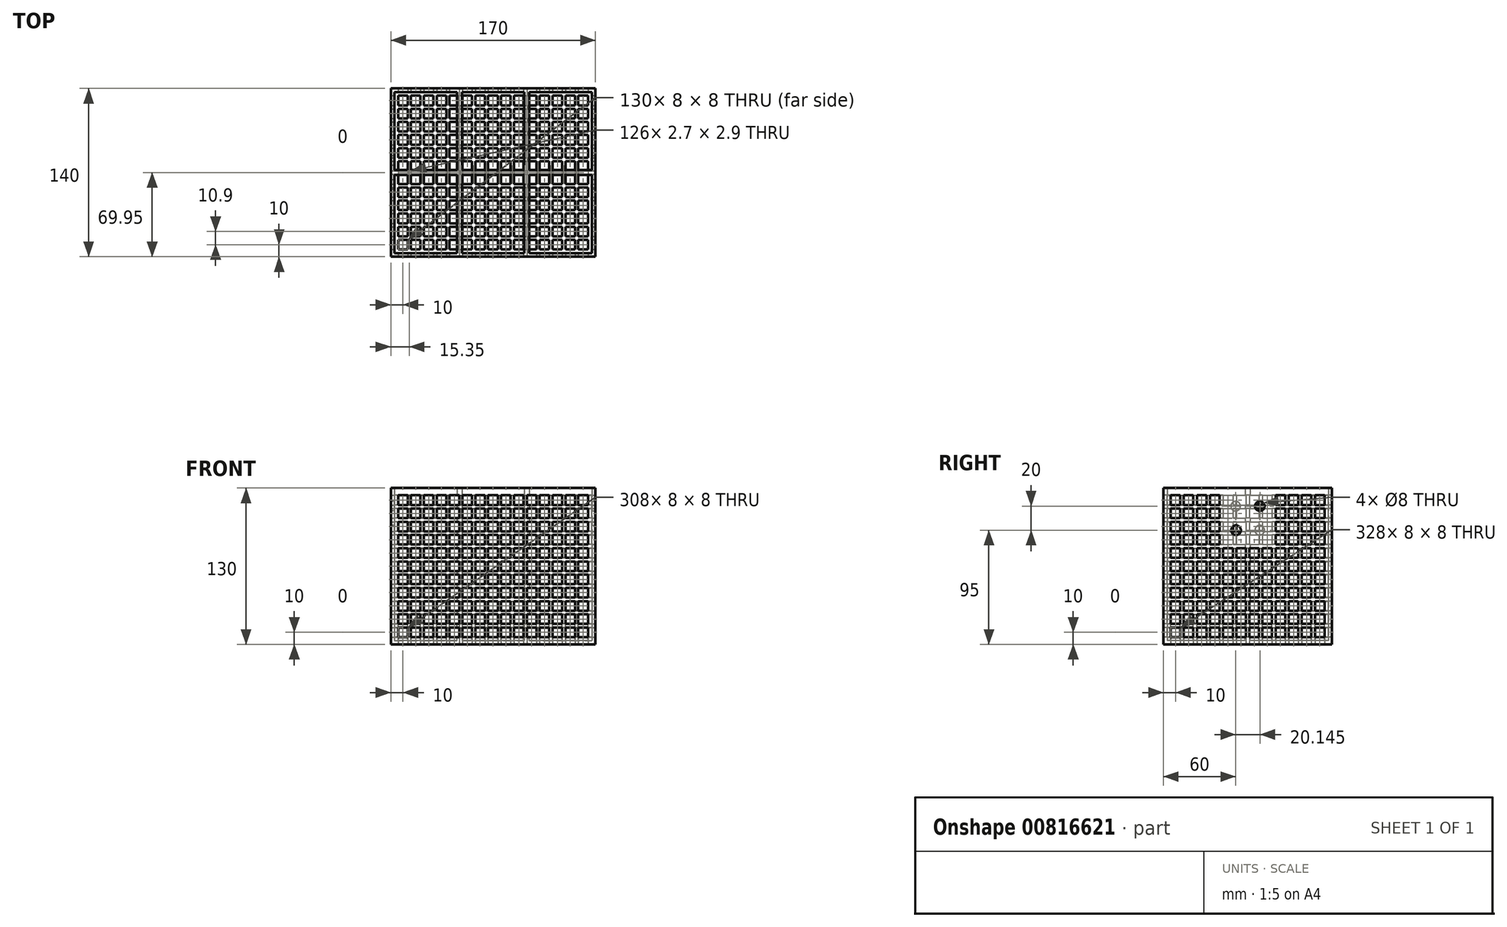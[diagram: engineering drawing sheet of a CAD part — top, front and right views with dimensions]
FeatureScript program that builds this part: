
annotation { "Feature Type Name" : "Feature", "Feature Type Description" : "" }
export const myFeature = defineFeature(function(context is Context, id is Id, definition is map)
    precondition{}
    {
        {
            var Q0;
            Q0=qCreatedBy(makeId("Top.planeOp"),FACE);
            var sketch = newSketch(context, id + "F0", { "sketchPlane" : qUnion([Q0])});
            skLineSegment(sketch, "E0.bottom", {"start": v(0, 0) * mm, "end": v(170, 0) * mm});
            skLineSegment(sketch, "E0.top", {"start": v(0, 140) * mm, "end": v(170, 140) * mm});
            skLineSegment(sketch, "E0.left", {"start": v(0, 0) * mm, "end": v(0, 140) * mm});
            skLineSegment(sketch, "E0.right", {"start": v(170, 0) * mm, "end": v(170, 140) * mm});
            skSolve(sketch);
        }
        {
            var Q0;
            Q0 = qSketchRegion(id + "F0", true);
            extrude(context, id + "F1", {"entities" : qUnion([Q0]), "depth" : 130 * mm, "offsetDistance" : 25 * mm});
        }
        {
            var Q0;
            Q0=qCreatedBy(makeId("Top.planeOp"),FACE);
            cPlane(context, id + "F2", {"entities" : qUnion([Q0]), "cplaneType" : CPlaneType.OFFSET, "offset" : 3 * mm, "width" : 150 * mm, "height" : 150 * mm});
        }
        {
            var Q0;
            Q0=qCreatedBy(id+"F2.planeOp",FACE);
            var sketch = newSketch(context, id + "F3", { "sketchPlane" : qUnion([Q0])});
            skLineSegment(sketch, "E1.bottom", {"start": v(3, 68) * mm, "end": v(55, 68) * mm});
            skLineSegment(sketch, "E1.top", {"start": v(3, 3) * mm, "end": v(55, 3) * mm});
            skLineSegment(sketch, "E1.left", {"start": v(3, 68) * mm, "end": v(3, 3) * mm});
            skLineSegment(sketch, "E1.right", {"start": v(55, 68) * mm, "end": v(55, 3) * mm});
            skLineSegment(sketch, "E2", {"start": v(0, 137) * mm, "end": v(173.16, 137) * mm, "construction": true});
            skLineSegment(sketch, "E3", {"start": v(167, 0) * mm, "end": v(167, 146.13) * mm, "construction": true});
            skLineSegment(sketch, "E4.0.1.0", {"start": v(3, 137) * mm, "end": v(55, 137) * mm});
            skLineSegment(sketch, "E4.0.1.1", {"start": v(55, 137) * mm, "end": v(55, 72) * mm});
            skLineSegment(sketch, "E4.0.1.2", {"start": v(3, 72) * mm, "end": v(55, 72) * mm});
            skLineSegment(sketch, "E4.0.1.3", {"start": v(3, 137) * mm, "end": v(3, 72) * mm});
            skLineSegment(sketch, "E4.1.0.0", {"start": v(59, 68) * mm, "end": v(111, 68) * mm});
            skLineSegment(sketch, "E4.1.0.1", {"start": v(111, 68) * mm, "end": v(111, 3) * mm});
            skLineSegment(sketch, "E4.1.0.2", {"start": v(59, 3) * mm, "end": v(111, 3) * mm});
            skLineSegment(sketch, "E4.1.0.3", {"start": v(59, 68) * mm, "end": v(59, 3) * mm});
            skLineSegment(sketch, "E4.1.1.0", {"start": v(59, 137) * mm, "end": v(111, 137) * mm});
            skLineSegment(sketch, "E4.1.1.1", {"start": v(111, 137) * mm, "end": v(111, 72) * mm});
            skLineSegment(sketch, "E4.1.1.2", {"start": v(59, 72) * mm, "end": v(111, 72) * mm});
            skLineSegment(sketch, "E4.1.1.3", {"start": v(59, 137) * mm, "end": v(59, 72) * mm});
            skLineSegment(sketch, "E4.2.0.0", {"start": v(115, 68) * mm, "end": v(167, 68) * mm});
            skLineSegment(sketch, "E4.2.0.1", {"start": v(167, 68) * mm, "end": v(167, 3) * mm});
            skLineSegment(sketch, "E4.2.0.2", {"start": v(115, 3) * mm, "end": v(167, 3) * mm});
            skLineSegment(sketch, "E4.2.0.3", {"start": v(115, 68) * mm, "end": v(115, 3) * mm});
            skLineSegment(sketch, "E4.2.1.0", {"start": v(115, 137) * mm, "end": v(167, 137) * mm});
            skLineSegment(sketch, "E4.2.1.1", {"start": v(167, 137) * mm, "end": v(167, 72) * mm});
            skLineSegment(sketch, "E4.2.1.2", {"start": v(115, 72) * mm, "end": v(167, 72) * mm});
            skLineSegment(sketch, "E4.2.1.3", {"start": v(115, 137) * mm, "end": v(115, 72) * mm});
            skLineSegment(sketch, "E4.direction1", {"start": v(3, 3) * mm, "end": v(59, 3) * mm, "construction": true});
            skLineSegment(sketch, "E4.direction2", {"start": v(3, 3) * mm, "end": v(3, 72) * mm, "construction": true});
            skSolve(sketch);
        }
        {
            var Q0;
            Q0 = qSketchRegion(id + "F3", true);
            extrude(context, id + "F4", {"entities" : qUnion([Q0]), "operationType" : NewBodyOperationType.REMOVE, "endBound" : BoundingType.UP_TO_NEXT, "depth" : 25 * mm, "offsetDistance" : 25 * mm});
        }
        {
            var Q0;
            Q0=makeQuery(id+"F1.opExtrude","SWEPT_FACE",FACE,{"disambiguationData":[OSD([sQuery(id+"F0.wireOp",EDGE,"E0.right")])]});
            var sketch = newSketch(context, id + "F5", { "sketchPlane" : qUnion([Q0])});
            skLineSegment(sketch, "E5.bottom", {"start": v(6, 14) * mm, "end": v(14, 14) * mm});
            skLineSegment(sketch, "E5.top", {"start": v(6, 6) * mm, "end": v(14, 6) * mm});
            skLineSegment(sketch, "E5.left", {"start": v(6, 14) * mm, "end": v(6, 6) * mm});
            skLineSegment(sketch, "E5.right", {"start": v(14, 14) * mm, "end": v(14, 6) * mm});
            skLineSegment(sketch, "E6.0.1.0", {"start": v(6, 25) * mm, "end": v(14, 25) * mm});
            skLineSegment(sketch, "E6.0.1.1", {"start": v(6, 25) * mm, "end": v(6, 17) * mm});
            skLineSegment(sketch, "E6.0.1.2", {"start": v(14, 25) * mm, "end": v(14, 17) * mm});
            skLineSegment(sketch, "E6.0.1.3", {"start": v(6, 17) * mm, "end": v(14, 17) * mm});
            skLineSegment(sketch, "E6.0.2.0", {"start": v(6, 36) * mm, "end": v(14, 36) * mm});
            skLineSegment(sketch, "E6.0.2.1", {"start": v(6, 36) * mm, "end": v(6, 28) * mm});
            skLineSegment(sketch, "E6.0.2.2", {"start": v(14, 36) * mm, "end": v(14, 28) * mm});
            skLineSegment(sketch, "E6.0.2.3", {"start": v(6, 28) * mm, "end": v(14, 28) * mm});
            skLineSegment(sketch, "E6.0.3.0", {"start": v(6, 47) * mm, "end": v(14, 47) * mm});
            skLineSegment(sketch, "E6.0.3.1", {"start": v(6, 47) * mm, "end": v(6, 39) * mm});
            skLineSegment(sketch, "E6.0.3.2", {"start": v(14, 47) * mm, "end": v(14, 39) * mm});
            skLineSegment(sketch, "E6.0.3.3", {"start": v(6, 39) * mm, "end": v(14, 39) * mm});
            skLineSegment(sketch, "E6.0.4.0", {"start": v(6, 58) * mm, "end": v(14, 58) * mm});
            skLineSegment(sketch, "E6.0.4.1", {"start": v(6, 58) * mm, "end": v(6, 50) * mm});
            skLineSegment(sketch, "E6.0.4.2", {"start": v(14, 58) * mm, "end": v(14, 50) * mm});
            skLineSegment(sketch, "E6.0.4.3", {"start": v(6, 50) * mm, "end": v(14, 50) * mm});
            skLineSegment(sketch, "E6.0.5.0", {"start": v(6, 69) * mm, "end": v(14, 69) * mm});
            skLineSegment(sketch, "E6.0.5.1", {"start": v(6, 69) * mm, "end": v(6, 61) * mm});
            skLineSegment(sketch, "E6.0.5.2", {"start": v(14, 69) * mm, "end": v(14, 61) * mm});
            skLineSegment(sketch, "E6.0.5.3", {"start": v(6, 61) * mm, "end": v(14, 61) * mm});
            skLineSegment(sketch, "E6.0.6.0", {"start": v(6, 80) * mm, "end": v(14, 80) * mm});
            skLineSegment(sketch, "E6.0.6.1", {"start": v(6, 80) * mm, "end": v(6, 72) * mm});
            skLineSegment(sketch, "E6.0.6.2", {"start": v(14, 80) * mm, "end": v(14, 72) * mm});
            skLineSegment(sketch, "E6.0.6.3", {"start": v(6, 72) * mm, "end": v(14, 72) * mm});
            skLineSegment(sketch, "E6.0.7.0", {"start": v(6, 91) * mm, "end": v(14, 91) * mm});
            skLineSegment(sketch, "E6.0.7.1", {"start": v(6, 91) * mm, "end": v(6, 83) * mm});
            skLineSegment(sketch, "E6.0.7.2", {"start": v(14, 91) * mm, "end": v(14, 83) * mm});
            skLineSegment(sketch, "E6.0.7.3", {"start": v(6, 83) * mm, "end": v(14, 83) * mm});
            skLineSegment(sketch, "E6.0.8.0", {"start": v(6, 102) * mm, "end": v(14, 102) * mm});
            skLineSegment(sketch, "E6.0.8.1", {"start": v(6, 102) * mm, "end": v(6, 94) * mm});
            skLineSegment(sketch, "E6.0.8.2", {"start": v(14, 102) * mm, "end": v(14, 94) * mm});
            skLineSegment(sketch, "E6.0.8.3", {"start": v(6, 94) * mm, "end": v(14, 94) * mm});
            skLineSegment(sketch, "E6.0.9.0", {"start": v(6, 113) * mm, "end": v(14, 113) * mm});
            skLineSegment(sketch, "E6.0.9.1", {"start": v(6, 113) * mm, "end": v(6, 105) * mm});
            skLineSegment(sketch, "E6.0.9.2", {"start": v(14, 113) * mm, "end": v(14, 105) * mm});
            skLineSegment(sketch, "E6.0.9.3", {"start": v(6, 105) * mm, "end": v(14, 105) * mm});
            skLineSegment(sketch, "E6.0.10.0", {"start": v(6, 124) * mm, "end": v(14, 124) * mm});
            skLineSegment(sketch, "E6.0.10.1", {"start": v(6, 124) * mm, "end": v(6, 116) * mm});
            skLineSegment(sketch, "E6.0.10.2", {"start": v(14, 124) * mm, "end": v(14, 116) * mm});
            skLineSegment(sketch, "E6.0.10.3", {"start": v(6, 116) * mm, "end": v(14, 116) * mm});
            skLineSegment(sketch, "E6.1.0.0", {"start": v(16.9, 14) * mm, "end": v(24.9, 14) * mm});
            skLineSegment(sketch, "E6.1.0.1", {"start": v(16.9, 14) * mm, "end": v(16.9, 6) * mm});
            skLineSegment(sketch, "E6.1.0.2", {"start": v(24.9, 14) * mm, "end": v(24.9, 6) * mm});
            skLineSegment(sketch, "E6.1.0.3", {"start": v(16.9, 6) * mm, "end": v(24.9, 6) * mm});
            skLineSegment(sketch, "E6.1.1.0", {"start": v(16.9, 25) * mm, "end": v(24.9, 25) * mm});
            skLineSegment(sketch, "E6.1.1.1", {"start": v(16.9, 25) * mm, "end": v(16.9, 17) * mm});
            skLineSegment(sketch, "E6.1.1.2", {"start": v(24.9, 25) * mm, "end": v(24.9, 17) * mm});
            skLineSegment(sketch, "E6.1.1.3", {"start": v(16.9, 17) * mm, "end": v(24.9, 17) * mm});
            skLineSegment(sketch, "E6.1.2.0", {"start": v(16.9, 36) * mm, "end": v(24.9, 36) * mm});
            skLineSegment(sketch, "E6.1.2.1", {"start": v(16.9, 36) * mm, "end": v(16.9, 28) * mm});
            skLineSegment(sketch, "E6.1.2.2", {"start": v(24.9, 36) * mm, "end": v(24.9, 28) * mm});
            skLineSegment(sketch, "E6.1.2.3", {"start": v(16.9, 28) * mm, "end": v(24.9, 28) * mm});
            skLineSegment(sketch, "E6.1.3.0", {"start": v(16.9, 47) * mm, "end": v(24.9, 47) * mm});
            skLineSegment(sketch, "E6.1.3.1", {"start": v(16.9, 47) * mm, "end": v(16.9, 39) * mm});
            skLineSegment(sketch, "E6.1.3.2", {"start": v(24.9, 47) * mm, "end": v(24.9, 39) * mm});
            skLineSegment(sketch, "E6.1.3.3", {"start": v(16.9, 39) * mm, "end": v(24.9, 39) * mm});
            skLineSegment(sketch, "E6.1.4.0", {"start": v(16.9, 58) * mm, "end": v(24.9, 58) * mm});
            skLineSegment(sketch, "E6.1.4.1", {"start": v(16.9, 58) * mm, "end": v(16.9, 50) * mm});
            skLineSegment(sketch, "E6.1.4.2", {"start": v(24.9, 58) * mm, "end": v(24.9, 50) * mm});
            skLineSegment(sketch, "E6.1.4.3", {"start": v(16.9, 50) * mm, "end": v(24.9, 50) * mm});
            skLineSegment(sketch, "E6.1.5.0", {"start": v(16.9, 69) * mm, "end": v(24.9, 69) * mm});
            skLineSegment(sketch, "E6.1.5.1", {"start": v(16.9, 69) * mm, "end": v(16.9, 61) * mm});
            skLineSegment(sketch, "E6.1.5.2", {"start": v(24.9, 69) * mm, "end": v(24.9, 61) * mm});
            skLineSegment(sketch, "E6.1.5.3", {"start": v(16.9, 61) * mm, "end": v(24.9, 61) * mm});
            skLineSegment(sketch, "E6.1.6.0", {"start": v(16.9, 80) * mm, "end": v(24.9, 80) * mm});
            skLineSegment(sketch, "E6.1.6.1", {"start": v(16.9, 80) * mm, "end": v(16.9, 72) * mm});
            skLineSegment(sketch, "E6.1.6.2", {"start": v(24.9, 80) * mm, "end": v(24.9, 72) * mm});
            skLineSegment(sketch, "E6.1.6.3", {"start": v(16.9, 72) * mm, "end": v(24.9, 72) * mm});
            skLineSegment(sketch, "E6.1.7.0", {"start": v(16.9, 91) * mm, "end": v(24.9, 91) * mm});
            skLineSegment(sketch, "E6.1.7.1", {"start": v(16.9, 91) * mm, "end": v(16.9, 83) * mm});
            skLineSegment(sketch, "E6.1.7.2", {"start": v(24.9, 91) * mm, "end": v(24.9, 83) * mm});
            skLineSegment(sketch, "E6.1.7.3", {"start": v(16.9, 83) * mm, "end": v(24.9, 83) * mm});
            skLineSegment(sketch, "E6.1.8.0", {"start": v(16.9, 102) * mm, "end": v(24.9, 102) * mm});
            skLineSegment(sketch, "E6.1.8.1", {"start": v(16.9, 102) * mm, "end": v(16.9, 94) * mm});
            skLineSegment(sketch, "E6.1.8.2", {"start": v(24.9, 102) * mm, "end": v(24.9, 94) * mm});
            skLineSegment(sketch, "E6.1.8.3", {"start": v(16.9, 94) * mm, "end": v(24.9, 94) * mm});
            skLineSegment(sketch, "E6.1.9.0", {"start": v(16.9, 113) * mm, "end": v(24.9, 113) * mm});
            skLineSegment(sketch, "E6.1.9.1", {"start": v(16.9, 113) * mm, "end": v(16.9, 105) * mm});
            skLineSegment(sketch, "E6.1.9.2", {"start": v(24.9, 113) * mm, "end": v(24.9, 105) * mm});
            skLineSegment(sketch, "E6.1.9.3", {"start": v(16.9, 105) * mm, "end": v(24.9, 105) * mm});
            skLineSegment(sketch, "E6.1.10.0", {"start": v(16.9, 124) * mm, "end": v(24.9, 124) * mm});
            skLineSegment(sketch, "E6.1.10.1", {"start": v(16.9, 124) * mm, "end": v(16.9, 116) * mm});
            skLineSegment(sketch, "E6.1.10.2", {"start": v(24.9, 124) * mm, "end": v(24.9, 116) * mm});
            skLineSegment(sketch, "E6.1.10.3", {"start": v(16.9, 116) * mm, "end": v(24.9, 116) * mm});
            skLineSegment(sketch, "E6.2.0.0", {"start": v(27.8, 14) * mm, "end": v(35.8, 14) * mm});
            skLineSegment(sketch, "E6.2.0.1", {"start": v(27.8, 14) * mm, "end": v(27.8, 6) * mm});
            skLineSegment(sketch, "E6.2.0.2", {"start": v(35.8, 14) * mm, "end": v(35.8, 6) * mm});
            skLineSegment(sketch, "E6.2.0.3", {"start": v(27.8, 6) * mm, "end": v(35.8, 6) * mm});
            skLineSegment(sketch, "E6.2.1.0", {"start": v(27.8, 25) * mm, "end": v(35.8, 25) * mm});
            skLineSegment(sketch, "E6.2.1.1", {"start": v(27.8, 25) * mm, "end": v(27.8, 17) * mm});
            skLineSegment(sketch, "E6.2.1.2", {"start": v(35.8, 25) * mm, "end": v(35.8, 17) * mm});
            skLineSegment(sketch, "E6.2.1.3", {"start": v(27.8, 17) * mm, "end": v(35.8, 17) * mm});
            skLineSegment(sketch, "E6.2.2.0", {"start": v(27.8, 36) * mm, "end": v(35.8, 36) * mm});
            skLineSegment(sketch, "E6.2.2.1", {"start": v(27.8, 36) * mm, "end": v(27.8, 28) * mm});
            skLineSegment(sketch, "E6.2.2.2", {"start": v(35.8, 36) * mm, "end": v(35.8, 28) * mm});
            skLineSegment(sketch, "E6.2.2.3", {"start": v(27.8, 28) * mm, "end": v(35.8, 28) * mm});
            skLineSegment(sketch, "E6.2.3.0", {"start": v(27.8, 47) * mm, "end": v(35.8, 47) * mm});
            skLineSegment(sketch, "E6.2.3.1", {"start": v(27.8, 47) * mm, "end": v(27.8, 39) * mm});
            skLineSegment(sketch, "E6.2.3.2", {"start": v(35.8, 47) * mm, "end": v(35.8, 39) * mm});
            skLineSegment(sketch, "E6.2.3.3", {"start": v(27.8, 39) * mm, "end": v(35.8, 39) * mm});
            skLineSegment(sketch, "E6.2.4.0", {"start": v(27.8, 58) * mm, "end": v(35.8, 58) * mm});
            skLineSegment(sketch, "E6.2.4.1", {"start": v(27.8, 58) * mm, "end": v(27.8, 50) * mm});
            skLineSegment(sketch, "E6.2.4.2", {"start": v(35.8, 58) * mm, "end": v(35.8, 50) * mm});
            skLineSegment(sketch, "E6.2.4.3", {"start": v(27.8, 50) * mm, "end": v(35.8, 50) * mm});
            skLineSegment(sketch, "E6.2.5.0", {"start": v(27.8, 69) * mm, "end": v(35.8, 69) * mm});
            skLineSegment(sketch, "E6.2.5.1", {"start": v(27.8, 69) * mm, "end": v(27.8, 61) * mm});
            skLineSegment(sketch, "E6.2.5.2", {"start": v(35.8, 69) * mm, "end": v(35.8, 61) * mm});
            skLineSegment(sketch, "E6.2.5.3", {"start": v(27.8, 61) * mm, "end": v(35.8, 61) * mm});
            skLineSegment(sketch, "E6.2.6.0", {"start": v(27.8, 80) * mm, "end": v(35.8, 80) * mm});
            skLineSegment(sketch, "E6.2.6.1", {"start": v(27.8, 80) * mm, "end": v(27.8, 72) * mm});
            skLineSegment(sketch, "E6.2.6.2", {"start": v(35.8, 80) * mm, "end": v(35.8, 72) * mm});
            skLineSegment(sketch, "E6.2.6.3", {"start": v(27.8, 72) * mm, "end": v(35.8, 72) * mm});
            skLineSegment(sketch, "E6.2.7.0", {"start": v(27.8, 91) * mm, "end": v(35.8, 91) * mm});
            skLineSegment(sketch, "E6.2.7.1", {"start": v(27.8, 91) * mm, "end": v(27.8, 83) * mm});
            skLineSegment(sketch, "E6.2.7.2", {"start": v(35.8, 91) * mm, "end": v(35.8, 83) * mm});
            skLineSegment(sketch, "E6.2.7.3", {"start": v(27.8, 83) * mm, "end": v(35.8, 83) * mm});
            skLineSegment(sketch, "E6.2.8.0", {"start": v(27.8, 102) * mm, "end": v(35.8, 102) * mm});
            skLineSegment(sketch, "E6.2.8.1", {"start": v(27.8, 102) * mm, "end": v(27.8, 94) * mm});
            skLineSegment(sketch, "E6.2.8.2", {"start": v(35.8, 102) * mm, "end": v(35.8, 94) * mm});
            skLineSegment(sketch, "E6.2.8.3", {"start": v(27.8, 94) * mm, "end": v(35.8, 94) * mm});
            skLineSegment(sketch, "E6.2.9.0", {"start": v(27.8, 113) * mm, "end": v(35.8, 113) * mm});
            skLineSegment(sketch, "E6.2.9.1", {"start": v(27.8, 113) * mm, "end": v(27.8, 105) * mm});
            skLineSegment(sketch, "E6.2.9.2", {"start": v(35.8, 113) * mm, "end": v(35.8, 105) * mm});
            skLineSegment(sketch, "E6.2.9.3", {"start": v(27.8, 105) * mm, "end": v(35.8, 105) * mm});
            skLineSegment(sketch, "E6.2.10.0", {"start": v(27.8, 124) * mm, "end": v(35.8, 124) * mm});
            skLineSegment(sketch, "E6.2.10.1", {"start": v(27.8, 124) * mm, "end": v(27.8, 116) * mm});
            skLineSegment(sketch, "E6.2.10.2", {"start": v(35.8, 124) * mm, "end": v(35.8, 116) * mm});
            skLineSegment(sketch, "E6.2.10.3", {"start": v(27.8, 116) * mm, "end": v(35.8, 116) * mm});
            skLineSegment(sketch, "E6.3.0.0", {"start": v(38.7, 14) * mm, "end": v(46.7, 14) * mm});
            skLineSegment(sketch, "E6.3.0.1", {"start": v(38.7, 14) * mm, "end": v(38.7, 6) * mm});
            skLineSegment(sketch, "E6.3.0.2", {"start": v(46.7, 14) * mm, "end": v(46.7, 6) * mm});
            skLineSegment(sketch, "E6.3.0.3", {"start": v(38.7, 6) * mm, "end": v(46.7, 6) * mm});
            skLineSegment(sketch, "E6.3.1.0", {"start": v(38.7, 25) * mm, "end": v(46.7, 25) * mm});
            skLineSegment(sketch, "E6.3.1.1", {"start": v(38.7, 25) * mm, "end": v(38.7, 17) * mm});
            skLineSegment(sketch, "E6.3.1.2", {"start": v(46.7, 25) * mm, "end": v(46.7, 17) * mm});
            skLineSegment(sketch, "E6.3.1.3", {"start": v(38.7, 17) * mm, "end": v(46.7, 17) * mm});
            skLineSegment(sketch, "E6.3.2.0", {"start": v(38.7, 36) * mm, "end": v(46.7, 36) * mm});
            skLineSegment(sketch, "E6.3.2.1", {"start": v(38.7, 36) * mm, "end": v(38.7, 28) * mm});
            skLineSegment(sketch, "E6.3.2.2", {"start": v(46.7, 36) * mm, "end": v(46.7, 28) * mm});
            skLineSegment(sketch, "E6.3.2.3", {"start": v(38.7, 28) * mm, "end": v(46.7, 28) * mm});
            skLineSegment(sketch, "E6.3.3.0", {"start": v(38.7, 47) * mm, "end": v(46.7, 47) * mm});
            skLineSegment(sketch, "E6.3.3.1", {"start": v(38.7, 47) * mm, "end": v(38.7, 39) * mm});
            skLineSegment(sketch, "E6.3.3.2", {"start": v(46.7, 47) * mm, "end": v(46.7, 39) * mm});
            skLineSegment(sketch, "E6.3.3.3", {"start": v(38.7, 39) * mm, "end": v(46.7, 39) * mm});
            skLineSegment(sketch, "E6.3.4.0", {"start": v(38.7, 58) * mm, "end": v(46.7, 58) * mm});
            skLineSegment(sketch, "E6.3.4.1", {"start": v(38.7, 58) * mm, "end": v(38.7, 50) * mm});
            skLineSegment(sketch, "E6.3.4.2", {"start": v(46.7, 58) * mm, "end": v(46.7, 50) * mm});
            skLineSegment(sketch, "E6.3.4.3", {"start": v(38.7, 50) * mm, "end": v(46.7, 50) * mm});
            skLineSegment(sketch, "E6.3.5.0", {"start": v(38.7, 69) * mm, "end": v(46.7, 69) * mm});
            skLineSegment(sketch, "E6.3.5.1", {"start": v(38.7, 69) * mm, "end": v(38.7, 61) * mm});
            skLineSegment(sketch, "E6.3.5.2", {"start": v(46.7, 69) * mm, "end": v(46.7, 61) * mm});
            skLineSegment(sketch, "E6.3.5.3", {"start": v(38.7, 61) * mm, "end": v(46.7, 61) * mm});
            skLineSegment(sketch, "E6.3.6.0", {"start": v(38.7, 80) * mm, "end": v(46.7, 80) * mm});
            skLineSegment(sketch, "E6.3.6.1", {"start": v(38.7, 80) * mm, "end": v(38.7, 72) * mm});
            skLineSegment(sketch, "E6.3.6.2", {"start": v(46.7, 80) * mm, "end": v(46.7, 72) * mm});
            skLineSegment(sketch, "E6.3.6.3", {"start": v(38.7, 72) * mm, "end": v(46.7, 72) * mm});
            skLineSegment(sketch, "E6.3.7.0", {"start": v(38.7, 91) * mm, "end": v(46.7, 91) * mm});
            skLineSegment(sketch, "E6.3.7.1", {"start": v(38.7, 91) * mm, "end": v(38.7, 83) * mm});
            skLineSegment(sketch, "E6.3.7.2", {"start": v(46.7, 91) * mm, "end": v(46.7, 83) * mm});
            skLineSegment(sketch, "E6.3.7.3", {"start": v(38.7, 83) * mm, "end": v(46.7, 83) * mm});
            skLineSegment(sketch, "E6.3.8.0", {"start": v(38.7, 102) * mm, "end": v(46.7, 102) * mm});
            skLineSegment(sketch, "E6.3.8.1", {"start": v(38.7, 102) * mm, "end": v(38.7, 94) * mm});
            skLineSegment(sketch, "E6.3.8.2", {"start": v(46.7, 102) * mm, "end": v(46.7, 94) * mm});
            skLineSegment(sketch, "E6.3.8.3", {"start": v(38.7, 94) * mm, "end": v(46.7, 94) * mm});
            skLineSegment(sketch, "E6.3.9.0", {"start": v(38.7, 113) * mm, "end": v(46.7, 113) * mm});
            skLineSegment(sketch, "E6.3.9.1", {"start": v(38.7, 113) * mm, "end": v(38.7, 105) * mm});
            skLineSegment(sketch, "E6.3.9.2", {"start": v(46.7, 113) * mm, "end": v(46.7, 105) * mm});
            skLineSegment(sketch, "E6.3.9.3", {"start": v(38.7, 105) * mm, "end": v(46.7, 105) * mm});
            skLineSegment(sketch, "E6.3.10.0", {"start": v(38.7, 124) * mm, "end": v(46.7, 124) * mm});
            skLineSegment(sketch, "E6.3.10.1", {"start": v(38.7, 124) * mm, "end": v(38.7, 116) * mm});
            skLineSegment(sketch, "E6.3.10.2", {"start": v(46.7, 124) * mm, "end": v(46.7, 116) * mm});
            skLineSegment(sketch, "E6.3.10.3", {"start": v(38.7, 116) * mm, "end": v(46.7, 116) * mm});
            skLineSegment(sketch, "E6.4.0.0", {"start": v(49.6, 14) * mm, "end": v(57.6, 14) * mm});
            skLineSegment(sketch, "E6.4.0.1", {"start": v(49.6, 14) * mm, "end": v(49.6, 6) * mm});
            skLineSegment(sketch, "E6.4.0.2", {"start": v(57.6, 14) * mm, "end": v(57.6, 6) * mm});
            skLineSegment(sketch, "E6.4.0.3", {"start": v(49.6, 6) * mm, "end": v(57.6, 6) * mm});
            skLineSegment(sketch, "E6.4.1.0", {"start": v(49.6, 25) * mm, "end": v(57.6, 25) * mm});
            skLineSegment(sketch, "E6.4.1.1", {"start": v(49.6, 25) * mm, "end": v(49.6, 17) * mm});
            skLineSegment(sketch, "E6.4.1.2", {"start": v(57.6, 25) * mm, "end": v(57.6, 17) * mm});
            skLineSegment(sketch, "E6.4.1.3", {"start": v(49.6, 17) * mm, "end": v(57.6, 17) * mm});
            skLineSegment(sketch, "E6.4.2.0", {"start": v(49.6, 36) * mm, "end": v(57.6, 36) * mm});
            skLineSegment(sketch, "E6.4.2.1", {"start": v(49.6, 36) * mm, "end": v(49.6, 28) * mm});
            skLineSegment(sketch, "E6.4.2.2", {"start": v(57.6, 36) * mm, "end": v(57.6, 28) * mm});
            skLineSegment(sketch, "E6.4.2.3", {"start": v(49.6, 28) * mm, "end": v(57.6, 28) * mm});
            skLineSegment(sketch, "E6.4.3.0", {"start": v(49.6, 47) * mm, "end": v(57.6, 47) * mm});
            skLineSegment(sketch, "E6.4.3.1", {"start": v(49.6, 47) * mm, "end": v(49.6, 39) * mm});
            skLineSegment(sketch, "E6.4.3.2", {"start": v(57.6, 47) * mm, "end": v(57.6, 39) * mm});
            skLineSegment(sketch, "E6.4.3.3", {"start": v(49.6, 39) * mm, "end": v(57.6, 39) * mm});
            skLineSegment(sketch, "E6.4.4.0", {"start": v(49.6, 58) * mm, "end": v(57.6, 58) * mm});
            skLineSegment(sketch, "E6.4.4.1", {"start": v(49.6, 58) * mm, "end": v(49.6, 50) * mm});
            skLineSegment(sketch, "E6.4.4.2", {"start": v(57.6, 58) * mm, "end": v(57.6, 50) * mm});
            skLineSegment(sketch, "E6.4.4.3", {"start": v(49.6, 50) * mm, "end": v(57.6, 50) * mm});
            skLineSegment(sketch, "E6.4.5.0", {"start": v(49.6, 69) * mm, "end": v(57.6, 69) * mm});
            skLineSegment(sketch, "E6.4.5.1", {"start": v(49.6, 69) * mm, "end": v(49.6, 61) * mm});
            skLineSegment(sketch, "E6.4.5.2", {"start": v(57.6, 69) * mm, "end": v(57.6, 61) * mm});
            skLineSegment(sketch, "E6.4.5.3", {"start": v(49.6, 61) * mm, "end": v(57.6, 61) * mm});
            skLineSegment(sketch, "E6.4.6.0", {"start": v(49.6, 80) * mm, "end": v(57.6, 80) * mm});
            skLineSegment(sketch, "E6.4.6.1", {"start": v(49.6, 80) * mm, "end": v(49.6, 72) * mm});
            skLineSegment(sketch, "E6.4.6.2", {"start": v(57.6, 80) * mm, "end": v(57.6, 72) * mm});
            skLineSegment(sketch, "E6.4.6.3", {"start": v(49.6, 72) * mm, "end": v(57.6, 72) * mm});
            skLineSegment(sketch, "E6.4.7.0", {"start": v(49.6, 91) * mm, "end": v(57.6, 91) * mm});
            skLineSegment(sketch, "E6.4.7.1", {"start": v(49.6, 91) * mm, "end": v(49.6, 83) * mm});
            skLineSegment(sketch, "E6.4.7.2", {"start": v(57.6, 91) * mm, "end": v(57.6, 83) * mm});
            skLineSegment(sketch, "E6.4.7.3", {"start": v(49.6, 83) * mm, "end": v(57.6, 83) * mm});
            skLineSegment(sketch, "E6.4.8.0", {"start": v(49.6, 102) * mm, "end": v(57.6, 102) * mm});
            skLineSegment(sketch, "E6.4.8.1", {"start": v(49.6, 102) * mm, "end": v(49.6, 94) * mm});
            skLineSegment(sketch, "E6.4.8.2", {"start": v(57.6, 102) * mm, "end": v(57.6, 94) * mm});
            skLineSegment(sketch, "E6.4.8.3", {"start": v(49.6, 94) * mm, "end": v(57.6, 94) * mm});
            skLineSegment(sketch, "E6.4.9.0", {"start": v(49.6, 113) * mm, "end": v(57.6, 113) * mm});
            skLineSegment(sketch, "E6.4.9.1", {"start": v(49.6, 113) * mm, "end": v(49.6, 105) * mm});
            skLineSegment(sketch, "E6.4.9.2", {"start": v(57.6, 113) * mm, "end": v(57.6, 105) * mm});
            skLineSegment(sketch, "E6.4.9.3", {"start": v(49.6, 105) * mm, "end": v(57.6, 105) * mm});
            skLineSegment(sketch, "E6.4.10.0", {"start": v(49.6, 124) * mm, "end": v(57.6, 124) * mm});
            skLineSegment(sketch, "E6.4.10.1", {"start": v(49.6, 124) * mm, "end": v(49.6, 116) * mm});
            skLineSegment(sketch, "E6.4.10.2", {"start": v(57.6, 124) * mm, "end": v(57.6, 116) * mm});
            skLineSegment(sketch, "E6.4.10.3", {"start": v(49.6, 116) * mm, "end": v(57.6, 116) * mm});
            skLineSegment(sketch, "E6.5.0.0", {"start": v(60.5, 14) * mm, "end": v(68.5, 14) * mm});
            skLineSegment(sketch, "E6.5.0.1", {"start": v(60.5, 14) * mm, "end": v(60.5, 6) * mm});
            skLineSegment(sketch, "E6.5.0.2", {"start": v(68.5, 14) * mm, "end": v(68.5, 6) * mm});
            skLineSegment(sketch, "E6.5.0.3", {"start": v(60.5, 6) * mm, "end": v(68.5, 6) * mm});
            skLineSegment(sketch, "E6.5.1.0", {"start": v(60.5, 25) * mm, "end": v(68.5, 25) * mm});
            skLineSegment(sketch, "E6.5.1.1", {"start": v(60.5, 25) * mm, "end": v(60.5, 17) * mm});
            skLineSegment(sketch, "E6.5.1.2", {"start": v(68.5, 25) * mm, "end": v(68.5, 17) * mm});
            skLineSegment(sketch, "E6.5.1.3", {"start": v(60.5, 17) * mm, "end": v(68.5, 17) * mm});
            skLineSegment(sketch, "E6.5.2.0", {"start": v(60.5, 36) * mm, "end": v(68.5, 36) * mm});
            skLineSegment(sketch, "E6.5.2.1", {"start": v(60.5, 36) * mm, "end": v(60.5, 28) * mm});
            skLineSegment(sketch, "E6.5.2.2", {"start": v(68.5, 36) * mm, "end": v(68.5, 28) * mm});
            skLineSegment(sketch, "E6.5.2.3", {"start": v(60.5, 28) * mm, "end": v(68.5, 28) * mm});
            skLineSegment(sketch, "E6.5.3.0", {"start": v(60.5, 47) * mm, "end": v(68.5, 47) * mm});
            skLineSegment(sketch, "E6.5.3.1", {"start": v(60.5, 47) * mm, "end": v(60.5, 39) * mm});
            skLineSegment(sketch, "E6.5.3.2", {"start": v(68.5, 47) * mm, "end": v(68.5, 39) * mm});
            skLineSegment(sketch, "E6.5.3.3", {"start": v(60.5, 39) * mm, "end": v(68.5, 39) * mm});
            skLineSegment(sketch, "E6.5.4.0", {"start": v(60.5, 58) * mm, "end": v(68.5, 58) * mm});
            skLineSegment(sketch, "E6.5.4.1", {"start": v(60.5, 58) * mm, "end": v(60.5, 50) * mm});
            skLineSegment(sketch, "E6.5.4.2", {"start": v(68.5, 58) * mm, "end": v(68.5, 50) * mm});
            skLineSegment(sketch, "E6.5.4.3", {"start": v(60.5, 50) * mm, "end": v(68.5, 50) * mm});
            skLineSegment(sketch, "E6.5.5.0", {"start": v(60.5, 69) * mm, "end": v(68.5, 69) * mm});
            skLineSegment(sketch, "E6.5.5.1", {"start": v(60.5, 69) * mm, "end": v(60.5, 61) * mm});
            skLineSegment(sketch, "E6.5.5.2", {"start": v(68.5, 69) * mm, "end": v(68.5, 61) * mm});
            skLineSegment(sketch, "E6.5.5.3", {"start": v(60.5, 61) * mm, "end": v(68.5, 61) * mm});
            skLineSegment(sketch, "E6.5.6.0", {"start": v(60.5, 80) * mm, "end": v(68.5, 80) * mm});
            skLineSegment(sketch, "E6.5.6.1", {"start": v(60.5, 80) * mm, "end": v(60.5, 72) * mm});
            skLineSegment(sketch, "E6.5.6.2", {"start": v(68.5, 80) * mm, "end": v(68.5, 72) * mm});
            skLineSegment(sketch, "E6.5.6.3", {"start": v(60.5, 72) * mm, "end": v(68.5, 72) * mm});
            skLineSegment(sketch, "E6.5.7.0", {"start": v(60.5, 91) * mm, "end": v(68.5, 91) * mm});
            skLineSegment(sketch, "E6.5.7.1", {"start": v(60.5, 91) * mm, "end": v(60.5, 83) * mm});
            skLineSegment(sketch, "E6.5.7.2", {"start": v(68.5, 91) * mm, "end": v(68.5, 83) * mm});
            skLineSegment(sketch, "E6.5.7.3", {"start": v(60.5, 83) * mm, "end": v(68.5, 83) * mm});
            skLineSegment(sketch, "E6.5.8.0", {"start": v(60.5, 102) * mm, "end": v(68.5, 102) * mm});
            skLineSegment(sketch, "E6.5.8.1", {"start": v(60.5, 102) * mm, "end": v(60.5, 94) * mm});
            skLineSegment(sketch, "E6.5.8.2", {"start": v(68.5, 102) * mm, "end": v(68.5, 94) * mm});
            skLineSegment(sketch, "E6.5.8.3", {"start": v(60.5, 94) * mm, "end": v(68.5, 94) * mm});
            skLineSegment(sketch, "E6.5.9.0", {"start": v(60.5, 113) * mm, "end": v(68.5, 113) * mm});
            skLineSegment(sketch, "E6.5.9.1", {"start": v(60.5, 113) * mm, "end": v(60.5, 105) * mm});
            skLineSegment(sketch, "E6.5.9.2", {"start": v(68.5, 113) * mm, "end": v(68.5, 105) * mm});
            skLineSegment(sketch, "E6.5.9.3", {"start": v(60.5, 105) * mm, "end": v(68.5, 105) * mm});
            skLineSegment(sketch, "E6.5.10.0", {"start": v(60.5, 124) * mm, "end": v(68.5, 124) * mm});
            skLineSegment(sketch, "E6.5.10.1", {"start": v(60.5, 124) * mm, "end": v(60.5, 116) * mm});
            skLineSegment(sketch, "E6.5.10.2", {"start": v(68.5, 124) * mm, "end": v(68.5, 116) * mm});
            skLineSegment(sketch, "E6.5.10.3", {"start": v(60.5, 116) * mm, "end": v(68.5, 116) * mm});
            skLineSegment(sketch, "E6.6.0.0", {"start": v(71.4, 14) * mm, "end": v(79.4, 14) * mm});
            skLineSegment(sketch, "E6.6.0.1", {"start": v(71.4, 14) * mm, "end": v(71.4, 6) * mm});
            skLineSegment(sketch, "E6.6.0.2", {"start": v(79.4, 14) * mm, "end": v(79.4, 6) * mm});
            skLineSegment(sketch, "E6.6.0.3", {"start": v(71.4, 6) * mm, "end": v(79.4, 6) * mm});
            skLineSegment(sketch, "E6.6.1.0", {"start": v(71.4, 25) * mm, "end": v(79.4, 25) * mm});
            skLineSegment(sketch, "E6.6.1.1", {"start": v(71.4, 25) * mm, "end": v(71.4, 17) * mm});
            skLineSegment(sketch, "E6.6.1.2", {"start": v(79.4, 25) * mm, "end": v(79.4, 17) * mm});
            skLineSegment(sketch, "E6.6.1.3", {"start": v(71.4, 17) * mm, "end": v(79.4, 17) * mm});
            skLineSegment(sketch, "E6.6.2.0", {"start": v(71.4, 36) * mm, "end": v(79.4, 36) * mm});
            skLineSegment(sketch, "E6.6.2.1", {"start": v(71.4, 36) * mm, "end": v(71.4, 28) * mm});
            skLineSegment(sketch, "E6.6.2.2", {"start": v(79.4, 36) * mm, "end": v(79.4, 28) * mm});
            skLineSegment(sketch, "E6.6.2.3", {"start": v(71.4, 28) * mm, "end": v(79.4, 28) * mm});
            skLineSegment(sketch, "E6.6.3.0", {"start": v(71.4, 47) * mm, "end": v(79.4, 47) * mm});
            skLineSegment(sketch, "E6.6.3.1", {"start": v(71.4, 47) * mm, "end": v(71.4, 39) * mm});
            skLineSegment(sketch, "E6.6.3.2", {"start": v(79.4, 47) * mm, "end": v(79.4, 39) * mm});
            skLineSegment(sketch, "E6.6.3.3", {"start": v(71.4, 39) * mm, "end": v(79.4, 39) * mm});
            skLineSegment(sketch, "E6.6.4.0", {"start": v(71.4, 58) * mm, "end": v(79.4, 58) * mm});
            skLineSegment(sketch, "E6.6.4.1", {"start": v(71.4, 58) * mm, "end": v(71.4, 50) * mm});
            skLineSegment(sketch, "E6.6.4.2", {"start": v(79.4, 58) * mm, "end": v(79.4, 50) * mm});
            skLineSegment(sketch, "E6.6.4.3", {"start": v(71.4, 50) * mm, "end": v(79.4, 50) * mm});
            skLineSegment(sketch, "E6.6.5.0", {"start": v(71.4, 69) * mm, "end": v(79.4, 69) * mm});
            skLineSegment(sketch, "E6.6.5.1", {"start": v(71.4, 69) * mm, "end": v(71.4, 61) * mm});
            skLineSegment(sketch, "E6.6.5.2", {"start": v(79.4, 69) * mm, "end": v(79.4, 61) * mm});
            skLineSegment(sketch, "E6.6.5.3", {"start": v(71.4, 61) * mm, "end": v(79.4, 61) * mm});
            skLineSegment(sketch, "E6.6.6.0", {"start": v(71.4, 80) * mm, "end": v(79.4, 80) * mm});
            skLineSegment(sketch, "E6.6.6.1", {"start": v(71.4, 80) * mm, "end": v(71.4, 72) * mm});
            skLineSegment(sketch, "E6.6.6.2", {"start": v(79.4, 80) * mm, "end": v(79.4, 72) * mm});
            skLineSegment(sketch, "E6.6.6.3", {"start": v(71.4, 72) * mm, "end": v(79.4, 72) * mm});
            skLineSegment(sketch, "E6.6.7.0", {"start": v(71.4, 91) * mm, "end": v(79.4, 91) * mm});
            skLineSegment(sketch, "E6.6.7.1", {"start": v(71.4, 91) * mm, "end": v(71.4, 83) * mm});
            skLineSegment(sketch, "E6.6.7.2", {"start": v(79.4, 91) * mm, "end": v(79.4, 83) * mm});
            skLineSegment(sketch, "E6.6.7.3", {"start": v(71.4, 83) * mm, "end": v(79.4, 83) * mm});
            skLineSegment(sketch, "E6.6.8.0", {"start": v(71.4, 102) * mm, "end": v(79.4, 102) * mm});
            skLineSegment(sketch, "E6.6.8.1", {"start": v(71.4, 102) * mm, "end": v(71.4, 94) * mm});
            skLineSegment(sketch, "E6.6.8.2", {"start": v(79.4, 102) * mm, "end": v(79.4, 94) * mm});
            skLineSegment(sketch, "E6.6.8.3", {"start": v(71.4, 94) * mm, "end": v(79.4, 94) * mm});
            skLineSegment(sketch, "E6.6.9.0", {"start": v(71.4, 113) * mm, "end": v(79.4, 113) * mm});
            skLineSegment(sketch, "E6.6.9.1", {"start": v(71.4, 113) * mm, "end": v(71.4, 105) * mm});
            skLineSegment(sketch, "E6.6.9.2", {"start": v(79.4, 113) * mm, "end": v(79.4, 105) * mm});
            skLineSegment(sketch, "E6.6.9.3", {"start": v(71.4, 105) * mm, "end": v(79.4, 105) * mm});
            skLineSegment(sketch, "E6.6.10.0", {"start": v(71.4, 124) * mm, "end": v(79.4, 124) * mm});
            skLineSegment(sketch, "E6.6.10.1", {"start": v(71.4, 124) * mm, "end": v(71.4, 116) * mm});
            skLineSegment(sketch, "E6.6.10.2", {"start": v(79.4, 124) * mm, "end": v(79.4, 116) * mm});
            skLineSegment(sketch, "E6.6.10.3", {"start": v(71.4, 116) * mm, "end": v(79.4, 116) * mm});
            skLineSegment(sketch, "E6.7.0.0", {"start": v(82.3, 14) * mm, "end": v(90.3, 14) * mm});
            skLineSegment(sketch, "E6.7.0.1", {"start": v(82.3, 14) * mm, "end": v(82.3, 6) * mm});
            skLineSegment(sketch, "E6.7.0.2", {"start": v(90.3, 14) * mm, "end": v(90.3, 6) * mm});
            skLineSegment(sketch, "E6.7.0.3", {"start": v(82.3, 6) * mm, "end": v(90.3, 6) * mm});
            skLineSegment(sketch, "E6.7.1.0", {"start": v(82.3, 25) * mm, "end": v(90.3, 25) * mm});
            skLineSegment(sketch, "E6.7.1.1", {"start": v(82.3, 25) * mm, "end": v(82.3, 17) * mm});
            skLineSegment(sketch, "E6.7.1.2", {"start": v(90.3, 25) * mm, "end": v(90.3, 17) * mm});
            skLineSegment(sketch, "E6.7.1.3", {"start": v(82.3, 17) * mm, "end": v(90.3, 17) * mm});
            skLineSegment(sketch, "E6.7.2.0", {"start": v(82.3, 36) * mm, "end": v(90.3, 36) * mm});
            skLineSegment(sketch, "E6.7.2.1", {"start": v(82.3, 36) * mm, "end": v(82.3, 28) * mm});
            skLineSegment(sketch, "E6.7.2.2", {"start": v(90.3, 36) * mm, "end": v(90.3, 28) * mm});
            skLineSegment(sketch, "E6.7.2.3", {"start": v(82.3, 28) * mm, "end": v(90.3, 28) * mm});
            skLineSegment(sketch, "E6.7.3.0", {"start": v(82.3, 47) * mm, "end": v(90.3, 47) * mm});
            skLineSegment(sketch, "E6.7.3.1", {"start": v(82.3, 47) * mm, "end": v(82.3, 39) * mm});
            skLineSegment(sketch, "E6.7.3.2", {"start": v(90.3, 47) * mm, "end": v(90.3, 39) * mm});
            skLineSegment(sketch, "E6.7.3.3", {"start": v(82.3, 39) * mm, "end": v(90.3, 39) * mm});
            skLineSegment(sketch, "E6.7.4.0", {"start": v(82.3, 58) * mm, "end": v(90.3, 58) * mm});
            skLineSegment(sketch, "E6.7.4.1", {"start": v(82.3, 58) * mm, "end": v(82.3, 50) * mm});
            skLineSegment(sketch, "E6.7.4.2", {"start": v(90.3, 58) * mm, "end": v(90.3, 50) * mm});
            skLineSegment(sketch, "E6.7.4.3", {"start": v(82.3, 50) * mm, "end": v(90.3, 50) * mm});
            skLineSegment(sketch, "E6.7.5.0", {"start": v(82.3, 69) * mm, "end": v(90.3, 69) * mm});
            skLineSegment(sketch, "E6.7.5.1", {"start": v(82.3, 69) * mm, "end": v(82.3, 61) * mm});
            skLineSegment(sketch, "E6.7.5.2", {"start": v(90.3, 69) * mm, "end": v(90.3, 61) * mm});
            skLineSegment(sketch, "E6.7.5.3", {"start": v(82.3, 61) * mm, "end": v(90.3, 61) * mm});
            skLineSegment(sketch, "E6.7.6.0", {"start": v(82.3, 80) * mm, "end": v(90.3, 80) * mm});
            skLineSegment(sketch, "E6.7.6.1", {"start": v(82.3, 80) * mm, "end": v(82.3, 72) * mm});
            skLineSegment(sketch, "E6.7.6.2", {"start": v(90.3, 80) * mm, "end": v(90.3, 72) * mm});
            skLineSegment(sketch, "E6.7.6.3", {"start": v(82.3, 72) * mm, "end": v(90.3, 72) * mm});
            skLineSegment(sketch, "E6.7.7.0", {"start": v(82.3, 91) * mm, "end": v(90.3, 91) * mm});
            skLineSegment(sketch, "E6.7.7.1", {"start": v(82.3, 91) * mm, "end": v(82.3, 83) * mm});
            skLineSegment(sketch, "E6.7.7.2", {"start": v(90.3, 91) * mm, "end": v(90.3, 83) * mm});
            skLineSegment(sketch, "E6.7.7.3", {"start": v(82.3, 83) * mm, "end": v(90.3, 83) * mm});
            skLineSegment(sketch, "E6.7.8.0", {"start": v(82.3, 102) * mm, "end": v(90.3, 102) * mm});
            skLineSegment(sketch, "E6.7.8.1", {"start": v(82.3, 102) * mm, "end": v(82.3, 94) * mm});
            skLineSegment(sketch, "E6.7.8.2", {"start": v(90.3, 102) * mm, "end": v(90.3, 94) * mm});
            skLineSegment(sketch, "E6.7.8.3", {"start": v(82.3, 94) * mm, "end": v(90.3, 94) * mm});
            skLineSegment(sketch, "E6.7.9.0", {"start": v(82.3, 113) * mm, "end": v(90.3, 113) * mm});
            skLineSegment(sketch, "E6.7.9.1", {"start": v(82.3, 113) * mm, "end": v(82.3, 105) * mm});
            skLineSegment(sketch, "E6.7.9.2", {"start": v(90.3, 113) * mm, "end": v(90.3, 105) * mm});
            skLineSegment(sketch, "E6.7.9.3", {"start": v(82.3, 105) * mm, "end": v(90.3, 105) * mm});
            skLineSegment(sketch, "E6.7.10.0", {"start": v(82.3, 124) * mm, "end": v(90.3, 124) * mm});
            skLineSegment(sketch, "E6.7.10.1", {"start": v(82.3, 124) * mm, "end": v(82.3, 116) * mm});
            skLineSegment(sketch, "E6.7.10.2", {"start": v(90.3, 124) * mm, "end": v(90.3, 116) * mm});
            skLineSegment(sketch, "E6.7.10.3", {"start": v(82.3, 116) * mm, "end": v(90.3, 116) * mm});
            skLineSegment(sketch, "E6.8.0.0", {"start": v(93.2, 14) * mm, "end": v(101.2, 14) * mm});
            skLineSegment(sketch, "E6.8.0.1", {"start": v(93.2, 14) * mm, "end": v(93.2, 6) * mm});
            skLineSegment(sketch, "E6.8.0.2", {"start": v(101.2, 14) * mm, "end": v(101.2, 6) * mm});
            skLineSegment(sketch, "E6.8.0.3", {"start": v(93.2, 6) * mm, "end": v(101.2, 6) * mm});
            skLineSegment(sketch, "E6.8.1.0", {"start": v(93.2, 25) * mm, "end": v(101.2, 25) * mm});
            skLineSegment(sketch, "E6.8.1.1", {"start": v(93.2, 25) * mm, "end": v(93.2, 17) * mm});
            skLineSegment(sketch, "E6.8.1.2", {"start": v(101.2, 25) * mm, "end": v(101.2, 17) * mm});
            skLineSegment(sketch, "E6.8.1.3", {"start": v(93.2, 17) * mm, "end": v(101.2, 17) * mm});
            skLineSegment(sketch, "E6.8.2.0", {"start": v(93.2, 36) * mm, "end": v(101.2, 36) * mm});
            skLineSegment(sketch, "E6.8.2.1", {"start": v(93.2, 36) * mm, "end": v(93.2, 28) * mm});
            skLineSegment(sketch, "E6.8.2.2", {"start": v(101.2, 36) * mm, "end": v(101.2, 28) * mm});
            skLineSegment(sketch, "E6.8.2.3", {"start": v(93.2, 28) * mm, "end": v(101.2, 28) * mm});
            skLineSegment(sketch, "E6.8.3.0", {"start": v(93.2, 47) * mm, "end": v(101.2, 47) * mm});
            skLineSegment(sketch, "E6.8.3.1", {"start": v(93.2, 47) * mm, "end": v(93.2, 39) * mm});
            skLineSegment(sketch, "E6.8.3.2", {"start": v(101.2, 47) * mm, "end": v(101.2, 39) * mm});
            skLineSegment(sketch, "E6.8.3.3", {"start": v(93.2, 39) * mm, "end": v(101.2, 39) * mm});
            skLineSegment(sketch, "E6.8.4.0", {"start": v(93.2, 58) * mm, "end": v(101.2, 58) * mm});
            skLineSegment(sketch, "E6.8.4.1", {"start": v(93.2, 58) * mm, "end": v(93.2, 50) * mm});
            skLineSegment(sketch, "E6.8.4.2", {"start": v(101.2, 58) * mm, "end": v(101.2, 50) * mm});
            skLineSegment(sketch, "E6.8.4.3", {"start": v(93.2, 50) * mm, "end": v(101.2, 50) * mm});
            skLineSegment(sketch, "E6.8.5.0", {"start": v(93.2, 69) * mm, "end": v(101.2, 69) * mm});
            skLineSegment(sketch, "E6.8.5.1", {"start": v(93.2, 69) * mm, "end": v(93.2, 61) * mm});
            skLineSegment(sketch, "E6.8.5.2", {"start": v(101.2, 69) * mm, "end": v(101.2, 61) * mm});
            skLineSegment(sketch, "E6.8.5.3", {"start": v(93.2, 61) * mm, "end": v(101.2, 61) * mm});
            skLineSegment(sketch, "E6.8.6.0", {"start": v(93.2, 80) * mm, "end": v(101.2, 80) * mm});
            skLineSegment(sketch, "E6.8.6.1", {"start": v(93.2, 80) * mm, "end": v(93.2, 72) * mm});
            skLineSegment(sketch, "E6.8.6.2", {"start": v(101.2, 80) * mm, "end": v(101.2, 72) * mm});
            skLineSegment(sketch, "E6.8.6.3", {"start": v(93.2, 72) * mm, "end": v(101.2, 72) * mm});
            skLineSegment(sketch, "E6.8.7.0", {"start": v(93.2, 91) * mm, "end": v(101.2, 91) * mm});
            skLineSegment(sketch, "E6.8.7.1", {"start": v(93.2, 91) * mm, "end": v(93.2, 83) * mm});
            skLineSegment(sketch, "E6.8.7.2", {"start": v(101.2, 91) * mm, "end": v(101.2, 83) * mm});
            skLineSegment(sketch, "E6.8.7.3", {"start": v(93.2, 83) * mm, "end": v(101.2, 83) * mm});
            skLineSegment(sketch, "E6.8.8.0", {"start": v(93.2, 102) * mm, "end": v(101.2, 102) * mm});
            skLineSegment(sketch, "E6.8.8.1", {"start": v(93.2, 102) * mm, "end": v(93.2, 94) * mm});
            skLineSegment(sketch, "E6.8.8.2", {"start": v(101.2, 102) * mm, "end": v(101.2, 94) * mm});
            skLineSegment(sketch, "E6.8.8.3", {"start": v(93.2, 94) * mm, "end": v(101.2, 94) * mm});
            skLineSegment(sketch, "E6.8.9.0", {"start": v(93.2, 113) * mm, "end": v(101.2, 113) * mm});
            skLineSegment(sketch, "E6.8.9.1", {"start": v(93.2, 113) * mm, "end": v(93.2, 105) * mm});
            skLineSegment(sketch, "E6.8.9.2", {"start": v(101.2, 113) * mm, "end": v(101.2, 105) * mm});
            skLineSegment(sketch, "E6.8.9.3", {"start": v(93.2, 105) * mm, "end": v(101.2, 105) * mm});
            skLineSegment(sketch, "E6.8.10.0", {"start": v(93.2, 124) * mm, "end": v(101.2, 124) * mm});
            skLineSegment(sketch, "E6.8.10.1", {"start": v(93.2, 124) * mm, "end": v(93.2, 116) * mm});
            skLineSegment(sketch, "E6.8.10.2", {"start": v(101.2, 124) * mm, "end": v(101.2, 116) * mm});
            skLineSegment(sketch, "E6.8.10.3", {"start": v(93.2, 116) * mm, "end": v(101.2, 116) * mm});
            skLineSegment(sketch, "E6.9.0.0", {"start": v(104.1, 14) * mm, "end": v(112.1, 14) * mm});
            skLineSegment(sketch, "E6.9.0.1", {"start": v(104.1, 14) * mm, "end": v(104.1, 6) * mm});
            skLineSegment(sketch, "E6.9.0.2", {"start": v(112.1, 14) * mm, "end": v(112.1, 6) * mm});
            skLineSegment(sketch, "E6.9.0.3", {"start": v(104.1, 6) * mm, "end": v(112.1, 6) * mm});
            skLineSegment(sketch, "E6.9.1.0", {"start": v(104.1, 25) * mm, "end": v(112.1, 25) * mm});
            skLineSegment(sketch, "E6.9.1.1", {"start": v(104.1, 25) * mm, "end": v(104.1, 17) * mm});
            skLineSegment(sketch, "E6.9.1.2", {"start": v(112.1, 25) * mm, "end": v(112.1, 17) * mm});
            skLineSegment(sketch, "E6.9.1.3", {"start": v(104.1, 17) * mm, "end": v(112.1, 17) * mm});
            skLineSegment(sketch, "E6.9.2.0", {"start": v(104.1, 36) * mm, "end": v(112.1, 36) * mm});
            skLineSegment(sketch, "E6.9.2.1", {"start": v(104.1, 36) * mm, "end": v(104.1, 28) * mm});
            skLineSegment(sketch, "E6.9.2.2", {"start": v(112.1, 36) * mm, "end": v(112.1, 28) * mm});
            skLineSegment(sketch, "E6.9.2.3", {"start": v(104.1, 28) * mm, "end": v(112.1, 28) * mm});
            skLineSegment(sketch, "E6.9.3.0", {"start": v(104.1, 47) * mm, "end": v(112.1, 47) * mm});
            skLineSegment(sketch, "E6.9.3.1", {"start": v(104.1, 47) * mm, "end": v(104.1, 39) * mm});
            skLineSegment(sketch, "E6.9.3.2", {"start": v(112.1, 47) * mm, "end": v(112.1, 39) * mm});
            skLineSegment(sketch, "E6.9.3.3", {"start": v(104.1, 39) * mm, "end": v(112.1, 39) * mm});
            skLineSegment(sketch, "E6.9.4.0", {"start": v(104.1, 58) * mm, "end": v(112.1, 58) * mm});
            skLineSegment(sketch, "E6.9.4.1", {"start": v(104.1, 58) * mm, "end": v(104.1, 50) * mm});
            skLineSegment(sketch, "E6.9.4.2", {"start": v(112.1, 58) * mm, "end": v(112.1, 50) * mm});
            skLineSegment(sketch, "E6.9.4.3", {"start": v(104.1, 50) * mm, "end": v(112.1, 50) * mm});
            skLineSegment(sketch, "E6.9.5.0", {"start": v(104.1, 69) * mm, "end": v(112.1, 69) * mm});
            skLineSegment(sketch, "E6.9.5.1", {"start": v(104.1, 69) * mm, "end": v(104.1, 61) * mm});
            skLineSegment(sketch, "E6.9.5.2", {"start": v(112.1, 69) * mm, "end": v(112.1, 61) * mm});
            skLineSegment(sketch, "E6.9.5.3", {"start": v(104.1, 61) * mm, "end": v(112.1, 61) * mm});
            skLineSegment(sketch, "E6.9.6.0", {"start": v(104.1, 80) * mm, "end": v(112.1, 80) * mm});
            skLineSegment(sketch, "E6.9.6.1", {"start": v(104.1, 80) * mm, "end": v(104.1, 72) * mm});
            skLineSegment(sketch, "E6.9.6.2", {"start": v(112.1, 80) * mm, "end": v(112.1, 72) * mm});
            skLineSegment(sketch, "E6.9.6.3", {"start": v(104.1, 72) * mm, "end": v(112.1, 72) * mm});
            skLineSegment(sketch, "E6.9.7.0", {"start": v(104.1, 91) * mm, "end": v(112.1, 91) * mm});
            skLineSegment(sketch, "E6.9.7.1", {"start": v(104.1, 91) * mm, "end": v(104.1, 83) * mm});
            skLineSegment(sketch, "E6.9.7.2", {"start": v(112.1, 91) * mm, "end": v(112.1, 83) * mm});
            skLineSegment(sketch, "E6.9.7.3", {"start": v(104.1, 83) * mm, "end": v(112.1, 83) * mm});
            skLineSegment(sketch, "E6.9.8.0", {"start": v(104.1, 102) * mm, "end": v(112.1, 102) * mm});
            skLineSegment(sketch, "E6.9.8.1", {"start": v(104.1, 102) * mm, "end": v(104.1, 94) * mm});
            skLineSegment(sketch, "E6.9.8.2", {"start": v(112.1, 102) * mm, "end": v(112.1, 94) * mm});
            skLineSegment(sketch, "E6.9.8.3", {"start": v(104.1, 94) * mm, "end": v(112.1, 94) * mm});
            skLineSegment(sketch, "E6.9.9.0", {"start": v(104.1, 113) * mm, "end": v(112.1, 113) * mm});
            skLineSegment(sketch, "E6.9.9.1", {"start": v(104.1, 113) * mm, "end": v(104.1, 105) * mm});
            skLineSegment(sketch, "E6.9.9.2", {"start": v(112.1, 113) * mm, "end": v(112.1, 105) * mm});
            skLineSegment(sketch, "E6.9.9.3", {"start": v(104.1, 105) * mm, "end": v(112.1, 105) * mm});
            skLineSegment(sketch, "E6.9.10.0", {"start": v(104.1, 124) * mm, "end": v(112.1, 124) * mm});
            skLineSegment(sketch, "E6.9.10.1", {"start": v(104.1, 124) * mm, "end": v(104.1, 116) * mm});
            skLineSegment(sketch, "E6.9.10.2", {"start": v(112.1, 124) * mm, "end": v(112.1, 116) * mm});
            skLineSegment(sketch, "E6.9.10.3", {"start": v(104.1, 116) * mm, "end": v(112.1, 116) * mm});
            skLineSegment(sketch, "E6.10.0.0", {"start": v(115, 14) * mm, "end": v(123, 14) * mm});
            skLineSegment(sketch, "E6.10.0.1", {"start": v(115, 14) * mm, "end": v(115, 6) * mm});
            skLineSegment(sketch, "E6.10.0.2", {"start": v(123, 14) * mm, "end": v(123, 6) * mm});
            skLineSegment(sketch, "E6.10.0.3", {"start": v(115, 6) * mm, "end": v(123, 6) * mm});
            skLineSegment(sketch, "E6.10.1.0", {"start": v(115, 25) * mm, "end": v(123, 25) * mm});
            skLineSegment(sketch, "E6.10.1.1", {"start": v(115, 25) * mm, "end": v(115, 17) * mm});
            skLineSegment(sketch, "E6.10.1.2", {"start": v(123, 25) * mm, "end": v(123, 17) * mm});
            skLineSegment(sketch, "E6.10.1.3", {"start": v(115, 17) * mm, "end": v(123, 17) * mm});
            skLineSegment(sketch, "E6.10.2.0", {"start": v(115, 36) * mm, "end": v(123, 36) * mm});
            skLineSegment(sketch, "E6.10.2.1", {"start": v(115, 36) * mm, "end": v(115, 28) * mm});
            skLineSegment(sketch, "E6.10.2.2", {"start": v(123, 36) * mm, "end": v(123, 28) * mm});
            skLineSegment(sketch, "E6.10.2.3", {"start": v(115, 28) * mm, "end": v(123, 28) * mm});
            skLineSegment(sketch, "E6.10.3.0", {"start": v(115, 47) * mm, "end": v(123, 47) * mm});
            skLineSegment(sketch, "E6.10.3.1", {"start": v(115, 47) * mm, "end": v(115, 39) * mm});
            skLineSegment(sketch, "E6.10.3.2", {"start": v(123, 47) * mm, "end": v(123, 39) * mm});
            skLineSegment(sketch, "E6.10.3.3", {"start": v(115, 39) * mm, "end": v(123, 39) * mm});
            skLineSegment(sketch, "E6.10.4.0", {"start": v(115, 58) * mm, "end": v(123, 58) * mm});
            skLineSegment(sketch, "E6.10.4.1", {"start": v(115, 58) * mm, "end": v(115, 50) * mm});
            skLineSegment(sketch, "E6.10.4.2", {"start": v(123, 58) * mm, "end": v(123, 50) * mm});
            skLineSegment(sketch, "E6.10.4.3", {"start": v(115, 50) * mm, "end": v(123, 50) * mm});
            skLineSegment(sketch, "E6.10.5.0", {"start": v(115, 69) * mm, "end": v(123, 69) * mm});
            skLineSegment(sketch, "E6.10.5.1", {"start": v(115, 69) * mm, "end": v(115, 61) * mm});
            skLineSegment(sketch, "E6.10.5.2", {"start": v(123, 69) * mm, "end": v(123, 61) * mm});
            skLineSegment(sketch, "E6.10.5.3", {"start": v(115, 61) * mm, "end": v(123, 61) * mm});
            skLineSegment(sketch, "E6.10.6.0", {"start": v(115, 80) * mm, "end": v(123, 80) * mm});
            skLineSegment(sketch, "E6.10.6.1", {"start": v(115, 80) * mm, "end": v(115, 72) * mm});
            skLineSegment(sketch, "E6.10.6.2", {"start": v(123, 80) * mm, "end": v(123, 72) * mm});
            skLineSegment(sketch, "E6.10.6.3", {"start": v(115, 72) * mm, "end": v(123, 72) * mm});
            skLineSegment(sketch, "E6.10.7.0", {"start": v(115, 91) * mm, "end": v(123, 91) * mm});
            skLineSegment(sketch, "E6.10.7.1", {"start": v(115, 91) * mm, "end": v(115, 83) * mm});
            skLineSegment(sketch, "E6.10.7.2", {"start": v(123, 91) * mm, "end": v(123, 83) * mm});
            skLineSegment(sketch, "E6.10.7.3", {"start": v(115, 83) * mm, "end": v(123, 83) * mm});
            skLineSegment(sketch, "E6.10.8.0", {"start": v(115, 102) * mm, "end": v(123, 102) * mm});
            skLineSegment(sketch, "E6.10.8.1", {"start": v(115, 102) * mm, "end": v(115, 94) * mm});
            skLineSegment(sketch, "E6.10.8.2", {"start": v(123, 102) * mm, "end": v(123, 94) * mm});
            skLineSegment(sketch, "E6.10.8.3", {"start": v(115, 94) * mm, "end": v(123, 94) * mm});
            skLineSegment(sketch, "E6.10.9.0", {"start": v(115, 113) * mm, "end": v(123, 113) * mm});
            skLineSegment(sketch, "E6.10.9.1", {"start": v(115, 113) * mm, "end": v(115, 105) * mm});
            skLineSegment(sketch, "E6.10.9.2", {"start": v(123, 113) * mm, "end": v(123, 105) * mm});
            skLineSegment(sketch, "E6.10.9.3", {"start": v(115, 105) * mm, "end": v(123, 105) * mm});
            skLineSegment(sketch, "E6.10.10.0", {"start": v(115, 124) * mm, "end": v(123, 124) * mm});
            skLineSegment(sketch, "E6.10.10.1", {"start": v(115, 124) * mm, "end": v(115, 116) * mm});
            skLineSegment(sketch, "E6.10.10.2", {"start": v(123, 124) * mm, "end": v(123, 116) * mm});
            skLineSegment(sketch, "E6.10.10.3", {"start": v(115, 116) * mm, "end": v(123, 116) * mm});
            skLineSegment(sketch, "E6.11.0.0", {"start": v(125.9, 14) * mm, "end": v(133.9, 14) * mm});
            skLineSegment(sketch, "E6.11.0.1", {"start": v(125.9, 14) * mm, "end": v(125.9, 6) * mm});
            skLineSegment(sketch, "E6.11.0.2", {"start": v(133.9, 14) * mm, "end": v(133.9, 6) * mm});
            skLineSegment(sketch, "E6.11.0.3", {"start": v(125.9, 6) * mm, "end": v(133.9, 6) * mm});
            skLineSegment(sketch, "E6.11.1.0", {"start": v(125.9, 25) * mm, "end": v(133.9, 25) * mm});
            skLineSegment(sketch, "E6.11.1.1", {"start": v(125.9, 25) * mm, "end": v(125.9, 17) * mm});
            skLineSegment(sketch, "E6.11.1.2", {"start": v(133.9, 25) * mm, "end": v(133.9, 17) * mm});
            skLineSegment(sketch, "E6.11.1.3", {"start": v(125.9, 17) * mm, "end": v(133.9, 17) * mm});
            skLineSegment(sketch, "E6.11.2.0", {"start": v(125.9, 36) * mm, "end": v(133.9, 36) * mm});
            skLineSegment(sketch, "E6.11.2.1", {"start": v(125.9, 36) * mm, "end": v(125.9, 28) * mm});
            skLineSegment(sketch, "E6.11.2.2", {"start": v(133.9, 36) * mm, "end": v(133.9, 28) * mm});
            skLineSegment(sketch, "E6.11.2.3", {"start": v(125.9, 28) * mm, "end": v(133.9, 28) * mm});
            skLineSegment(sketch, "E6.11.3.0", {"start": v(125.9, 47) * mm, "end": v(133.9, 47) * mm});
            skLineSegment(sketch, "E6.11.3.1", {"start": v(125.9, 47) * mm, "end": v(125.9, 39) * mm});
            skLineSegment(sketch, "E6.11.3.2", {"start": v(133.9, 47) * mm, "end": v(133.9, 39) * mm});
            skLineSegment(sketch, "E6.11.3.3", {"start": v(125.9, 39) * mm, "end": v(133.9, 39) * mm});
            skLineSegment(sketch, "E6.11.4.0", {"start": v(125.9, 58) * mm, "end": v(133.9, 58) * mm});
            skLineSegment(sketch, "E6.11.4.1", {"start": v(125.9, 58) * mm, "end": v(125.9, 50) * mm});
            skLineSegment(sketch, "E6.11.4.2", {"start": v(133.9, 58) * mm, "end": v(133.9, 50) * mm});
            skLineSegment(sketch, "E6.11.4.3", {"start": v(125.9, 50) * mm, "end": v(133.9, 50) * mm});
            skLineSegment(sketch, "E6.11.5.0", {"start": v(125.9, 69) * mm, "end": v(133.9, 69) * mm});
            skLineSegment(sketch, "E6.11.5.1", {"start": v(125.9, 69) * mm, "end": v(125.9, 61) * mm});
            skLineSegment(sketch, "E6.11.5.2", {"start": v(133.9, 69) * mm, "end": v(133.9, 61) * mm});
            skLineSegment(sketch, "E6.11.5.3", {"start": v(125.9, 61) * mm, "end": v(133.9, 61) * mm});
            skLineSegment(sketch, "E6.11.6.0", {"start": v(125.9, 80) * mm, "end": v(133.9, 80) * mm});
            skLineSegment(sketch, "E6.11.6.1", {"start": v(125.9, 80) * mm, "end": v(125.9, 72) * mm});
            skLineSegment(sketch, "E6.11.6.2", {"start": v(133.9, 80) * mm, "end": v(133.9, 72) * mm});
            skLineSegment(sketch, "E6.11.6.3", {"start": v(125.9, 72) * mm, "end": v(133.9, 72) * mm});
            skLineSegment(sketch, "E6.11.7.0", {"start": v(125.9, 91) * mm, "end": v(133.9, 91) * mm});
            skLineSegment(sketch, "E6.11.7.1", {"start": v(125.9, 91) * mm, "end": v(125.9, 83) * mm});
            skLineSegment(sketch, "E6.11.7.2", {"start": v(133.9, 91) * mm, "end": v(133.9, 83) * mm});
            skLineSegment(sketch, "E6.11.7.3", {"start": v(125.9, 83) * mm, "end": v(133.9, 83) * mm});
            skLineSegment(sketch, "E6.11.8.0", {"start": v(125.9, 102) * mm, "end": v(133.9, 102) * mm});
            skLineSegment(sketch, "E6.11.8.1", {"start": v(125.9, 102) * mm, "end": v(125.9, 94) * mm});
            skLineSegment(sketch, "E6.11.8.2", {"start": v(133.9, 102) * mm, "end": v(133.9, 94) * mm});
            skLineSegment(sketch, "E6.11.8.3", {"start": v(125.9, 94) * mm, "end": v(133.9, 94) * mm});
            skLineSegment(sketch, "E6.11.9.0", {"start": v(125.9, 113) * mm, "end": v(133.9, 113) * mm});
            skLineSegment(sketch, "E6.11.9.1", {"start": v(125.9, 113) * mm, "end": v(125.9, 105) * mm});
            skLineSegment(sketch, "E6.11.9.2", {"start": v(133.9, 113) * mm, "end": v(133.9, 105) * mm});
            skLineSegment(sketch, "E6.11.9.3", {"start": v(125.9, 105) * mm, "end": v(133.9, 105) * mm});
            skLineSegment(sketch, "E6.11.10.0", {"start": v(125.9, 124) * mm, "end": v(133.9, 124) * mm});
            skLineSegment(sketch, "E6.11.10.1", {"start": v(125.9, 124) * mm, "end": v(125.9, 116) * mm});
            skLineSegment(sketch, "E6.11.10.2", {"start": v(133.9, 124) * mm, "end": v(133.9, 116) * mm});
            skLineSegment(sketch, "E6.11.10.3", {"start": v(125.9, 116) * mm, "end": v(133.9, 116) * mm});
            skLineSegment(sketch, "E6.direction1", {"start": v(6, 6) * mm, "end": v(16.9, 6) * mm, "construction": true});
            skLineSegment(sketch, "E6.direction2", {"start": v(6, 6) * mm, "end": v(6, 17) * mm, "construction": true});
            skLineSegment(sketch, "E7", {"start": v(134, 0) * mm, "end": v(134, 49.45) * mm, "construction": true});
            skSolve(sketch);
        }
        {
            var Q0;
            Q0 = qSketchRegion(id + "F5", true);
            extrude(context, id + "F6", {"entities" : qUnion([Q0]), "operationType" : NewBodyOperationType.REMOVE, "oppositeDirection" : true, "depth" : 170 * mm, "offsetDistance" : 25 * mm});
        }
        {
            var Q0;
            Q0=makeQuery(id+"F1.opExtrude","SWEPT_FACE",FACE,{"disambiguationData":[OSD([sQuery(id+"F0.wireOp",EDGE,"E0.bottom")])]});
            var sketch = newSketch(context, id + "F7", { "sketchPlane" : qUnion([Q0])});
            skLineSegment(sketch, "E8.bottom", {"start": v(6, 14) * mm, "end": v(14, 14) * mm});
            skLineSegment(sketch, "E8.top", {"start": v(6, 6) * mm, "end": v(14, 6) * mm});
            skLineSegment(sketch, "E8.left", {"start": v(6, 14) * mm, "end": v(6, 6) * mm});
            skLineSegment(sketch, "E8.right", {"start": v(14, 14) * mm, "end": v(14, 6) * mm});
            skLineSegment(sketch, "E9.0.1.0", {"start": v(6, 25) * mm, "end": v(6, 17) * mm});
            skLineSegment(sketch, "E9.0.1.1", {"start": v(14, 25) * mm, "end": v(14, 17) * mm});
            skLineSegment(sketch, "E9.0.1.2", {"start": v(6, 25) * mm, "end": v(14, 25) * mm});
            skLineSegment(sketch, "E9.0.1.3", {"start": v(6, 17) * mm, "end": v(14, 17) * mm});
            skLineSegment(sketch, "E9.0.2.0", {"start": v(6, 36) * mm, "end": v(6, 28) * mm});
            skLineSegment(sketch, "E9.0.2.1", {"start": v(14, 36) * mm, "end": v(14, 28) * mm});
            skLineSegment(sketch, "E9.0.2.2", {"start": v(6, 36) * mm, "end": v(14, 36) * mm});
            skLineSegment(sketch, "E9.0.2.3", {"start": v(6, 28) * mm, "end": v(14, 28) * mm});
            skLineSegment(sketch, "E9.0.3.0", {"start": v(6, 47) * mm, "end": v(6, 39) * mm});
            skLineSegment(sketch, "E9.0.3.1", {"start": v(14, 47) * mm, "end": v(14, 39) * mm});
            skLineSegment(sketch, "E9.0.3.2", {"start": v(6, 47) * mm, "end": v(14, 47) * mm});
            skLineSegment(sketch, "E9.0.3.3", {"start": v(6, 39) * mm, "end": v(14, 39) * mm});
            skLineSegment(sketch, "E9.0.4.0", {"start": v(6, 58) * mm, "end": v(6, 50) * mm});
            skLineSegment(sketch, "E9.0.4.1", {"start": v(14, 58) * mm, "end": v(14, 50) * mm});
            skLineSegment(sketch, "E9.0.4.2", {"start": v(6, 58) * mm, "end": v(14, 58) * mm});
            skLineSegment(sketch, "E9.0.4.3", {"start": v(6, 50) * mm, "end": v(14, 50) * mm});
            skLineSegment(sketch, "E9.0.5.0", {"start": v(6, 69) * mm, "end": v(6, 61) * mm});
            skLineSegment(sketch, "E9.0.5.1", {"start": v(14, 69) * mm, "end": v(14, 61) * mm});
            skLineSegment(sketch, "E9.0.5.2", {"start": v(6, 69) * mm, "end": v(14, 69) * mm});
            skLineSegment(sketch, "E9.0.5.3", {"start": v(6, 61) * mm, "end": v(14, 61) * mm});
            skLineSegment(sketch, "E9.0.6.0", {"start": v(6, 80) * mm, "end": v(6, 72) * mm});
            skLineSegment(sketch, "E9.0.6.1", {"start": v(14, 80) * mm, "end": v(14, 72) * mm});
            skLineSegment(sketch, "E9.0.6.2", {"start": v(6, 80) * mm, "end": v(14, 80) * mm});
            skLineSegment(sketch, "E9.0.6.3", {"start": v(6, 72) * mm, "end": v(14, 72) * mm});
            skLineSegment(sketch, "E9.0.7.0", {"start": v(6, 91) * mm, "end": v(6, 83) * mm});
            skLineSegment(sketch, "E9.0.7.1", {"start": v(14, 91) * mm, "end": v(14, 83) * mm});
            skLineSegment(sketch, "E9.0.7.2", {"start": v(6, 91) * mm, "end": v(14, 91) * mm});
            skLineSegment(sketch, "E9.0.7.3", {"start": v(6, 83) * mm, "end": v(14, 83) * mm});
            skLineSegment(sketch, "E9.0.8.0", {"start": v(6, 102) * mm, "end": v(6, 94) * mm});
            skLineSegment(sketch, "E9.0.8.1", {"start": v(14, 102) * mm, "end": v(14, 94) * mm});
            skLineSegment(sketch, "E9.0.8.2", {"start": v(6, 102) * mm, "end": v(14, 102) * mm});
            skLineSegment(sketch, "E9.0.8.3", {"start": v(6, 94) * mm, "end": v(14, 94) * mm});
            skLineSegment(sketch, "E9.0.9.0", {"start": v(6, 113) * mm, "end": v(6, 105) * mm});
            skLineSegment(sketch, "E9.0.9.1", {"start": v(14, 113) * mm, "end": v(14, 105) * mm});
            skLineSegment(sketch, "E9.0.9.2", {"start": v(6, 113) * mm, "end": v(14, 113) * mm});
            skLineSegment(sketch, "E9.0.9.3", {"start": v(6, 105) * mm, "end": v(14, 105) * mm});
            skLineSegment(sketch, "E9.0.10.0", {"start": v(6, 124) * mm, "end": v(6, 116) * mm});
            skLineSegment(sketch, "E9.0.10.1", {"start": v(14, 124) * mm, "end": v(14, 116) * mm});
            skLineSegment(sketch, "E9.0.10.2", {"start": v(6, 124) * mm, "end": v(14, 124) * mm});
            skLineSegment(sketch, "E9.0.10.3", {"start": v(6, 116) * mm, "end": v(14, 116) * mm});
            skLineSegment(sketch, "E9.1.0.0", {"start": v(16.7, 14) * mm, "end": v(16.7, 6) * mm});
            skLineSegment(sketch, "E9.1.0.1", {"start": v(24.7, 14) * mm, "end": v(24.7, 6) * mm});
            skLineSegment(sketch, "E9.1.0.2", {"start": v(16.7, 14) * mm, "end": v(24.7, 14) * mm});
            skLineSegment(sketch, "E9.1.0.3", {"start": v(16.7, 6) * mm, "end": v(24.7, 6) * mm});
            skLineSegment(sketch, "E9.1.1.0", {"start": v(16.7, 25) * mm, "end": v(16.7, 17) * mm});
            skLineSegment(sketch, "E9.1.1.1", {"start": v(24.7, 25) * mm, "end": v(24.7, 17) * mm});
            skLineSegment(sketch, "E9.1.1.2", {"start": v(16.7, 25) * mm, "end": v(24.7, 25) * mm});
            skLineSegment(sketch, "E9.1.1.3", {"start": v(16.7, 17) * mm, "end": v(24.7, 17) * mm});
            skLineSegment(sketch, "E9.1.2.0", {"start": v(16.7, 36) * mm, "end": v(16.7, 28) * mm});
            skLineSegment(sketch, "E9.1.2.1", {"start": v(24.7, 36) * mm, "end": v(24.7, 28) * mm});
            skLineSegment(sketch, "E9.1.2.2", {"start": v(16.7, 36) * mm, "end": v(24.7, 36) * mm});
            skLineSegment(sketch, "E9.1.2.3", {"start": v(16.7, 28) * mm, "end": v(24.7, 28) * mm});
            skLineSegment(sketch, "E9.1.3.0", {"start": v(16.7, 47) * mm, "end": v(16.7, 39) * mm});
            skLineSegment(sketch, "E9.1.3.1", {"start": v(24.7, 47) * mm, "end": v(24.7, 39) * mm});
            skLineSegment(sketch, "E9.1.3.2", {"start": v(16.7, 47) * mm, "end": v(24.7, 47) * mm});
            skLineSegment(sketch, "E9.1.3.3", {"start": v(16.7, 39) * mm, "end": v(24.7, 39) * mm});
            skLineSegment(sketch, "E9.1.4.0", {"start": v(16.7, 58) * mm, "end": v(16.7, 50) * mm});
            skLineSegment(sketch, "E9.1.4.1", {"start": v(24.7, 58) * mm, "end": v(24.7, 50) * mm});
            skLineSegment(sketch, "E9.1.4.2", {"start": v(16.7, 58) * mm, "end": v(24.7, 58) * mm});
            skLineSegment(sketch, "E9.1.4.3", {"start": v(16.7, 50) * mm, "end": v(24.7, 50) * mm});
            skLineSegment(sketch, "E9.1.5.0", {"start": v(16.7, 69) * mm, "end": v(16.7, 61) * mm});
            skLineSegment(sketch, "E9.1.5.1", {"start": v(24.7, 69) * mm, "end": v(24.7, 61) * mm});
            skLineSegment(sketch, "E9.1.5.2", {"start": v(16.7, 69) * mm, "end": v(24.7, 69) * mm});
            skLineSegment(sketch, "E9.1.5.3", {"start": v(16.7, 61) * mm, "end": v(24.7, 61) * mm});
            skLineSegment(sketch, "E9.1.6.0", {"start": v(16.7, 80) * mm, "end": v(16.7, 72) * mm});
            skLineSegment(sketch, "E9.1.6.1", {"start": v(24.7, 80) * mm, "end": v(24.7, 72) * mm});
            skLineSegment(sketch, "E9.1.6.2", {"start": v(16.7, 80) * mm, "end": v(24.7, 80) * mm});
            skLineSegment(sketch, "E9.1.6.3", {"start": v(16.7, 72) * mm, "end": v(24.7, 72) * mm});
            skLineSegment(sketch, "E9.1.7.0", {"start": v(16.7, 91) * mm, "end": v(16.7, 83) * mm});
            skLineSegment(sketch, "E9.1.7.1", {"start": v(24.7, 91) * mm, "end": v(24.7, 83) * mm});
            skLineSegment(sketch, "E9.1.7.2", {"start": v(16.7, 91) * mm, "end": v(24.7, 91) * mm});
            skLineSegment(sketch, "E9.1.7.3", {"start": v(16.7, 83) * mm, "end": v(24.7, 83) * mm});
            skLineSegment(sketch, "E9.1.8.0", {"start": v(16.7, 102) * mm, "end": v(16.7, 94) * mm});
            skLineSegment(sketch, "E9.1.8.1", {"start": v(24.7, 102) * mm, "end": v(24.7, 94) * mm});
            skLineSegment(sketch, "E9.1.8.2", {"start": v(16.7, 102) * mm, "end": v(24.7, 102) * mm});
            skLineSegment(sketch, "E9.1.8.3", {"start": v(16.7, 94) * mm, "end": v(24.7, 94) * mm});
            skLineSegment(sketch, "E9.1.9.0", {"start": v(16.7, 113) * mm, "end": v(16.7, 105) * mm});
            skLineSegment(sketch, "E9.1.9.1", {"start": v(24.7, 113) * mm, "end": v(24.7, 105) * mm});
            skLineSegment(sketch, "E9.1.9.2", {"start": v(16.7, 113) * mm, "end": v(24.7, 113) * mm});
            skLineSegment(sketch, "E9.1.9.3", {"start": v(16.7, 105) * mm, "end": v(24.7, 105) * mm});
            skLineSegment(sketch, "E9.1.10.0", {"start": v(16.7, 124) * mm, "end": v(16.7, 116) * mm});
            skLineSegment(sketch, "E9.1.10.1", {"start": v(24.7, 124) * mm, "end": v(24.7, 116) * mm});
            skLineSegment(sketch, "E9.1.10.2", {"start": v(16.7, 124) * mm, "end": v(24.7, 124) * mm});
            skLineSegment(sketch, "E9.1.10.3", {"start": v(16.7, 116) * mm, "end": v(24.7, 116) * mm});
            skLineSegment(sketch, "E9.2.0.0", {"start": v(27.4, 14) * mm, "end": v(27.4, 6) * mm});
            skLineSegment(sketch, "E9.2.0.1", {"start": v(35.4, 14) * mm, "end": v(35.4, 6) * mm});
            skLineSegment(sketch, "E9.2.0.2", {"start": v(27.4, 14) * mm, "end": v(35.4, 14) * mm});
            skLineSegment(sketch, "E9.2.0.3", {"start": v(27.4, 6) * mm, "end": v(35.4, 6) * mm});
            skLineSegment(sketch, "E9.2.1.0", {"start": v(27.4, 25) * mm, "end": v(27.4, 17) * mm});
            skLineSegment(sketch, "E9.2.1.1", {"start": v(35.4, 25) * mm, "end": v(35.4, 17) * mm});
            skLineSegment(sketch, "E9.2.1.2", {"start": v(27.4, 25) * mm, "end": v(35.4, 25) * mm});
            skLineSegment(sketch, "E9.2.1.3", {"start": v(27.4, 17) * mm, "end": v(35.4, 17) * mm});
            skLineSegment(sketch, "E9.2.2.0", {"start": v(27.4, 36) * mm, "end": v(27.4, 28) * mm});
            skLineSegment(sketch, "E9.2.2.1", {"start": v(35.4, 36) * mm, "end": v(35.4, 28) * mm});
            skLineSegment(sketch, "E9.2.2.2", {"start": v(27.4, 36) * mm, "end": v(35.4, 36) * mm});
            skLineSegment(sketch, "E9.2.2.3", {"start": v(27.4, 28) * mm, "end": v(35.4, 28) * mm});
            skLineSegment(sketch, "E9.2.3.0", {"start": v(27.4, 47) * mm, "end": v(27.4, 39) * mm});
            skLineSegment(sketch, "E9.2.3.1", {"start": v(35.4, 47) * mm, "end": v(35.4, 39) * mm});
            skLineSegment(sketch, "E9.2.3.2", {"start": v(27.4, 47) * mm, "end": v(35.4, 47) * mm});
            skLineSegment(sketch, "E9.2.3.3", {"start": v(27.4, 39) * mm, "end": v(35.4, 39) * mm});
            skLineSegment(sketch, "E9.2.4.0", {"start": v(27.4, 58) * mm, "end": v(27.4, 50) * mm});
            skLineSegment(sketch, "E9.2.4.1", {"start": v(35.4, 58) * mm, "end": v(35.4, 50) * mm});
            skLineSegment(sketch, "E9.2.4.2", {"start": v(27.4, 58) * mm, "end": v(35.4, 58) * mm});
            skLineSegment(sketch, "E9.2.4.3", {"start": v(27.4, 50) * mm, "end": v(35.4, 50) * mm});
            skLineSegment(sketch, "E9.2.5.0", {"start": v(27.4, 69) * mm, "end": v(27.4, 61) * mm});
            skLineSegment(sketch, "E9.2.5.1", {"start": v(35.4, 69) * mm, "end": v(35.4, 61) * mm});
            skLineSegment(sketch, "E9.2.5.2", {"start": v(27.4, 69) * mm, "end": v(35.4, 69) * mm});
            skLineSegment(sketch, "E9.2.5.3", {"start": v(27.4, 61) * mm, "end": v(35.4, 61) * mm});
            skLineSegment(sketch, "E9.2.6.0", {"start": v(27.4, 80) * mm, "end": v(27.4, 72) * mm});
            skLineSegment(sketch, "E9.2.6.1", {"start": v(35.4, 80) * mm, "end": v(35.4, 72) * mm});
            skLineSegment(sketch, "E9.2.6.2", {"start": v(27.4, 80) * mm, "end": v(35.4, 80) * mm});
            skLineSegment(sketch, "E9.2.6.3", {"start": v(27.4, 72) * mm, "end": v(35.4, 72) * mm});
            skLineSegment(sketch, "E9.2.7.0", {"start": v(27.4, 91) * mm, "end": v(27.4, 83) * mm});
            skLineSegment(sketch, "E9.2.7.1", {"start": v(35.4, 91) * mm, "end": v(35.4, 83) * mm});
            skLineSegment(sketch, "E9.2.7.2", {"start": v(27.4, 91) * mm, "end": v(35.4, 91) * mm});
            skLineSegment(sketch, "E9.2.7.3", {"start": v(27.4, 83) * mm, "end": v(35.4, 83) * mm});
            skLineSegment(sketch, "E9.2.8.0", {"start": v(27.4, 102) * mm, "end": v(27.4, 94) * mm});
            skLineSegment(sketch, "E9.2.8.1", {"start": v(35.4, 102) * mm, "end": v(35.4, 94) * mm});
            skLineSegment(sketch, "E9.2.8.2", {"start": v(27.4, 102) * mm, "end": v(35.4, 102) * mm});
            skLineSegment(sketch, "E9.2.8.3", {"start": v(27.4, 94) * mm, "end": v(35.4, 94) * mm});
            skLineSegment(sketch, "E9.2.9.0", {"start": v(27.4, 113) * mm, "end": v(27.4, 105) * mm});
            skLineSegment(sketch, "E9.2.9.1", {"start": v(35.4, 113) * mm, "end": v(35.4, 105) * mm});
            skLineSegment(sketch, "E9.2.9.2", {"start": v(27.4, 113) * mm, "end": v(35.4, 113) * mm});
            skLineSegment(sketch, "E9.2.9.3", {"start": v(27.4, 105) * mm, "end": v(35.4, 105) * mm});
            skLineSegment(sketch, "E9.2.10.0", {"start": v(27.4, 124) * mm, "end": v(27.4, 116) * mm});
            skLineSegment(sketch, "E9.2.10.1", {"start": v(35.4, 124) * mm, "end": v(35.4, 116) * mm});
            skLineSegment(sketch, "E9.2.10.2", {"start": v(27.4, 124) * mm, "end": v(35.4, 124) * mm});
            skLineSegment(sketch, "E9.2.10.3", {"start": v(27.4, 116) * mm, "end": v(35.4, 116) * mm});
            skLineSegment(sketch, "E9.direction1", {"start": v(6, 6) * mm, "end": v(16.7, 6) * mm, "construction": true});
            skLineSegment(sketch, "E9.direction2", {"start": v(6, 6) * mm, "end": v(6, 17) * mm, "construction": true});
            skLineSegment(sketch, "E10", {"start": v(164, 0) * mm, "end": v(164, 59.25) * mm, "construction": true});
            skLineSegment(sketch, "E11.0.3.0", {"start": v(38.1, 14) * mm, "end": v(38.1, 6) * mm});
            skLineSegment(sketch, "E11.3.3.0", {"start": v(46.1, 14) * mm, "end": v(46.1, 6) * mm});
            skLineSegment(sketch, "E11.6.3.0", {"start": v(38.1, 14) * mm, "end": v(46.1, 14) * mm});
            skLineSegment(sketch, "E11.9.3.0", {"start": v(38.1, 6) * mm, "end": v(46.1, 6) * mm});
            skLineSegment(sketch, "E11.0.3.1", {"start": v(38.1, 25) * mm, "end": v(38.1, 17) * mm});
            skLineSegment(sketch, "E11.3.3.1", {"start": v(46.1, 25) * mm, "end": v(46.1, 17) * mm});
            skLineSegment(sketch, "E11.6.3.1", {"start": v(38.1, 25) * mm, "end": v(46.1, 25) * mm});
            skLineSegment(sketch, "E11.9.3.1", {"start": v(38.1, 17) * mm, "end": v(46.1, 17) * mm});
            skLineSegment(sketch, "E11.0.3.2", {"start": v(38.1, 36) * mm, "end": v(38.1, 28) * mm});
            skLineSegment(sketch, "E11.3.3.2", {"start": v(46.1, 36) * mm, "end": v(46.1, 28) * mm});
            skLineSegment(sketch, "E11.6.3.2", {"start": v(38.1, 36) * mm, "end": v(46.1, 36) * mm});
            skLineSegment(sketch, "E11.9.3.2", {"start": v(38.1, 28) * mm, "end": v(46.1, 28) * mm});
            skLineSegment(sketch, "E11.0.3.3", {"start": v(38.1, 47) * mm, "end": v(38.1, 39) * mm});
            skLineSegment(sketch, "E11.3.3.3", {"start": v(46.1, 47) * mm, "end": v(46.1, 39) * mm});
            skLineSegment(sketch, "E11.6.3.3", {"start": v(38.1, 47) * mm, "end": v(46.1, 47) * mm});
            skLineSegment(sketch, "E11.9.3.3", {"start": v(38.1, 39) * mm, "end": v(46.1, 39) * mm});
            skLineSegment(sketch, "E11.0.3.4", {"start": v(38.1, 58) * mm, "end": v(38.1, 50) * mm});
            skLineSegment(sketch, "E11.3.3.4", {"start": v(46.1, 58) * mm, "end": v(46.1, 50) * mm});
            skLineSegment(sketch, "E11.6.3.4", {"start": v(38.1, 58) * mm, "end": v(46.1, 58) * mm});
            skLineSegment(sketch, "E11.9.3.4", {"start": v(38.1, 50) * mm, "end": v(46.1, 50) * mm});
            skLineSegment(sketch, "E11.0.3.5", {"start": v(38.1, 69) * mm, "end": v(38.1, 61) * mm});
            skLineSegment(sketch, "E11.3.3.5", {"start": v(46.1, 69) * mm, "end": v(46.1, 61) * mm});
            skLineSegment(sketch, "E11.6.3.5", {"start": v(38.1, 69) * mm, "end": v(46.1, 69) * mm});
            skLineSegment(sketch, "E11.9.3.5", {"start": v(38.1, 61) * mm, "end": v(46.1, 61) * mm});
            skLineSegment(sketch, "E11.0.3.6", {"start": v(38.1, 80) * mm, "end": v(38.1, 72) * mm});
            skLineSegment(sketch, "E11.3.3.6", {"start": v(46.1, 80) * mm, "end": v(46.1, 72) * mm});
            skLineSegment(sketch, "E11.6.3.6", {"start": v(38.1, 80) * mm, "end": v(46.1, 80) * mm});
            skLineSegment(sketch, "E11.9.3.6", {"start": v(38.1, 72) * mm, "end": v(46.1, 72) * mm});
            skLineSegment(sketch, "E11.0.3.7", {"start": v(38.1, 91) * mm, "end": v(38.1, 83) * mm});
            skLineSegment(sketch, "E11.3.3.7", {"start": v(46.1, 91) * mm, "end": v(46.1, 83) * mm});
            skLineSegment(sketch, "E11.6.3.7", {"start": v(38.1, 91) * mm, "end": v(46.1, 91) * mm});
            skLineSegment(sketch, "E11.9.3.7", {"start": v(38.1, 83) * mm, "end": v(46.1, 83) * mm});
            skLineSegment(sketch, "E11.0.3.8", {"start": v(38.1, 102) * mm, "end": v(38.1, 94) * mm});
            skLineSegment(sketch, "E11.3.3.8", {"start": v(46.1, 102) * mm, "end": v(46.1, 94) * mm});
            skLineSegment(sketch, "E11.6.3.8", {"start": v(38.1, 102) * mm, "end": v(46.1, 102) * mm});
            skLineSegment(sketch, "E11.9.3.8", {"start": v(38.1, 94) * mm, "end": v(46.1, 94) * mm});
            skLineSegment(sketch, "E11.0.3.9", {"start": v(38.1, 113) * mm, "end": v(38.1, 105) * mm});
            skLineSegment(sketch, "E11.3.3.9", {"start": v(46.1, 113) * mm, "end": v(46.1, 105) * mm});
            skLineSegment(sketch, "E11.6.3.9", {"start": v(38.1, 113) * mm, "end": v(46.1, 113) * mm});
            skLineSegment(sketch, "E11.9.3.9", {"start": v(38.1, 105) * mm, "end": v(46.1, 105) * mm});
            skLineSegment(sketch, "E11.0.3.10", {"start": v(38.1, 124) * mm, "end": v(38.1, 116) * mm});
            skLineSegment(sketch, "E11.3.3.10", {"start": v(46.1, 124) * mm, "end": v(46.1, 116) * mm});
            skLineSegment(sketch, "E11.6.3.10", {"start": v(38.1, 124) * mm, "end": v(46.1, 124) * mm});
            skLineSegment(sketch, "E11.9.3.10", {"start": v(38.1, 116) * mm, "end": v(46.1, 116) * mm});
            skLineSegment(sketch, "E11.0.4.0", {"start": v(48.8, 14) * mm, "end": v(48.8, 6) * mm});
            skLineSegment(sketch, "E11.3.4.0", {"start": v(56.8, 14) * mm, "end": v(56.8, 6) * mm});
            skLineSegment(sketch, "E11.6.4.0", {"start": v(48.8, 14) * mm, "end": v(56.8, 14) * mm});
            skLineSegment(sketch, "E11.9.4.0", {"start": v(48.8, 6) * mm, "end": v(56.8, 6) * mm});
            skLineSegment(sketch, "E11.0.4.1", {"start": v(48.8, 25) * mm, "end": v(48.8, 17) * mm});
            skLineSegment(sketch, "E11.3.4.1", {"start": v(56.8, 25) * mm, "end": v(56.8, 17) * mm});
            skLineSegment(sketch, "E11.6.4.1", {"start": v(48.8, 25) * mm, "end": v(56.8, 25) * mm});
            skLineSegment(sketch, "E11.9.4.1", {"start": v(48.8, 17) * mm, "end": v(56.8, 17) * mm});
            skLineSegment(sketch, "E11.0.4.2", {"start": v(48.8, 36) * mm, "end": v(48.8, 28) * mm});
            skLineSegment(sketch, "E11.3.4.2", {"start": v(56.8, 36) * mm, "end": v(56.8, 28) * mm});
            skLineSegment(sketch, "E11.6.4.2", {"start": v(48.8, 36) * mm, "end": v(56.8, 36) * mm});
            skLineSegment(sketch, "E11.9.4.2", {"start": v(48.8, 28) * mm, "end": v(56.8, 28) * mm});
            skLineSegment(sketch, "E11.0.4.3", {"start": v(48.8, 47) * mm, "end": v(48.8, 39) * mm});
            skLineSegment(sketch, "E11.3.4.3", {"start": v(56.8, 47) * mm, "end": v(56.8, 39) * mm});
            skLineSegment(sketch, "E11.6.4.3", {"start": v(48.8, 47) * mm, "end": v(56.8, 47) * mm});
            skLineSegment(sketch, "E11.9.4.3", {"start": v(48.8, 39) * mm, "end": v(56.8, 39) * mm});
            skLineSegment(sketch, "E11.0.4.4", {"start": v(48.8, 58) * mm, "end": v(48.8, 50) * mm});
            skLineSegment(sketch, "E11.3.4.4", {"start": v(56.8, 58) * mm, "end": v(56.8, 50) * mm});
            skLineSegment(sketch, "E11.6.4.4", {"start": v(48.8, 58) * mm, "end": v(56.8, 58) * mm});
            skLineSegment(sketch, "E11.9.4.4", {"start": v(48.8, 50) * mm, "end": v(56.8, 50) * mm});
            skLineSegment(sketch, "E11.0.4.5", {"start": v(48.8, 69) * mm, "end": v(48.8, 61) * mm});
            skLineSegment(sketch, "E11.3.4.5", {"start": v(56.8, 69) * mm, "end": v(56.8, 61) * mm});
            skLineSegment(sketch, "E11.6.4.5", {"start": v(48.8, 69) * mm, "end": v(56.8, 69) * mm});
            skLineSegment(sketch, "E11.9.4.5", {"start": v(48.8, 61) * mm, "end": v(56.8, 61) * mm});
            skLineSegment(sketch, "E11.0.4.6", {"start": v(48.8, 80) * mm, "end": v(48.8, 72) * mm});
            skLineSegment(sketch, "E11.3.4.6", {"start": v(56.8, 80) * mm, "end": v(56.8, 72) * mm});
            skLineSegment(sketch, "E11.6.4.6", {"start": v(48.8, 80) * mm, "end": v(56.8, 80) * mm});
            skLineSegment(sketch, "E11.9.4.6", {"start": v(48.8, 72) * mm, "end": v(56.8, 72) * mm});
            skLineSegment(sketch, "E11.0.4.7", {"start": v(48.8, 91) * mm, "end": v(48.8, 83) * mm});
            skLineSegment(sketch, "E11.3.4.7", {"start": v(56.8, 91) * mm, "end": v(56.8, 83) * mm});
            skLineSegment(sketch, "E11.6.4.7", {"start": v(48.8, 91) * mm, "end": v(56.8, 91) * mm});
            skLineSegment(sketch, "E11.9.4.7", {"start": v(48.8, 83) * mm, "end": v(56.8, 83) * mm});
            skLineSegment(sketch, "E11.0.4.8", {"start": v(48.8, 102) * mm, "end": v(48.8, 94) * mm});
            skLineSegment(sketch, "E11.3.4.8", {"start": v(56.8, 102) * mm, "end": v(56.8, 94) * mm});
            skLineSegment(sketch, "E11.6.4.8", {"start": v(48.8, 102) * mm, "end": v(56.8, 102) * mm});
            skLineSegment(sketch, "E11.9.4.8", {"start": v(48.8, 94) * mm, "end": v(56.8, 94) * mm});
            skLineSegment(sketch, "E11.0.4.9", {"start": v(48.8, 113) * mm, "end": v(48.8, 105) * mm});
            skLineSegment(sketch, "E11.3.4.9", {"start": v(56.8, 113) * mm, "end": v(56.8, 105) * mm});
            skLineSegment(sketch, "E11.6.4.9", {"start": v(48.8, 113) * mm, "end": v(56.8, 113) * mm});
            skLineSegment(sketch, "E11.9.4.9", {"start": v(48.8, 105) * mm, "end": v(56.8, 105) * mm});
            skLineSegment(sketch, "E11.0.4.10", {"start": v(48.8, 124) * mm, "end": v(48.8, 116) * mm});
            skLineSegment(sketch, "E11.3.4.10", {"start": v(56.8, 124) * mm, "end": v(56.8, 116) * mm});
            skLineSegment(sketch, "E11.6.4.10", {"start": v(48.8, 124) * mm, "end": v(56.8, 124) * mm});
            skLineSegment(sketch, "E11.9.4.10", {"start": v(48.8, 116) * mm, "end": v(56.8, 116) * mm});
            skLineSegment(sketch, "E11.0.5.0", {"start": v(59.5, 14) * mm, "end": v(59.5, 6) * mm});
            skLineSegment(sketch, "E11.3.5.0", {"start": v(67.5, 14) * mm, "end": v(67.5, 6) * mm});
            skLineSegment(sketch, "E11.6.5.0", {"start": v(59.5, 14) * mm, "end": v(67.5, 14) * mm});
            skLineSegment(sketch, "E11.9.5.0", {"start": v(59.5, 6) * mm, "end": v(67.5, 6) * mm});
            skLineSegment(sketch, "E11.0.5.1", {"start": v(59.5, 25) * mm, "end": v(59.5, 17) * mm});
            skLineSegment(sketch, "E11.3.5.1", {"start": v(67.5, 25) * mm, "end": v(67.5, 17) * mm});
            skLineSegment(sketch, "E11.6.5.1", {"start": v(59.5, 25) * mm, "end": v(67.5, 25) * mm});
            skLineSegment(sketch, "E11.9.5.1", {"start": v(59.5, 17) * mm, "end": v(67.5, 17) * mm});
            skLineSegment(sketch, "E11.0.5.2", {"start": v(59.5, 36) * mm, "end": v(59.5, 28) * mm});
            skLineSegment(sketch, "E11.3.5.2", {"start": v(67.5, 36) * mm, "end": v(67.5, 28) * mm});
            skLineSegment(sketch, "E11.6.5.2", {"start": v(59.5, 36) * mm, "end": v(67.5, 36) * mm});
            skLineSegment(sketch, "E11.9.5.2", {"start": v(59.5, 28) * mm, "end": v(67.5, 28) * mm});
            skLineSegment(sketch, "E11.0.5.3", {"start": v(59.5, 47) * mm, "end": v(59.5, 39) * mm});
            skLineSegment(sketch, "E11.3.5.3", {"start": v(67.5, 47) * mm, "end": v(67.5, 39) * mm});
            skLineSegment(sketch, "E11.6.5.3", {"start": v(59.5, 47) * mm, "end": v(67.5, 47) * mm});
            skLineSegment(sketch, "E11.9.5.3", {"start": v(59.5, 39) * mm, "end": v(67.5, 39) * mm});
            skLineSegment(sketch, "E11.0.5.4", {"start": v(59.5, 58) * mm, "end": v(59.5, 50) * mm});
            skLineSegment(sketch, "E11.3.5.4", {"start": v(67.5, 58) * mm, "end": v(67.5, 50) * mm});
            skLineSegment(sketch, "E11.6.5.4", {"start": v(59.5, 58) * mm, "end": v(67.5, 58) * mm});
            skLineSegment(sketch, "E11.9.5.4", {"start": v(59.5, 50) * mm, "end": v(67.5, 50) * mm});
            skLineSegment(sketch, "E11.0.5.5", {"start": v(59.5, 69) * mm, "end": v(59.5, 61) * mm});
            skLineSegment(sketch, "E11.3.5.5", {"start": v(67.5, 69) * mm, "end": v(67.5, 61) * mm});
            skLineSegment(sketch, "E11.6.5.5", {"start": v(59.5, 69) * mm, "end": v(67.5, 69) * mm});
            skLineSegment(sketch, "E11.9.5.5", {"start": v(59.5, 61) * mm, "end": v(67.5, 61) * mm});
            skLineSegment(sketch, "E11.0.5.6", {"start": v(59.5, 80) * mm, "end": v(59.5, 72) * mm});
            skLineSegment(sketch, "E11.3.5.6", {"start": v(67.5, 80) * mm, "end": v(67.5, 72) * mm});
            skLineSegment(sketch, "E11.6.5.6", {"start": v(59.5, 80) * mm, "end": v(67.5, 80) * mm});
            skLineSegment(sketch, "E11.9.5.6", {"start": v(59.5, 72) * mm, "end": v(67.5, 72) * mm});
            skLineSegment(sketch, "E11.0.5.7", {"start": v(59.5, 91) * mm, "end": v(59.5, 83) * mm});
            skLineSegment(sketch, "E11.3.5.7", {"start": v(67.5, 91) * mm, "end": v(67.5, 83) * mm});
            skLineSegment(sketch, "E11.6.5.7", {"start": v(59.5, 91) * mm, "end": v(67.5, 91) * mm});
            skLineSegment(sketch, "E11.9.5.7", {"start": v(59.5, 83) * mm, "end": v(67.5, 83) * mm});
            skLineSegment(sketch, "E11.0.5.8", {"start": v(59.5, 102) * mm, "end": v(59.5, 94) * mm});
            skLineSegment(sketch, "E11.3.5.8", {"start": v(67.5, 102) * mm, "end": v(67.5, 94) * mm});
            skLineSegment(sketch, "E11.6.5.8", {"start": v(59.5, 102) * mm, "end": v(67.5, 102) * mm});
            skLineSegment(sketch, "E11.9.5.8", {"start": v(59.5, 94) * mm, "end": v(67.5, 94) * mm});
            skLineSegment(sketch, "E11.0.5.9", {"start": v(59.5, 113) * mm, "end": v(59.5, 105) * mm});
            skLineSegment(sketch, "E11.3.5.9", {"start": v(67.5, 113) * mm, "end": v(67.5, 105) * mm});
            skLineSegment(sketch, "E11.6.5.9", {"start": v(59.5, 113) * mm, "end": v(67.5, 113) * mm});
            skLineSegment(sketch, "E11.9.5.9", {"start": v(59.5, 105) * mm, "end": v(67.5, 105) * mm});
            skLineSegment(sketch, "E11.0.5.10", {"start": v(59.5, 124) * mm, "end": v(59.5, 116) * mm});
            skLineSegment(sketch, "E11.3.5.10", {"start": v(67.5, 124) * mm, "end": v(67.5, 116) * mm});
            skLineSegment(sketch, "E11.6.5.10", {"start": v(59.5, 124) * mm, "end": v(67.5, 124) * mm});
            skLineSegment(sketch, "E11.9.5.10", {"start": v(59.5, 116) * mm, "end": v(67.5, 116) * mm});
            skLineSegment(sketch, "E11.0.6.0", {"start": v(70.2, 14) * mm, "end": v(70.2, 6) * mm});
            skLineSegment(sketch, "E11.3.6.0", {"start": v(78.2, 14) * mm, "end": v(78.2, 6) * mm});
            skLineSegment(sketch, "E11.6.6.0", {"start": v(70.2, 14) * mm, "end": v(78.2, 14) * mm});
            skLineSegment(sketch, "E11.9.6.0", {"start": v(70.2, 6) * mm, "end": v(78.2, 6) * mm});
            skLineSegment(sketch, "E11.0.6.1", {"start": v(70.2, 25) * mm, "end": v(70.2, 17) * mm});
            skLineSegment(sketch, "E11.3.6.1", {"start": v(78.2, 25) * mm, "end": v(78.2, 17) * mm});
            skLineSegment(sketch, "E11.6.6.1", {"start": v(70.2, 25) * mm, "end": v(78.2, 25) * mm});
            skLineSegment(sketch, "E11.9.6.1", {"start": v(70.2, 17) * mm, "end": v(78.2, 17) * mm});
            skLineSegment(sketch, "E11.0.6.2", {"start": v(70.2, 36) * mm, "end": v(70.2, 28) * mm});
            skLineSegment(sketch, "E11.3.6.2", {"start": v(78.2, 36) * mm, "end": v(78.2, 28) * mm});
            skLineSegment(sketch, "E11.6.6.2", {"start": v(70.2, 36) * mm, "end": v(78.2, 36) * mm});
            skLineSegment(sketch, "E11.9.6.2", {"start": v(70.2, 28) * mm, "end": v(78.2, 28) * mm});
            skLineSegment(sketch, "E11.0.6.3", {"start": v(70.2, 47) * mm, "end": v(70.2, 39) * mm});
            skLineSegment(sketch, "E11.3.6.3", {"start": v(78.2, 47) * mm, "end": v(78.2, 39) * mm});
            skLineSegment(sketch, "E11.6.6.3", {"start": v(70.2, 47) * mm, "end": v(78.2, 47) * mm});
            skLineSegment(sketch, "E11.9.6.3", {"start": v(70.2, 39) * mm, "end": v(78.2, 39) * mm});
            skLineSegment(sketch, "E11.0.6.4", {"start": v(70.2, 58) * mm, "end": v(70.2, 50) * mm});
            skLineSegment(sketch, "E11.3.6.4", {"start": v(78.2, 58) * mm, "end": v(78.2, 50) * mm});
            skLineSegment(sketch, "E11.6.6.4", {"start": v(70.2, 58) * mm, "end": v(78.2, 58) * mm});
            skLineSegment(sketch, "E11.9.6.4", {"start": v(70.2, 50) * mm, "end": v(78.2, 50) * mm});
            skLineSegment(sketch, "E11.0.6.5", {"start": v(70.2, 69) * mm, "end": v(70.2, 61) * mm});
            skLineSegment(sketch, "E11.3.6.5", {"start": v(78.2, 69) * mm, "end": v(78.2, 61) * mm});
            skLineSegment(sketch, "E11.6.6.5", {"start": v(70.2, 69) * mm, "end": v(78.2, 69) * mm});
            skLineSegment(sketch, "E11.9.6.5", {"start": v(70.2, 61) * mm, "end": v(78.2, 61) * mm});
            skLineSegment(sketch, "E11.0.6.6", {"start": v(70.2, 80) * mm, "end": v(70.2, 72) * mm});
            skLineSegment(sketch, "E11.3.6.6", {"start": v(78.2, 80) * mm, "end": v(78.2, 72) * mm});
            skLineSegment(sketch, "E11.6.6.6", {"start": v(70.2, 80) * mm, "end": v(78.2, 80) * mm});
            skLineSegment(sketch, "E11.9.6.6", {"start": v(70.2, 72) * mm, "end": v(78.2, 72) * mm});
            skLineSegment(sketch, "E11.0.6.7", {"start": v(70.2, 91) * mm, "end": v(70.2, 83) * mm});
            skLineSegment(sketch, "E11.3.6.7", {"start": v(78.2, 91) * mm, "end": v(78.2, 83) * mm});
            skLineSegment(sketch, "E11.6.6.7", {"start": v(70.2, 91) * mm, "end": v(78.2, 91) * mm});
            skLineSegment(sketch, "E11.9.6.7", {"start": v(70.2, 83) * mm, "end": v(78.2, 83) * mm});
            skLineSegment(sketch, "E11.0.6.8", {"start": v(70.2, 102) * mm, "end": v(70.2, 94) * mm});
            skLineSegment(sketch, "E11.3.6.8", {"start": v(78.2, 102) * mm, "end": v(78.2, 94) * mm});
            skLineSegment(sketch, "E11.6.6.8", {"start": v(70.2, 102) * mm, "end": v(78.2, 102) * mm});
            skLineSegment(sketch, "E11.9.6.8", {"start": v(70.2, 94) * mm, "end": v(78.2, 94) * mm});
            skLineSegment(sketch, "E11.0.6.9", {"start": v(70.2, 113) * mm, "end": v(70.2, 105) * mm});
            skLineSegment(sketch, "E11.3.6.9", {"start": v(78.2, 113) * mm, "end": v(78.2, 105) * mm});
            skLineSegment(sketch, "E11.6.6.9", {"start": v(70.2, 113) * mm, "end": v(78.2, 113) * mm});
            skLineSegment(sketch, "E11.9.6.9", {"start": v(70.2, 105) * mm, "end": v(78.2, 105) * mm});
            skLineSegment(sketch, "E11.0.6.10", {"start": v(70.2, 124) * mm, "end": v(70.2, 116) * mm});
            skLineSegment(sketch, "E11.3.6.10", {"start": v(78.2, 124) * mm, "end": v(78.2, 116) * mm});
            skLineSegment(sketch, "E11.6.6.10", {"start": v(70.2, 124) * mm, "end": v(78.2, 124) * mm});
            skLineSegment(sketch, "E11.9.6.10", {"start": v(70.2, 116) * mm, "end": v(78.2, 116) * mm});
            skLineSegment(sketch, "E11.0.7.0", {"start": v(80.9, 14) * mm, "end": v(80.9, 6) * mm});
            skLineSegment(sketch, "E11.3.7.0", {"start": v(88.9, 14) * mm, "end": v(88.9, 6) * mm});
            skLineSegment(sketch, "E11.6.7.0", {"start": v(80.9, 14) * mm, "end": v(88.9, 14) * mm});
            skLineSegment(sketch, "E11.9.7.0", {"start": v(80.9, 6) * mm, "end": v(88.9, 6) * mm});
            skLineSegment(sketch, "E11.0.7.1", {"start": v(80.9, 25) * mm, "end": v(80.9, 17) * mm});
            skLineSegment(sketch, "E11.3.7.1", {"start": v(88.9, 25) * mm, "end": v(88.9, 17) * mm});
            skLineSegment(sketch, "E11.6.7.1", {"start": v(80.9, 25) * mm, "end": v(88.9, 25) * mm});
            skLineSegment(sketch, "E11.9.7.1", {"start": v(80.9, 17) * mm, "end": v(88.9, 17) * mm});
            skLineSegment(sketch, "E11.0.7.2", {"start": v(80.9, 36) * mm, "end": v(80.9, 28) * mm});
            skLineSegment(sketch, "E11.3.7.2", {"start": v(88.9, 36) * mm, "end": v(88.9, 28) * mm});
            skLineSegment(sketch, "E11.6.7.2", {"start": v(80.9, 36) * mm, "end": v(88.9, 36) * mm});
            skLineSegment(sketch, "E11.9.7.2", {"start": v(80.9, 28) * mm, "end": v(88.9, 28) * mm});
            skLineSegment(sketch, "E11.0.7.3", {"start": v(80.9, 47) * mm, "end": v(80.9, 39) * mm});
            skLineSegment(sketch, "E11.3.7.3", {"start": v(88.9, 47) * mm, "end": v(88.9, 39) * mm});
            skLineSegment(sketch, "E11.6.7.3", {"start": v(80.9, 47) * mm, "end": v(88.9, 47) * mm});
            skLineSegment(sketch, "E11.9.7.3", {"start": v(80.9, 39) * mm, "end": v(88.9, 39) * mm});
            skLineSegment(sketch, "E11.0.7.4", {"start": v(80.9, 58) * mm, "end": v(80.9, 50) * mm});
            skLineSegment(sketch, "E11.3.7.4", {"start": v(88.9, 58) * mm, "end": v(88.9, 50) * mm});
            skLineSegment(sketch, "E11.6.7.4", {"start": v(80.9, 58) * mm, "end": v(88.9, 58) * mm});
            skLineSegment(sketch, "E11.9.7.4", {"start": v(80.9, 50) * mm, "end": v(88.9, 50) * mm});
            skLineSegment(sketch, "E11.0.7.5", {"start": v(80.9, 69) * mm, "end": v(80.9, 61) * mm});
            skLineSegment(sketch, "E11.3.7.5", {"start": v(88.9, 69) * mm, "end": v(88.9, 61) * mm});
            skLineSegment(sketch, "E11.6.7.5", {"start": v(80.9, 69) * mm, "end": v(88.9, 69) * mm});
            skLineSegment(sketch, "E11.9.7.5", {"start": v(80.9, 61) * mm, "end": v(88.9, 61) * mm});
            skLineSegment(sketch, "E11.0.7.6", {"start": v(80.9, 80) * mm, "end": v(80.9, 72) * mm});
            skLineSegment(sketch, "E11.3.7.6", {"start": v(88.9, 80) * mm, "end": v(88.9, 72) * mm});
            skLineSegment(sketch, "E11.6.7.6", {"start": v(80.9, 80) * mm, "end": v(88.9, 80) * mm});
            skLineSegment(sketch, "E11.9.7.6", {"start": v(80.9, 72) * mm, "end": v(88.9, 72) * mm});
            skLineSegment(sketch, "E11.0.7.7", {"start": v(80.9, 91) * mm, "end": v(80.9, 83) * mm});
            skLineSegment(sketch, "E11.3.7.7", {"start": v(88.9, 91) * mm, "end": v(88.9, 83) * mm});
            skLineSegment(sketch, "E11.6.7.7", {"start": v(80.9, 91) * mm, "end": v(88.9, 91) * mm});
            skLineSegment(sketch, "E11.9.7.7", {"start": v(80.9, 83) * mm, "end": v(88.9, 83) * mm});
            skLineSegment(sketch, "E11.0.7.8", {"start": v(80.9, 102) * mm, "end": v(80.9, 94) * mm});
            skLineSegment(sketch, "E11.3.7.8", {"start": v(88.9, 102) * mm, "end": v(88.9, 94) * mm});
            skLineSegment(sketch, "E11.6.7.8", {"start": v(80.9, 102) * mm, "end": v(88.9, 102) * mm});
            skLineSegment(sketch, "E11.9.7.8", {"start": v(80.9, 94) * mm, "end": v(88.9, 94) * mm});
            skLineSegment(sketch, "E11.0.7.9", {"start": v(80.9, 113) * mm, "end": v(80.9, 105) * mm});
            skLineSegment(sketch, "E11.3.7.9", {"start": v(88.9, 113) * mm, "end": v(88.9, 105) * mm});
            skLineSegment(sketch, "E11.6.7.9", {"start": v(80.9, 113) * mm, "end": v(88.9, 113) * mm});
            skLineSegment(sketch, "E11.9.7.9", {"start": v(80.9, 105) * mm, "end": v(88.9, 105) * mm});
            skLineSegment(sketch, "E11.0.7.10", {"start": v(80.9, 124) * mm, "end": v(80.9, 116) * mm});
            skLineSegment(sketch, "E11.3.7.10", {"start": v(88.9, 124) * mm, "end": v(88.9, 116) * mm});
            skLineSegment(sketch, "E11.6.7.10", {"start": v(80.9, 124) * mm, "end": v(88.9, 124) * mm});
            skLineSegment(sketch, "E11.9.7.10", {"start": v(80.9, 116) * mm, "end": v(88.9, 116) * mm});
            skLineSegment(sketch, "E11.0.8.0", {"start": v(91.6, 14) * mm, "end": v(91.6, 6) * mm});
            skLineSegment(sketch, "E11.3.8.0", {"start": v(99.6, 14) * mm, "end": v(99.6, 6) * mm});
            skLineSegment(sketch, "E11.6.8.0", {"start": v(91.6, 14) * mm, "end": v(99.6, 14) * mm});
            skLineSegment(sketch, "E11.9.8.0", {"start": v(91.6, 6) * mm, "end": v(99.6, 6) * mm});
            skLineSegment(sketch, "E11.0.8.1", {"start": v(91.6, 25) * mm, "end": v(91.6, 17) * mm});
            skLineSegment(sketch, "E11.3.8.1", {"start": v(99.6, 25) * mm, "end": v(99.6, 17) * mm});
            skLineSegment(sketch, "E11.6.8.1", {"start": v(91.6, 25) * mm, "end": v(99.6, 25) * mm});
            skLineSegment(sketch, "E11.9.8.1", {"start": v(91.6, 17) * mm, "end": v(99.6, 17) * mm});
            skLineSegment(sketch, "E11.0.8.2", {"start": v(91.6, 36) * mm, "end": v(91.6, 28) * mm});
            skLineSegment(sketch, "E11.3.8.2", {"start": v(99.6, 36) * mm, "end": v(99.6, 28) * mm});
            skLineSegment(sketch, "E11.6.8.2", {"start": v(91.6, 36) * mm, "end": v(99.6, 36) * mm});
            skLineSegment(sketch, "E11.9.8.2", {"start": v(91.6, 28) * mm, "end": v(99.6, 28) * mm});
            skLineSegment(sketch, "E11.0.8.3", {"start": v(91.6, 47) * mm, "end": v(91.6, 39) * mm});
            skLineSegment(sketch, "E11.3.8.3", {"start": v(99.6, 47) * mm, "end": v(99.6, 39) * mm});
            skLineSegment(sketch, "E11.6.8.3", {"start": v(91.6, 47) * mm, "end": v(99.6, 47) * mm});
            skLineSegment(sketch, "E11.9.8.3", {"start": v(91.6, 39) * mm, "end": v(99.6, 39) * mm});
            skLineSegment(sketch, "E11.0.8.4", {"start": v(91.6, 58) * mm, "end": v(91.6, 50) * mm});
            skLineSegment(sketch, "E11.3.8.4", {"start": v(99.6, 58) * mm, "end": v(99.6, 50) * mm});
            skLineSegment(sketch, "E11.6.8.4", {"start": v(91.6, 58) * mm, "end": v(99.6, 58) * mm});
            skLineSegment(sketch, "E11.9.8.4", {"start": v(91.6, 50) * mm, "end": v(99.6, 50) * mm});
            skLineSegment(sketch, "E11.0.8.5", {"start": v(91.6, 69) * mm, "end": v(91.6, 61) * mm});
            skLineSegment(sketch, "E11.3.8.5", {"start": v(99.6, 69) * mm, "end": v(99.6, 61) * mm});
            skLineSegment(sketch, "E11.6.8.5", {"start": v(91.6, 69) * mm, "end": v(99.6, 69) * mm});
            skLineSegment(sketch, "E11.9.8.5", {"start": v(91.6, 61) * mm, "end": v(99.6, 61) * mm});
            skLineSegment(sketch, "E11.0.8.6", {"start": v(91.6, 80) * mm, "end": v(91.6, 72) * mm});
            skLineSegment(sketch, "E11.3.8.6", {"start": v(99.6, 80) * mm, "end": v(99.6, 72) * mm});
            skLineSegment(sketch, "E11.6.8.6", {"start": v(91.6, 80) * mm, "end": v(99.6, 80) * mm});
            skLineSegment(sketch, "E11.9.8.6", {"start": v(91.6, 72) * mm, "end": v(99.6, 72) * mm});
            skLineSegment(sketch, "E11.0.8.7", {"start": v(91.6, 91) * mm, "end": v(91.6, 83) * mm});
            skLineSegment(sketch, "E11.3.8.7", {"start": v(99.6, 91) * mm, "end": v(99.6, 83) * mm});
            skLineSegment(sketch, "E11.6.8.7", {"start": v(91.6, 91) * mm, "end": v(99.6, 91) * mm});
            skLineSegment(sketch, "E11.9.8.7", {"start": v(91.6, 83) * mm, "end": v(99.6, 83) * mm});
            skLineSegment(sketch, "E11.0.8.8", {"start": v(91.6, 102) * mm, "end": v(91.6, 94) * mm});
            skLineSegment(sketch, "E11.3.8.8", {"start": v(99.6, 102) * mm, "end": v(99.6, 94) * mm});
            skLineSegment(sketch, "E11.6.8.8", {"start": v(91.6, 102) * mm, "end": v(99.6, 102) * mm});
            skLineSegment(sketch, "E11.9.8.8", {"start": v(91.6, 94) * mm, "end": v(99.6, 94) * mm});
            skLineSegment(sketch, "E11.0.8.9", {"start": v(91.6, 113) * mm, "end": v(91.6, 105) * mm});
            skLineSegment(sketch, "E11.3.8.9", {"start": v(99.6, 113) * mm, "end": v(99.6, 105) * mm});
            skLineSegment(sketch, "E11.6.8.9", {"start": v(91.6, 113) * mm, "end": v(99.6, 113) * mm});
            skLineSegment(sketch, "E11.9.8.9", {"start": v(91.6, 105) * mm, "end": v(99.6, 105) * mm});
            skLineSegment(sketch, "E11.0.8.10", {"start": v(91.6, 124) * mm, "end": v(91.6, 116) * mm});
            skLineSegment(sketch, "E11.3.8.10", {"start": v(99.6, 124) * mm, "end": v(99.6, 116) * mm});
            skLineSegment(sketch, "E11.6.8.10", {"start": v(91.6, 124) * mm, "end": v(99.6, 124) * mm});
            skLineSegment(sketch, "E11.9.8.10", {"start": v(91.6, 116) * mm, "end": v(99.6, 116) * mm});
            skLineSegment(sketch, "E11.0.9.0", {"start": v(102.3, 14) * mm, "end": v(102.3, 6) * mm});
            skLineSegment(sketch, "E11.3.9.0", {"start": v(110.3, 14) * mm, "end": v(110.3, 6) * mm});
            skLineSegment(sketch, "E11.6.9.0", {"start": v(102.3, 14) * mm, "end": v(110.3, 14) * mm});
            skLineSegment(sketch, "E11.9.9.0", {"start": v(102.3, 6) * mm, "end": v(110.3, 6) * mm});
            skLineSegment(sketch, "E11.0.9.1", {"start": v(102.3, 25) * mm, "end": v(102.3, 17) * mm});
            skLineSegment(sketch, "E11.3.9.1", {"start": v(110.3, 25) * mm, "end": v(110.3, 17) * mm});
            skLineSegment(sketch, "E11.6.9.1", {"start": v(102.3, 25) * mm, "end": v(110.3, 25) * mm});
            skLineSegment(sketch, "E11.9.9.1", {"start": v(102.3, 17) * mm, "end": v(110.3, 17) * mm});
            skLineSegment(sketch, "E11.0.9.2", {"start": v(102.3, 36) * mm, "end": v(102.3, 28) * mm});
            skLineSegment(sketch, "E11.3.9.2", {"start": v(110.3, 36) * mm, "end": v(110.3, 28) * mm});
            skLineSegment(sketch, "E11.6.9.2", {"start": v(102.3, 36) * mm, "end": v(110.3, 36) * mm});
            skLineSegment(sketch, "E11.9.9.2", {"start": v(102.3, 28) * mm, "end": v(110.3, 28) * mm});
            skLineSegment(sketch, "E11.0.9.3", {"start": v(102.3, 47) * mm, "end": v(102.3, 39) * mm});
            skLineSegment(sketch, "E11.3.9.3", {"start": v(110.3, 47) * mm, "end": v(110.3, 39) * mm});
            skLineSegment(sketch, "E11.6.9.3", {"start": v(102.3, 47) * mm, "end": v(110.3, 47) * mm});
            skLineSegment(sketch, "E11.9.9.3", {"start": v(102.3, 39) * mm, "end": v(110.3, 39) * mm});
            skLineSegment(sketch, "E11.0.9.4", {"start": v(102.3, 58) * mm, "end": v(102.3, 50) * mm});
            skLineSegment(sketch, "E11.3.9.4", {"start": v(110.3, 58) * mm, "end": v(110.3, 50) * mm});
            skLineSegment(sketch, "E11.6.9.4", {"start": v(102.3, 58) * mm, "end": v(110.3, 58) * mm});
            skLineSegment(sketch, "E11.9.9.4", {"start": v(102.3, 50) * mm, "end": v(110.3, 50) * mm});
            skLineSegment(sketch, "E11.0.9.5", {"start": v(102.3, 69) * mm, "end": v(102.3, 61) * mm});
            skLineSegment(sketch, "E11.3.9.5", {"start": v(110.3, 69) * mm, "end": v(110.3, 61) * mm});
            skLineSegment(sketch, "E11.6.9.5", {"start": v(102.3, 69) * mm, "end": v(110.3, 69) * mm});
            skLineSegment(sketch, "E11.9.9.5", {"start": v(102.3, 61) * mm, "end": v(110.3, 61) * mm});
            skLineSegment(sketch, "E11.0.9.6", {"start": v(102.3, 80) * mm, "end": v(102.3, 72) * mm});
            skLineSegment(sketch, "E11.3.9.6", {"start": v(110.3, 80) * mm, "end": v(110.3, 72) * mm});
            skLineSegment(sketch, "E11.6.9.6", {"start": v(102.3, 80) * mm, "end": v(110.3, 80) * mm});
            skLineSegment(sketch, "E11.9.9.6", {"start": v(102.3, 72) * mm, "end": v(110.3, 72) * mm});
            skLineSegment(sketch, "E11.0.9.7", {"start": v(102.3, 91) * mm, "end": v(102.3, 83) * mm});
            skLineSegment(sketch, "E11.3.9.7", {"start": v(110.3, 91) * mm, "end": v(110.3, 83) * mm});
            skLineSegment(sketch, "E11.6.9.7", {"start": v(102.3, 91) * mm, "end": v(110.3, 91) * mm});
            skLineSegment(sketch, "E11.9.9.7", {"start": v(102.3, 83) * mm, "end": v(110.3, 83) * mm});
            skLineSegment(sketch, "E11.0.9.8", {"start": v(102.3, 102) * mm, "end": v(102.3, 94) * mm});
            skLineSegment(sketch, "E11.3.9.8", {"start": v(110.3, 102) * mm, "end": v(110.3, 94) * mm});
            skLineSegment(sketch, "E11.6.9.8", {"start": v(102.3, 102) * mm, "end": v(110.3, 102) * mm});
            skLineSegment(sketch, "E11.9.9.8", {"start": v(102.3, 94) * mm, "end": v(110.3, 94) * mm});
            skLineSegment(sketch, "E11.0.9.9", {"start": v(102.3, 113) * mm, "end": v(102.3, 105) * mm});
            skLineSegment(sketch, "E11.3.9.9", {"start": v(110.3, 113) * mm, "end": v(110.3, 105) * mm});
            skLineSegment(sketch, "E11.6.9.9", {"start": v(102.3, 113) * mm, "end": v(110.3, 113) * mm});
            skLineSegment(sketch, "E11.9.9.9", {"start": v(102.3, 105) * mm, "end": v(110.3, 105) * mm});
            skLineSegment(sketch, "E11.0.9.10", {"start": v(102.3, 124) * mm, "end": v(102.3, 116) * mm});
            skLineSegment(sketch, "E11.3.9.10", {"start": v(110.3, 124) * mm, "end": v(110.3, 116) * mm});
            skLineSegment(sketch, "E11.6.9.10", {"start": v(102.3, 124) * mm, "end": v(110.3, 124) * mm});
            skLineSegment(sketch, "E11.9.9.10", {"start": v(102.3, 116) * mm, "end": v(110.3, 116) * mm});
            skLineSegment(sketch, "E12.0.10.0", {"start": v(113, 14) * mm, "end": v(113, 6) * mm});
            skLineSegment(sketch, "E12.3.10.0", {"start": v(121, 14) * mm, "end": v(121, 6) * mm});
            skLineSegment(sketch, "E12.6.10.0", {"start": v(113, 14) * mm, "end": v(121, 14) * mm});
            skLineSegment(sketch, "E12.9.10.0", {"start": v(113, 6) * mm, "end": v(121, 6) * mm});
            skLineSegment(sketch, "E12.0.10.1", {"start": v(113, 25) * mm, "end": v(113, 17) * mm});
            skLineSegment(sketch, "E12.3.10.1", {"start": v(121, 25) * mm, "end": v(121, 17) * mm});
            skLineSegment(sketch, "E12.6.10.1", {"start": v(113, 25) * mm, "end": v(121, 25) * mm});
            skLineSegment(sketch, "E12.9.10.1", {"start": v(113, 17) * mm, "end": v(121, 17) * mm});
            skLineSegment(sketch, "E12.0.10.2", {"start": v(113, 36) * mm, "end": v(113, 28) * mm});
            skLineSegment(sketch, "E12.3.10.2", {"start": v(121, 36) * mm, "end": v(121, 28) * mm});
            skLineSegment(sketch, "E12.6.10.2", {"start": v(113, 36) * mm, "end": v(121, 36) * mm});
            skLineSegment(sketch, "E12.9.10.2", {"start": v(113, 28) * mm, "end": v(121, 28) * mm});
            skLineSegment(sketch, "E12.0.10.3", {"start": v(113, 47) * mm, "end": v(113, 39) * mm});
            skLineSegment(sketch, "E12.3.10.3", {"start": v(121, 47) * mm, "end": v(121, 39) * mm});
            skLineSegment(sketch, "E12.6.10.3", {"start": v(113, 47) * mm, "end": v(121, 47) * mm});
            skLineSegment(sketch, "E12.9.10.3", {"start": v(113, 39) * mm, "end": v(121, 39) * mm});
            skLineSegment(sketch, "E12.0.10.4", {"start": v(113, 58) * mm, "end": v(113, 50) * mm});
            skLineSegment(sketch, "E12.3.10.4", {"start": v(121, 58) * mm, "end": v(121, 50) * mm});
            skLineSegment(sketch, "E12.6.10.4", {"start": v(113, 58) * mm, "end": v(121, 58) * mm});
            skLineSegment(sketch, "E12.9.10.4", {"start": v(113, 50) * mm, "end": v(121, 50) * mm});
            skLineSegment(sketch, "E12.0.10.5", {"start": v(113, 69) * mm, "end": v(113, 61) * mm});
            skLineSegment(sketch, "E12.3.10.5", {"start": v(121, 69) * mm, "end": v(121, 61) * mm});
            skLineSegment(sketch, "E12.6.10.5", {"start": v(113, 69) * mm, "end": v(121, 69) * mm});
            skLineSegment(sketch, "E12.9.10.5", {"start": v(113, 61) * mm, "end": v(121, 61) * mm});
            skLineSegment(sketch, "E12.0.10.6", {"start": v(113, 80) * mm, "end": v(113, 72) * mm});
            skLineSegment(sketch, "E12.3.10.6", {"start": v(121, 80) * mm, "end": v(121, 72) * mm});
            skLineSegment(sketch, "E12.6.10.6", {"start": v(113, 80) * mm, "end": v(121, 80) * mm});
            skLineSegment(sketch, "E12.9.10.6", {"start": v(113, 72) * mm, "end": v(121, 72) * mm});
            skLineSegment(sketch, "E12.0.10.7", {"start": v(113, 91) * mm, "end": v(113, 83) * mm});
            skLineSegment(sketch, "E12.3.10.7", {"start": v(121, 91) * mm, "end": v(121, 83) * mm});
            skLineSegment(sketch, "E12.6.10.7", {"start": v(113, 91) * mm, "end": v(121, 91) * mm});
            skLineSegment(sketch, "E12.9.10.7", {"start": v(113, 83) * mm, "end": v(121, 83) * mm});
            skLineSegment(sketch, "E12.0.10.8", {"start": v(113, 102) * mm, "end": v(113, 94) * mm});
            skLineSegment(sketch, "E12.3.10.8", {"start": v(121, 102) * mm, "end": v(121, 94) * mm});
            skLineSegment(sketch, "E12.6.10.8", {"start": v(113, 102) * mm, "end": v(121, 102) * mm});
            skLineSegment(sketch, "E12.9.10.8", {"start": v(113, 94) * mm, "end": v(121, 94) * mm});
            skLineSegment(sketch, "E12.0.10.9", {"start": v(113, 113) * mm, "end": v(113, 105) * mm});
            skLineSegment(sketch, "E12.3.10.9", {"start": v(121, 113) * mm, "end": v(121, 105) * mm});
            skLineSegment(sketch, "E12.6.10.9", {"start": v(113, 113) * mm, "end": v(121, 113) * mm});
            skLineSegment(sketch, "E12.9.10.9", {"start": v(113, 105) * mm, "end": v(121, 105) * mm});
            skLineSegment(sketch, "E12.0.10.10", {"start": v(113, 124) * mm, "end": v(113, 116) * mm});
            skLineSegment(sketch, "E12.3.10.10", {"start": v(121, 124) * mm, "end": v(121, 116) * mm});
            skLineSegment(sketch, "E12.6.10.10", {"start": v(113, 124) * mm, "end": v(121, 124) * mm});
            skLineSegment(sketch, "E12.9.10.10", {"start": v(113, 116) * mm, "end": v(121, 116) * mm});
            skLineSegment(sketch, "E12.0.11.0", {"start": v(123.7, 14) * mm, "end": v(123.7, 6) * mm});
            skLineSegment(sketch, "E12.3.11.0", {"start": v(131.7, 14) * mm, "end": v(131.7, 6) * mm});
            skLineSegment(sketch, "E12.6.11.0", {"start": v(123.7, 14) * mm, "end": v(131.7, 14) * mm});
            skLineSegment(sketch, "E12.9.11.0", {"start": v(123.7, 6) * mm, "end": v(131.7, 6) * mm});
            skLineSegment(sketch, "E12.0.11.1", {"start": v(123.7, 25) * mm, "end": v(123.7, 17) * mm});
            skLineSegment(sketch, "E12.3.11.1", {"start": v(131.7, 25) * mm, "end": v(131.7, 17) * mm});
            skLineSegment(sketch, "E12.6.11.1", {"start": v(123.7, 25) * mm, "end": v(131.7, 25) * mm});
            skLineSegment(sketch, "E12.9.11.1", {"start": v(123.7, 17) * mm, "end": v(131.7, 17) * mm});
            skLineSegment(sketch, "E12.0.11.2", {"start": v(123.7, 36) * mm, "end": v(123.7, 28) * mm});
            skLineSegment(sketch, "E12.3.11.2", {"start": v(131.7, 36) * mm, "end": v(131.7, 28) * mm});
            skLineSegment(sketch, "E12.6.11.2", {"start": v(123.7, 36) * mm, "end": v(131.7, 36) * mm});
            skLineSegment(sketch, "E12.9.11.2", {"start": v(123.7, 28) * mm, "end": v(131.7, 28) * mm});
            skLineSegment(sketch, "E12.0.11.3", {"start": v(123.7, 47) * mm, "end": v(123.7, 39) * mm});
            skLineSegment(sketch, "E12.3.11.3", {"start": v(131.7, 47) * mm, "end": v(131.7, 39) * mm});
            skLineSegment(sketch, "E12.6.11.3", {"start": v(123.7, 47) * mm, "end": v(131.7, 47) * mm});
            skLineSegment(sketch, "E12.9.11.3", {"start": v(123.7, 39) * mm, "end": v(131.7, 39) * mm});
            skLineSegment(sketch, "E12.0.11.4", {"start": v(123.7, 58) * mm, "end": v(123.7, 50) * mm});
            skLineSegment(sketch, "E12.3.11.4", {"start": v(131.7, 58) * mm, "end": v(131.7, 50) * mm});
            skLineSegment(sketch, "E12.6.11.4", {"start": v(123.7, 58) * mm, "end": v(131.7, 58) * mm});
            skLineSegment(sketch, "E12.9.11.4", {"start": v(123.7, 50) * mm, "end": v(131.7, 50) * mm});
            skLineSegment(sketch, "E12.0.11.5", {"start": v(123.7, 69) * mm, "end": v(123.7, 61) * mm});
            skLineSegment(sketch, "E12.3.11.5", {"start": v(131.7, 69) * mm, "end": v(131.7, 61) * mm});
            skLineSegment(sketch, "E12.6.11.5", {"start": v(123.7, 69) * mm, "end": v(131.7, 69) * mm});
            skLineSegment(sketch, "E12.9.11.5", {"start": v(123.7, 61) * mm, "end": v(131.7, 61) * mm});
            skLineSegment(sketch, "E12.0.11.6", {"start": v(123.7, 80) * mm, "end": v(123.7, 72) * mm});
            skLineSegment(sketch, "E12.3.11.6", {"start": v(131.7, 80) * mm, "end": v(131.7, 72) * mm});
            skLineSegment(sketch, "E12.6.11.6", {"start": v(123.7, 80) * mm, "end": v(131.7, 80) * mm});
            skLineSegment(sketch, "E12.9.11.6", {"start": v(123.7, 72) * mm, "end": v(131.7, 72) * mm});
            skLineSegment(sketch, "E12.0.11.7", {"start": v(123.7, 91) * mm, "end": v(123.7, 83) * mm});
            skLineSegment(sketch, "E12.3.11.7", {"start": v(131.7, 91) * mm, "end": v(131.7, 83) * mm});
            skLineSegment(sketch, "E12.6.11.7", {"start": v(123.7, 91) * mm, "end": v(131.7, 91) * mm});
            skLineSegment(sketch, "E12.9.11.7", {"start": v(123.7, 83) * mm, "end": v(131.7, 83) * mm});
            skLineSegment(sketch, "E12.0.11.8", {"start": v(123.7, 102) * mm, "end": v(123.7, 94) * mm});
            skLineSegment(sketch, "E12.3.11.8", {"start": v(131.7, 102) * mm, "end": v(131.7, 94) * mm});
            skLineSegment(sketch, "E12.6.11.8", {"start": v(123.7, 102) * mm, "end": v(131.7, 102) * mm});
            skLineSegment(sketch, "E12.9.11.8", {"start": v(123.7, 94) * mm, "end": v(131.7, 94) * mm});
            skLineSegment(sketch, "E12.0.11.9", {"start": v(123.7, 113) * mm, "end": v(123.7, 105) * mm});
            skLineSegment(sketch, "E12.3.11.9", {"start": v(131.7, 113) * mm, "end": v(131.7, 105) * mm});
            skLineSegment(sketch, "E12.6.11.9", {"start": v(123.7, 113) * mm, "end": v(131.7, 113) * mm});
            skLineSegment(sketch, "E12.9.11.9", {"start": v(123.7, 105) * mm, "end": v(131.7, 105) * mm});
            skLineSegment(sketch, "E12.0.11.10", {"start": v(123.7, 124) * mm, "end": v(123.7, 116) * mm});
            skLineSegment(sketch, "E12.3.11.10", {"start": v(131.7, 124) * mm, "end": v(131.7, 116) * mm});
            skLineSegment(sketch, "E12.6.11.10", {"start": v(123.7, 124) * mm, "end": v(131.7, 124) * mm});
            skLineSegment(sketch, "E12.9.11.10", {"start": v(123.7, 116) * mm, "end": v(131.7, 116) * mm});
            skLineSegment(sketch, "E12.0.12.0", {"start": v(134.4, 14) * mm, "end": v(134.4, 6) * mm});
            skLineSegment(sketch, "E12.3.12.0", {"start": v(142.4, 14) * mm, "end": v(142.4, 6) * mm});
            skLineSegment(sketch, "E12.6.12.0", {"start": v(134.4, 14) * mm, "end": v(142.4, 14) * mm});
            skLineSegment(sketch, "E12.9.12.0", {"start": v(134.4, 6) * mm, "end": v(142.4, 6) * mm});
            skLineSegment(sketch, "E12.0.12.1", {"start": v(134.4, 25) * mm, "end": v(134.4, 17) * mm});
            skLineSegment(sketch, "E12.3.12.1", {"start": v(142.4, 25) * mm, "end": v(142.4, 17) * mm});
            skLineSegment(sketch, "E12.6.12.1", {"start": v(134.4, 25) * mm, "end": v(142.4, 25) * mm});
            skLineSegment(sketch, "E12.9.12.1", {"start": v(134.4, 17) * mm, "end": v(142.4, 17) * mm});
            skLineSegment(sketch, "E12.0.12.2", {"start": v(134.4, 36) * mm, "end": v(134.4, 28) * mm});
            skLineSegment(sketch, "E12.3.12.2", {"start": v(142.4, 36) * mm, "end": v(142.4, 28) * mm});
            skLineSegment(sketch, "E12.6.12.2", {"start": v(134.4, 36) * mm, "end": v(142.4, 36) * mm});
            skLineSegment(sketch, "E12.9.12.2", {"start": v(134.4, 28) * mm, "end": v(142.4, 28) * mm});
            skLineSegment(sketch, "E12.0.12.3", {"start": v(134.4, 47) * mm, "end": v(134.4, 39) * mm});
            skLineSegment(sketch, "E12.3.12.3", {"start": v(142.4, 47) * mm, "end": v(142.4, 39) * mm});
            skLineSegment(sketch, "E12.6.12.3", {"start": v(134.4, 47) * mm, "end": v(142.4, 47) * mm});
            skLineSegment(sketch, "E12.9.12.3", {"start": v(134.4, 39) * mm, "end": v(142.4, 39) * mm});
            skLineSegment(sketch, "E12.0.12.4", {"start": v(134.4, 58) * mm, "end": v(134.4, 50) * mm});
            skLineSegment(sketch, "E12.3.12.4", {"start": v(142.4, 58) * mm, "end": v(142.4, 50) * mm});
            skLineSegment(sketch, "E12.6.12.4", {"start": v(134.4, 58) * mm, "end": v(142.4, 58) * mm});
            skLineSegment(sketch, "E12.9.12.4", {"start": v(134.4, 50) * mm, "end": v(142.4, 50) * mm});
            skLineSegment(sketch, "E12.0.12.5", {"start": v(134.4, 69) * mm, "end": v(134.4, 61) * mm});
            skLineSegment(sketch, "E12.3.12.5", {"start": v(142.4, 69) * mm, "end": v(142.4, 61) * mm});
            skLineSegment(sketch, "E12.6.12.5", {"start": v(134.4, 69) * mm, "end": v(142.4, 69) * mm});
            skLineSegment(sketch, "E12.9.12.5", {"start": v(134.4, 61) * mm, "end": v(142.4, 61) * mm});
            skLineSegment(sketch, "E12.0.12.6", {"start": v(134.4, 80) * mm, "end": v(134.4, 72) * mm});
            skLineSegment(sketch, "E12.3.12.6", {"start": v(142.4, 80) * mm, "end": v(142.4, 72) * mm});
            skLineSegment(sketch, "E12.6.12.6", {"start": v(134.4, 80) * mm, "end": v(142.4, 80) * mm});
            skLineSegment(sketch, "E12.9.12.6", {"start": v(134.4, 72) * mm, "end": v(142.4, 72) * mm});
            skLineSegment(sketch, "E12.0.12.7", {"start": v(134.4, 91) * mm, "end": v(134.4, 83) * mm});
            skLineSegment(sketch, "E12.3.12.7", {"start": v(142.4, 91) * mm, "end": v(142.4, 83) * mm});
            skLineSegment(sketch, "E12.6.12.7", {"start": v(134.4, 91) * mm, "end": v(142.4, 91) * mm});
            skLineSegment(sketch, "E12.9.12.7", {"start": v(134.4, 83) * mm, "end": v(142.4, 83) * mm});
            skLineSegment(sketch, "E12.0.12.8", {"start": v(134.4, 102) * mm, "end": v(134.4, 94) * mm});
            skLineSegment(sketch, "E12.3.12.8", {"start": v(142.4, 102) * mm, "end": v(142.4, 94) * mm});
            skLineSegment(sketch, "E12.6.12.8", {"start": v(134.4, 102) * mm, "end": v(142.4, 102) * mm});
            skLineSegment(sketch, "E12.9.12.8", {"start": v(134.4, 94) * mm, "end": v(142.4, 94) * mm});
            skLineSegment(sketch, "E12.0.12.9", {"start": v(134.4, 113) * mm, "end": v(134.4, 105) * mm});
            skLineSegment(sketch, "E12.3.12.9", {"start": v(142.4, 113) * mm, "end": v(142.4, 105) * mm});
            skLineSegment(sketch, "E12.6.12.9", {"start": v(134.4, 113) * mm, "end": v(142.4, 113) * mm});
            skLineSegment(sketch, "E12.9.12.9", {"start": v(134.4, 105) * mm, "end": v(142.4, 105) * mm});
            skLineSegment(sketch, "E12.0.12.10", {"start": v(134.4, 124) * mm, "end": v(134.4, 116) * mm});
            skLineSegment(sketch, "E12.3.12.10", {"start": v(142.4, 124) * mm, "end": v(142.4, 116) * mm});
            skLineSegment(sketch, "E12.6.12.10", {"start": v(134.4, 124) * mm, "end": v(142.4, 124) * mm});
            skLineSegment(sketch, "E12.9.12.10", {"start": v(134.4, 116) * mm, "end": v(142.4, 116) * mm});
            skLineSegment(sketch, "E12.0.13.0", {"start": v(145.1, 14) * mm, "end": v(145.1, 6) * mm});
            skLineSegment(sketch, "E12.3.13.0", {"start": v(153.1, 14) * mm, "end": v(153.1, 6) * mm});
            skLineSegment(sketch, "E12.6.13.0", {"start": v(145.1, 14) * mm, "end": v(153.1, 14) * mm});
            skLineSegment(sketch, "E12.9.13.0", {"start": v(145.1, 6) * mm, "end": v(153.1, 6) * mm});
            skLineSegment(sketch, "E12.0.13.1", {"start": v(145.1, 25) * mm, "end": v(145.1, 17) * mm});
            skLineSegment(sketch, "E12.3.13.1", {"start": v(153.1, 25) * mm, "end": v(153.1, 17) * mm});
            skLineSegment(sketch, "E12.6.13.1", {"start": v(145.1, 25) * mm, "end": v(153.1, 25) * mm});
            skLineSegment(sketch, "E12.9.13.1", {"start": v(145.1, 17) * mm, "end": v(153.1, 17) * mm});
            skLineSegment(sketch, "E12.0.13.2", {"start": v(145.1, 36) * mm, "end": v(145.1, 28) * mm});
            skLineSegment(sketch, "E12.3.13.2", {"start": v(153.1, 36) * mm, "end": v(153.1, 28) * mm});
            skLineSegment(sketch, "E12.6.13.2", {"start": v(145.1, 36) * mm, "end": v(153.1, 36) * mm});
            skLineSegment(sketch, "E12.9.13.2", {"start": v(145.1, 28) * mm, "end": v(153.1, 28) * mm});
            skLineSegment(sketch, "E12.0.13.3", {"start": v(145.1, 47) * mm, "end": v(145.1, 39) * mm});
            skLineSegment(sketch, "E12.3.13.3", {"start": v(153.1, 47) * mm, "end": v(153.1, 39) * mm});
            skLineSegment(sketch, "E12.6.13.3", {"start": v(145.1, 47) * mm, "end": v(153.1, 47) * mm});
            skLineSegment(sketch, "E12.9.13.3", {"start": v(145.1, 39) * mm, "end": v(153.1, 39) * mm});
            skLineSegment(sketch, "E12.0.13.4", {"start": v(145.1, 58) * mm, "end": v(145.1, 50) * mm});
            skLineSegment(sketch, "E12.3.13.4", {"start": v(153.1, 58) * mm, "end": v(153.1, 50) * mm});
            skLineSegment(sketch, "E12.6.13.4", {"start": v(145.1, 58) * mm, "end": v(153.1, 58) * mm});
            skLineSegment(sketch, "E12.9.13.4", {"start": v(145.1, 50) * mm, "end": v(153.1, 50) * mm});
            skLineSegment(sketch, "E12.0.13.5", {"start": v(145.1, 69) * mm, "end": v(145.1, 61) * mm});
            skLineSegment(sketch, "E12.3.13.5", {"start": v(153.1, 69) * mm, "end": v(153.1, 61) * mm});
            skLineSegment(sketch, "E12.6.13.5", {"start": v(145.1, 69) * mm, "end": v(153.1, 69) * mm});
            skLineSegment(sketch, "E12.9.13.5", {"start": v(145.1, 61) * mm, "end": v(153.1, 61) * mm});
            skLineSegment(sketch, "E12.0.13.6", {"start": v(145.1, 80) * mm, "end": v(145.1, 72) * mm});
            skLineSegment(sketch, "E12.3.13.6", {"start": v(153.1, 80) * mm, "end": v(153.1, 72) * mm});
            skLineSegment(sketch, "E12.6.13.6", {"start": v(145.1, 80) * mm, "end": v(153.1, 80) * mm});
            skLineSegment(sketch, "E12.9.13.6", {"start": v(145.1, 72) * mm, "end": v(153.1, 72) * mm});
            skLineSegment(sketch, "E12.0.13.7", {"start": v(145.1, 91) * mm, "end": v(145.1, 83) * mm});
            skLineSegment(sketch, "E12.3.13.7", {"start": v(153.1, 91) * mm, "end": v(153.1, 83) * mm});
            skLineSegment(sketch, "E12.6.13.7", {"start": v(145.1, 91) * mm, "end": v(153.1, 91) * mm});
            skLineSegment(sketch, "E12.9.13.7", {"start": v(145.1, 83) * mm, "end": v(153.1, 83) * mm});
            skLineSegment(sketch, "E12.0.13.8", {"start": v(145.1, 102) * mm, "end": v(145.1, 94) * mm});
            skLineSegment(sketch, "E12.3.13.8", {"start": v(153.1, 102) * mm, "end": v(153.1, 94) * mm});
            skLineSegment(sketch, "E12.6.13.8", {"start": v(145.1, 102) * mm, "end": v(153.1, 102) * mm});
            skLineSegment(sketch, "E12.9.13.8", {"start": v(145.1, 94) * mm, "end": v(153.1, 94) * mm});
            skLineSegment(sketch, "E12.0.13.9", {"start": v(145.1, 113) * mm, "end": v(145.1, 105) * mm});
            skLineSegment(sketch, "E12.3.13.9", {"start": v(153.1, 113) * mm, "end": v(153.1, 105) * mm});
            skLineSegment(sketch, "E12.6.13.9", {"start": v(145.1, 113) * mm, "end": v(153.1, 113) * mm});
            skLineSegment(sketch, "E12.9.13.9", {"start": v(145.1, 105) * mm, "end": v(153.1, 105) * mm});
            skLineSegment(sketch, "E12.0.13.10", {"start": v(145.1, 124) * mm, "end": v(145.1, 116) * mm});
            skLineSegment(sketch, "E12.3.13.10", {"start": v(153.1, 124) * mm, "end": v(153.1, 116) * mm});
            skLineSegment(sketch, "E12.6.13.10", {"start": v(145.1, 124) * mm, "end": v(153.1, 124) * mm});
            skLineSegment(sketch, "E12.9.13.10", {"start": v(145.1, 116) * mm, "end": v(153.1, 116) * mm});
            skLineSegment(sketch, "E13.0.14.0", {"start": v(155.8, 14) * mm, "end": v(155.8, 6) * mm});
            skLineSegment(sketch, "E13.3.14.0", {"start": v(163.8, 14) * mm, "end": v(163.8, 6) * mm});
            skLineSegment(sketch, "E13.6.14.0", {"start": v(155.8, 14) * mm, "end": v(163.8, 14) * mm});
            skLineSegment(sketch, "E13.9.14.0", {"start": v(155.8, 6) * mm, "end": v(163.8, 6) * mm});
            skLineSegment(sketch, "E13.0.14.1", {"start": v(155.8, 25) * mm, "end": v(155.8, 17) * mm});
            skLineSegment(sketch, "E13.3.14.1", {"start": v(163.8, 25) * mm, "end": v(163.8, 17) * mm});
            skLineSegment(sketch, "E13.6.14.1", {"start": v(155.8, 25) * mm, "end": v(163.8, 25) * mm});
            skLineSegment(sketch, "E13.9.14.1", {"start": v(155.8, 17) * mm, "end": v(163.8, 17) * mm});
            skLineSegment(sketch, "E13.0.14.2", {"start": v(155.8, 36) * mm, "end": v(155.8, 28) * mm});
            skLineSegment(sketch, "E13.3.14.2", {"start": v(163.8, 36) * mm, "end": v(163.8, 28) * mm});
            skLineSegment(sketch, "E13.6.14.2", {"start": v(155.8, 36) * mm, "end": v(163.8, 36) * mm});
            skLineSegment(sketch, "E13.9.14.2", {"start": v(155.8, 28) * mm, "end": v(163.8, 28) * mm});
            skLineSegment(sketch, "E13.0.14.3", {"start": v(155.8, 47) * mm, "end": v(155.8, 39) * mm});
            skLineSegment(sketch, "E13.3.14.3", {"start": v(163.8, 47) * mm, "end": v(163.8, 39) * mm});
            skLineSegment(sketch, "E13.6.14.3", {"start": v(155.8, 47) * mm, "end": v(163.8, 47) * mm});
            skLineSegment(sketch, "E13.9.14.3", {"start": v(155.8, 39) * mm, "end": v(163.8, 39) * mm});
            skLineSegment(sketch, "E13.0.14.4", {"start": v(155.8, 58) * mm, "end": v(155.8, 50) * mm});
            skLineSegment(sketch, "E13.3.14.4", {"start": v(163.8, 58) * mm, "end": v(163.8, 50) * mm});
            skLineSegment(sketch, "E13.6.14.4", {"start": v(155.8, 58) * mm, "end": v(163.8, 58) * mm});
            skLineSegment(sketch, "E13.9.14.4", {"start": v(155.8, 50) * mm, "end": v(163.8, 50) * mm});
            skLineSegment(sketch, "E13.0.14.5", {"start": v(155.8, 69) * mm, "end": v(155.8, 61) * mm});
            skLineSegment(sketch, "E13.3.14.5", {"start": v(163.8, 69) * mm, "end": v(163.8, 61) * mm});
            skLineSegment(sketch, "E13.6.14.5", {"start": v(155.8, 69) * mm, "end": v(163.8, 69) * mm});
            skLineSegment(sketch, "E13.9.14.5", {"start": v(155.8, 61) * mm, "end": v(163.8, 61) * mm});
            skLineSegment(sketch, "E13.0.14.6", {"start": v(155.8, 80) * mm, "end": v(155.8, 72) * mm});
            skLineSegment(sketch, "E13.3.14.6", {"start": v(163.8, 80) * mm, "end": v(163.8, 72) * mm});
            skLineSegment(sketch, "E13.6.14.6", {"start": v(155.8, 80) * mm, "end": v(163.8, 80) * mm});
            skLineSegment(sketch, "E13.9.14.6", {"start": v(155.8, 72) * mm, "end": v(163.8, 72) * mm});
            skLineSegment(sketch, "E13.0.14.7", {"start": v(155.8, 91) * mm, "end": v(155.8, 83) * mm});
            skLineSegment(sketch, "E13.3.14.7", {"start": v(163.8, 91) * mm, "end": v(163.8, 83) * mm});
            skLineSegment(sketch, "E13.6.14.7", {"start": v(155.8, 91) * mm, "end": v(163.8, 91) * mm});
            skLineSegment(sketch, "E13.9.14.7", {"start": v(155.8, 83) * mm, "end": v(163.8, 83) * mm});
            skLineSegment(sketch, "E13.0.14.8", {"start": v(155.8, 102) * mm, "end": v(155.8, 94) * mm});
            skLineSegment(sketch, "E13.3.14.8", {"start": v(163.8, 102) * mm, "end": v(163.8, 94) * mm});
            skLineSegment(sketch, "E13.6.14.8", {"start": v(155.8, 102) * mm, "end": v(163.8, 102) * mm});
            skLineSegment(sketch, "E13.9.14.8", {"start": v(155.8, 94) * mm, "end": v(163.8, 94) * mm});
            skLineSegment(sketch, "E13.0.14.9", {"start": v(155.8, 113) * mm, "end": v(155.8, 105) * mm});
            skLineSegment(sketch, "E13.3.14.9", {"start": v(163.8, 113) * mm, "end": v(163.8, 105) * mm});
            skLineSegment(sketch, "E13.6.14.9", {"start": v(155.8, 113) * mm, "end": v(163.8, 113) * mm});
            skLineSegment(sketch, "E13.9.14.9", {"start": v(155.8, 105) * mm, "end": v(163.8, 105) * mm});
            skLineSegment(sketch, "E13.0.14.10", {"start": v(155.8, 124) * mm, "end": v(155.8, 116) * mm});
            skLineSegment(sketch, "E13.3.14.10", {"start": v(163.8, 124) * mm, "end": v(163.8, 116) * mm});
            skLineSegment(sketch, "E13.6.14.10", {"start": v(155.8, 124) * mm, "end": v(163.8, 124) * mm});
            skLineSegment(sketch, "E13.9.14.10", {"start": v(155.8, 116) * mm, "end": v(163.8, 116) * mm});
            skSolve(sketch);
        }
        {
            var Q0;
            Q0 = qSketchRegion(id + "F7", true);
            extrude(context, id + "F8", {"entities" : qUnion([Q0]), "operationType" : NewBodyOperationType.REMOVE, "oppositeDirection" : true, "depth" : 140 * mm, "offsetDistance" : 25 * mm});
        }
        {
            var Q0;
            Q0=qCreatedBy(makeId("Top.planeOp"),FACE);
            var sketch = newSketch(context, id + "F9", { "sketchPlane" : qUnion([Q0])});
            skLineSegment(sketch, "E14.bottom", {"start": v(6, 6) * mm, "end": v(14, 6) * mm});
            skLineSegment(sketch, "E14.top", {"start": v(6, 14) * mm, "end": v(14, 14) * mm});
            skLineSegment(sketch, "E14.left", {"start": v(6, 6) * mm, "end": v(6, 14) * mm});
            skLineSegment(sketch, "E14.right", {"start": v(14, 6) * mm, "end": v(14, 14) * mm});
            skLineSegment(sketch, "E15", {"start": v(164, 0) * mm, "end": v(164, 62.65) * mm, "construction": true});
            skLineSegment(sketch, "E16", {"start": v(-7.34, 134) * mm, "end": v(91.38, 134) * mm, "construction": true});
            skLineSegment(sketch, "E17.0.1.0", {"start": v(6, 16.9) * mm, "end": v(14, 16.9) * mm});
            skLineSegment(sketch, "E17.0.1.1", {"start": v(14, 16.9) * mm, "end": v(14, 24.9) * mm});
            skLineSegment(sketch, "E17.0.1.2", {"start": v(6, 24.9) * mm, "end": v(14, 24.9) * mm});
            skLineSegment(sketch, "E17.0.1.3", {"start": v(6, 16.9) * mm, "end": v(6, 24.9) * mm});
            skLineSegment(sketch, "E17.0.2.0", {"start": v(6, 27.8) * mm, "end": v(14, 27.8) * mm});
            skLineSegment(sketch, "E17.0.2.1", {"start": v(14, 27.8) * mm, "end": v(14, 35.8) * mm});
            skLineSegment(sketch, "E17.0.2.2", {"start": v(6, 35.8) * mm, "end": v(14, 35.8) * mm});
            skLineSegment(sketch, "E17.0.2.3", {"start": v(6, 27.8) * mm, "end": v(6, 35.8) * mm});
            skLineSegment(sketch, "E17.0.3.0", {"start": v(6, 38.7) * mm, "end": v(14, 38.7) * mm});
            skLineSegment(sketch, "E17.0.3.1", {"start": v(14, 38.7) * mm, "end": v(14, 46.7) * mm});
            skLineSegment(sketch, "E17.0.3.2", {"start": v(6, 46.7) * mm, "end": v(14, 46.7) * mm});
            skLineSegment(sketch, "E17.0.3.3", {"start": v(6, 38.7) * mm, "end": v(6, 46.7) * mm});
            skLineSegment(sketch, "E17.0.4.0", {"start": v(6, 49.6) * mm, "end": v(14, 49.6) * mm});
            skLineSegment(sketch, "E17.0.4.1", {"start": v(14, 49.6) * mm, "end": v(14, 57.6) * mm});
            skLineSegment(sketch, "E17.0.4.2", {"start": v(6, 57.6) * mm, "end": v(14, 57.6) * mm});
            skLineSegment(sketch, "E17.0.4.3", {"start": v(6, 49.6) * mm, "end": v(6, 57.6) * mm});
            skLineSegment(sketch, "E17.0.5.0", {"start": v(6, 60.5) * mm, "end": v(14, 60.5) * mm});
            skLineSegment(sketch, "E17.0.5.1", {"start": v(14, 60.5) * mm, "end": v(14, 68.5) * mm});
            skLineSegment(sketch, "E17.0.5.2", {"start": v(6, 68.5) * mm, "end": v(14, 68.5) * mm});
            skLineSegment(sketch, "E17.0.5.3", {"start": v(6, 60.5) * mm, "end": v(6, 68.5) * mm});
            skLineSegment(sketch, "E17.0.6.0", {"start": v(6, 71.4) * mm, "end": v(14, 71.4) * mm});
            skLineSegment(sketch, "E17.0.6.1", {"start": v(14, 71.4) * mm, "end": v(14, 79.4) * mm});
            skLineSegment(sketch, "E17.0.6.2", {"start": v(6, 79.4) * mm, "end": v(14, 79.4) * mm});
            skLineSegment(sketch, "E17.0.6.3", {"start": v(6, 71.4) * mm, "end": v(6, 79.4) * mm});
            skLineSegment(sketch, "E17.0.7.0", {"start": v(6, 82.3) * mm, "end": v(14, 82.3) * mm});
            skLineSegment(sketch, "E17.0.7.1", {"start": v(14, 82.3) * mm, "end": v(14, 90.3) * mm});
            skLineSegment(sketch, "E17.0.7.2", {"start": v(6, 90.3) * mm, "end": v(14, 90.3) * mm});
            skLineSegment(sketch, "E17.0.7.3", {"start": v(6, 82.3) * mm, "end": v(6, 90.3) * mm});
            skLineSegment(sketch, "E17.0.8.0", {"start": v(6, 93.2) * mm, "end": v(14, 93.2) * mm});
            skLineSegment(sketch, "E17.0.8.1", {"start": v(14, 93.2) * mm, "end": v(14, 101.2) * mm});
            skLineSegment(sketch, "E17.0.8.2", {"start": v(6, 101.2) * mm, "end": v(14, 101.2) * mm});
            skLineSegment(sketch, "E17.0.8.3", {"start": v(6, 93.2) * mm, "end": v(6, 101.2) * mm});
            skLineSegment(sketch, "E17.0.9.0", {"start": v(6, 104.1) * mm, "end": v(14, 104.1) * mm});
            skLineSegment(sketch, "E17.0.9.1", {"start": v(14, 104.1) * mm, "end": v(14, 112.1) * mm});
            skLineSegment(sketch, "E17.0.9.2", {"start": v(6, 112.1) * mm, "end": v(14, 112.1) * mm});
            skLineSegment(sketch, "E17.0.9.3", {"start": v(6, 104.1) * mm, "end": v(6, 112.1) * mm});
            skLineSegment(sketch, "E17.0.10.0", {"start": v(6, 115) * mm, "end": v(14, 115) * mm});
            skLineSegment(sketch, "E17.0.10.1", {"start": v(14, 115) * mm, "end": v(14, 123) * mm});
            skLineSegment(sketch, "E17.0.10.2", {"start": v(6, 123) * mm, "end": v(14, 123) * mm});
            skLineSegment(sketch, "E17.0.10.3", {"start": v(6, 115) * mm, "end": v(6, 123) * mm});
            skLineSegment(sketch, "E17.0.11.0", {"start": v(6, 125.9) * mm, "end": v(14, 125.9) * mm});
            skLineSegment(sketch, "E17.0.11.1", {"start": v(14, 125.9) * mm, "end": v(14, 133.9) * mm});
            skLineSegment(sketch, "E17.0.11.2", {"start": v(6, 133.9) * mm, "end": v(14, 133.9) * mm});
            skLineSegment(sketch, "E17.0.11.3", {"start": v(6, 125.9) * mm, "end": v(6, 133.9) * mm});
            skLineSegment(sketch, "E17.1.0.0", {"start": v(16.7, 6) * mm, "end": v(24.7, 6) * mm});
            skLineSegment(sketch, "E17.1.0.1", {"start": v(24.7, 6) * mm, "end": v(24.7, 14) * mm});
            skLineSegment(sketch, "E17.1.0.2", {"start": v(16.7, 14) * mm, "end": v(24.7, 14) * mm});
            skLineSegment(sketch, "E17.1.0.3", {"start": v(16.7, 6) * mm, "end": v(16.7, 14) * mm});
            skLineSegment(sketch, "E17.1.1.0", {"start": v(16.7, 16.9) * mm, "end": v(24.7, 16.9) * mm});
            skLineSegment(sketch, "E17.1.1.1", {"start": v(24.7, 16.9) * mm, "end": v(24.7, 24.9) * mm});
            skLineSegment(sketch, "E17.1.1.2", {"start": v(16.7, 24.9) * mm, "end": v(24.7, 24.9) * mm});
            skLineSegment(sketch, "E17.1.1.3", {"start": v(16.7, 16.9) * mm, "end": v(16.7, 24.9) * mm});
            skLineSegment(sketch, "E17.1.2.0", {"start": v(16.7, 27.8) * mm, "end": v(24.7, 27.8) * mm});
            skLineSegment(sketch, "E17.1.2.1", {"start": v(24.7, 27.8) * mm, "end": v(24.7, 35.8) * mm});
            skLineSegment(sketch, "E17.1.2.2", {"start": v(16.7, 35.8) * mm, "end": v(24.7, 35.8) * mm});
            skLineSegment(sketch, "E17.1.2.3", {"start": v(16.7, 27.8) * mm, "end": v(16.7, 35.8) * mm});
            skLineSegment(sketch, "E17.1.3.0", {"start": v(16.7, 38.7) * mm, "end": v(24.7, 38.7) * mm});
            skLineSegment(sketch, "E17.1.3.1", {"start": v(24.7, 38.7) * mm, "end": v(24.7, 46.7) * mm});
            skLineSegment(sketch, "E17.1.3.2", {"start": v(16.7, 46.7) * mm, "end": v(24.7, 46.7) * mm});
            skLineSegment(sketch, "E17.1.3.3", {"start": v(16.7, 38.7) * mm, "end": v(16.7, 46.7) * mm});
            skLineSegment(sketch, "E17.1.4.0", {"start": v(16.7, 49.6) * mm, "end": v(24.7, 49.6) * mm});
            skLineSegment(sketch, "E17.1.4.1", {"start": v(24.7, 49.6) * mm, "end": v(24.7, 57.6) * mm});
            skLineSegment(sketch, "E17.1.4.2", {"start": v(16.7, 57.6) * mm, "end": v(24.7, 57.6) * mm});
            skLineSegment(sketch, "E17.1.4.3", {"start": v(16.7, 49.6) * mm, "end": v(16.7, 57.6) * mm});
            skLineSegment(sketch, "E17.1.5.0", {"start": v(16.7, 60.5) * mm, "end": v(24.7, 60.5) * mm});
            skLineSegment(sketch, "E17.1.5.1", {"start": v(24.7, 60.5) * mm, "end": v(24.7, 68.5) * mm});
            skLineSegment(sketch, "E17.1.5.2", {"start": v(16.7, 68.5) * mm, "end": v(24.7, 68.5) * mm});
            skLineSegment(sketch, "E17.1.5.3", {"start": v(16.7, 60.5) * mm, "end": v(16.7, 68.5) * mm});
            skLineSegment(sketch, "E17.1.6.0", {"start": v(16.7, 71.4) * mm, "end": v(24.7, 71.4) * mm});
            skLineSegment(sketch, "E17.1.6.1", {"start": v(24.7, 71.4) * mm, "end": v(24.7, 79.4) * mm});
            skLineSegment(sketch, "E17.1.6.2", {"start": v(16.7, 79.4) * mm, "end": v(24.7, 79.4) * mm});
            skLineSegment(sketch, "E17.1.6.3", {"start": v(16.7, 71.4) * mm, "end": v(16.7, 79.4) * mm});
            skLineSegment(sketch, "E17.1.7.0", {"start": v(16.7, 82.3) * mm, "end": v(24.7, 82.3) * mm});
            skLineSegment(sketch, "E17.1.7.1", {"start": v(24.7, 82.3) * mm, "end": v(24.7, 90.3) * mm});
            skLineSegment(sketch, "E17.1.7.2", {"start": v(16.7, 90.3) * mm, "end": v(24.7, 90.3) * mm});
            skLineSegment(sketch, "E17.1.7.3", {"start": v(16.7, 82.3) * mm, "end": v(16.7, 90.3) * mm});
            skLineSegment(sketch, "E17.1.8.0", {"start": v(16.7, 93.2) * mm, "end": v(24.7, 93.2) * mm});
            skLineSegment(sketch, "E17.1.8.1", {"start": v(24.7, 93.2) * mm, "end": v(24.7, 101.2) * mm});
            skLineSegment(sketch, "E17.1.8.2", {"start": v(16.7, 101.2) * mm, "end": v(24.7, 101.2) * mm});
            skLineSegment(sketch, "E17.1.8.3", {"start": v(16.7, 93.2) * mm, "end": v(16.7, 101.2) * mm});
            skLineSegment(sketch, "E17.1.9.0", {"start": v(16.7, 104.1) * mm, "end": v(24.7, 104.1) * mm});
            skLineSegment(sketch, "E17.1.9.1", {"start": v(24.7, 104.1) * mm, "end": v(24.7, 112.1) * mm});
            skLineSegment(sketch, "E17.1.9.2", {"start": v(16.7, 112.1) * mm, "end": v(24.7, 112.1) * mm});
            skLineSegment(sketch, "E17.1.9.3", {"start": v(16.7, 104.1) * mm, "end": v(16.7, 112.1) * mm});
            skLineSegment(sketch, "E17.1.10.0", {"start": v(16.7, 115) * mm, "end": v(24.7, 115) * mm});
            skLineSegment(sketch, "E17.1.10.1", {"start": v(24.7, 115) * mm, "end": v(24.7, 123) * mm});
            skLineSegment(sketch, "E17.1.10.2", {"start": v(16.7, 123) * mm, "end": v(24.7, 123) * mm});
            skLineSegment(sketch, "E17.1.10.3", {"start": v(16.7, 115) * mm, "end": v(16.7, 123) * mm});
            skLineSegment(sketch, "E17.1.11.0", {"start": v(16.7, 125.9) * mm, "end": v(24.7, 125.9) * mm});
            skLineSegment(sketch, "E17.1.11.1", {"start": v(24.7, 125.9) * mm, "end": v(24.7, 133.9) * mm});
            skLineSegment(sketch, "E17.1.11.2", {"start": v(16.7, 133.9) * mm, "end": v(24.7, 133.9) * mm});
            skLineSegment(sketch, "E17.1.11.3", {"start": v(16.7, 125.9) * mm, "end": v(16.7, 133.9) * mm});
            skLineSegment(sketch, "E17.2.0.0", {"start": v(27.4, 6) * mm, "end": v(35.4, 6) * mm});
            skLineSegment(sketch, "E17.2.0.1", {"start": v(35.4, 6) * mm, "end": v(35.4, 14) * mm});
            skLineSegment(sketch, "E17.2.0.2", {"start": v(27.4, 14) * mm, "end": v(35.4, 14) * mm});
            skLineSegment(sketch, "E17.2.0.3", {"start": v(27.4, 6) * mm, "end": v(27.4, 14) * mm});
            skLineSegment(sketch, "E17.2.1.0", {"start": v(27.4, 16.9) * mm, "end": v(35.4, 16.9) * mm});
            skLineSegment(sketch, "E17.2.1.1", {"start": v(35.4, 16.9) * mm, "end": v(35.4, 24.9) * mm});
            skLineSegment(sketch, "E17.2.1.2", {"start": v(27.4, 24.9) * mm, "end": v(35.4, 24.9) * mm});
            skLineSegment(sketch, "E17.2.1.3", {"start": v(27.4, 16.9) * mm, "end": v(27.4, 24.9) * mm});
            skLineSegment(sketch, "E17.2.2.0", {"start": v(27.4, 27.8) * mm, "end": v(35.4, 27.8) * mm});
            skLineSegment(sketch, "E17.2.2.1", {"start": v(35.4, 27.8) * mm, "end": v(35.4, 35.8) * mm});
            skLineSegment(sketch, "E17.2.2.2", {"start": v(27.4, 35.8) * mm, "end": v(35.4, 35.8) * mm});
            skLineSegment(sketch, "E17.2.2.3", {"start": v(27.4, 27.8) * mm, "end": v(27.4, 35.8) * mm});
            skLineSegment(sketch, "E17.2.3.0", {"start": v(27.4, 38.7) * mm, "end": v(35.4, 38.7) * mm});
            skLineSegment(sketch, "E17.2.3.1", {"start": v(35.4, 38.7) * mm, "end": v(35.4, 46.7) * mm});
            skLineSegment(sketch, "E17.2.3.2", {"start": v(27.4, 46.7) * mm, "end": v(35.4, 46.7) * mm});
            skLineSegment(sketch, "E17.2.3.3", {"start": v(27.4, 38.7) * mm, "end": v(27.4, 46.7) * mm});
            skLineSegment(sketch, "E17.2.4.0", {"start": v(27.4, 49.6) * mm, "end": v(35.4, 49.6) * mm});
            skLineSegment(sketch, "E17.2.4.1", {"start": v(35.4, 49.6) * mm, "end": v(35.4, 57.6) * mm});
            skLineSegment(sketch, "E17.2.4.2", {"start": v(27.4, 57.6) * mm, "end": v(35.4, 57.6) * mm});
            skLineSegment(sketch, "E17.2.4.3", {"start": v(27.4, 49.6) * mm, "end": v(27.4, 57.6) * mm});
            skLineSegment(sketch, "E17.2.5.0", {"start": v(27.4, 60.5) * mm, "end": v(35.4, 60.5) * mm});
            skLineSegment(sketch, "E17.2.5.1", {"start": v(35.4, 60.5) * mm, "end": v(35.4, 68.5) * mm});
            skLineSegment(sketch, "E17.2.5.2", {"start": v(27.4, 68.5) * mm, "end": v(35.4, 68.5) * mm});
            skLineSegment(sketch, "E17.2.5.3", {"start": v(27.4, 60.5) * mm, "end": v(27.4, 68.5) * mm});
            skLineSegment(sketch, "E17.2.6.0", {"start": v(27.4, 71.4) * mm, "end": v(35.4, 71.4) * mm});
            skLineSegment(sketch, "E17.2.6.1", {"start": v(35.4, 71.4) * mm, "end": v(35.4, 79.4) * mm});
            skLineSegment(sketch, "E17.2.6.2", {"start": v(27.4, 79.4) * mm, "end": v(35.4, 79.4) * mm});
            skLineSegment(sketch, "E17.2.6.3", {"start": v(27.4, 71.4) * mm, "end": v(27.4, 79.4) * mm});
            skLineSegment(sketch, "E17.2.7.0", {"start": v(27.4, 82.3) * mm, "end": v(35.4, 82.3) * mm});
            skLineSegment(sketch, "E17.2.7.1", {"start": v(35.4, 82.3) * mm, "end": v(35.4, 90.3) * mm});
            skLineSegment(sketch, "E17.2.7.2", {"start": v(27.4, 90.3) * mm, "end": v(35.4, 90.3) * mm});
            skLineSegment(sketch, "E17.2.7.3", {"start": v(27.4, 82.3) * mm, "end": v(27.4, 90.3) * mm});
            skLineSegment(sketch, "E17.2.8.0", {"start": v(27.4, 93.2) * mm, "end": v(35.4, 93.2) * mm});
            skLineSegment(sketch, "E17.2.8.1", {"start": v(35.4, 93.2) * mm, "end": v(35.4, 101.2) * mm});
            skLineSegment(sketch, "E17.2.8.2", {"start": v(27.4, 101.2) * mm, "end": v(35.4, 101.2) * mm});
            skLineSegment(sketch, "E17.2.8.3", {"start": v(27.4, 93.2) * mm, "end": v(27.4, 101.2) * mm});
            skLineSegment(sketch, "E17.2.9.0", {"start": v(27.4, 104.1) * mm, "end": v(35.4, 104.1) * mm});
            skLineSegment(sketch, "E17.2.9.1", {"start": v(35.4, 104.1) * mm, "end": v(35.4, 112.1) * mm});
            skLineSegment(sketch, "E17.2.9.2", {"start": v(27.4, 112.1) * mm, "end": v(35.4, 112.1) * mm});
            skLineSegment(sketch, "E17.2.9.3", {"start": v(27.4, 104.1) * mm, "end": v(27.4, 112.1) * mm});
            skLineSegment(sketch, "E17.2.10.0", {"start": v(27.4, 115) * mm, "end": v(35.4, 115) * mm});
            skLineSegment(sketch, "E17.2.10.1", {"start": v(35.4, 115) * mm, "end": v(35.4, 123) * mm});
            skLineSegment(sketch, "E17.2.10.2", {"start": v(27.4, 123) * mm, "end": v(35.4, 123) * mm});
            skLineSegment(sketch, "E17.2.10.3", {"start": v(27.4, 115) * mm, "end": v(27.4, 123) * mm});
            skLineSegment(sketch, "E17.2.11.0", {"start": v(27.4, 125.9) * mm, "end": v(35.4, 125.9) * mm});
            skLineSegment(sketch, "E17.2.11.1", {"start": v(35.4, 125.9) * mm, "end": v(35.4, 133.9) * mm});
            skLineSegment(sketch, "E17.2.11.2", {"start": v(27.4, 133.9) * mm, "end": v(35.4, 133.9) * mm});
            skLineSegment(sketch, "E17.2.11.3", {"start": v(27.4, 125.9) * mm, "end": v(27.4, 133.9) * mm});
            skLineSegment(sketch, "E17.3.0.0", {"start": v(38.1, 6) * mm, "end": v(46.1, 6) * mm});
            skLineSegment(sketch, "E17.3.0.1", {"start": v(46.1, 6) * mm, "end": v(46.1, 14) * mm});
            skLineSegment(sketch, "E17.3.0.2", {"start": v(38.1, 14) * mm, "end": v(46.1, 14) * mm});
            skLineSegment(sketch, "E17.3.0.3", {"start": v(38.1, 6) * mm, "end": v(38.1, 14) * mm});
            skLineSegment(sketch, "E17.3.1.0", {"start": v(38.1, 16.9) * mm, "end": v(46.1, 16.9) * mm});
            skLineSegment(sketch, "E17.3.1.1", {"start": v(46.1, 16.9) * mm, "end": v(46.1, 24.9) * mm});
            skLineSegment(sketch, "E17.3.1.2", {"start": v(38.1, 24.9) * mm, "end": v(46.1, 24.9) * mm});
            skLineSegment(sketch, "E17.3.1.3", {"start": v(38.1, 16.9) * mm, "end": v(38.1, 24.9) * mm});
            skLineSegment(sketch, "E17.3.2.0", {"start": v(38.1, 27.8) * mm, "end": v(46.1, 27.8) * mm});
            skLineSegment(sketch, "E17.3.2.1", {"start": v(46.1, 27.8) * mm, "end": v(46.1, 35.8) * mm});
            skLineSegment(sketch, "E17.3.2.2", {"start": v(38.1, 35.8) * mm, "end": v(46.1, 35.8) * mm});
            skLineSegment(sketch, "E17.3.2.3", {"start": v(38.1, 27.8) * mm, "end": v(38.1, 35.8) * mm});
            skLineSegment(sketch, "E17.3.3.0", {"start": v(38.1, 38.7) * mm, "end": v(46.1, 38.7) * mm});
            skLineSegment(sketch, "E17.3.3.1", {"start": v(46.1, 38.7) * mm, "end": v(46.1, 46.7) * mm});
            skLineSegment(sketch, "E17.3.3.2", {"start": v(38.1, 46.7) * mm, "end": v(46.1, 46.7) * mm});
            skLineSegment(sketch, "E17.3.3.3", {"start": v(38.1, 38.7) * mm, "end": v(38.1, 46.7) * mm});
            skLineSegment(sketch, "E17.3.4.0", {"start": v(38.1, 49.6) * mm, "end": v(46.1, 49.6) * mm});
            skLineSegment(sketch, "E17.3.4.1", {"start": v(46.1, 49.6) * mm, "end": v(46.1, 57.6) * mm});
            skLineSegment(sketch, "E17.3.4.2", {"start": v(38.1, 57.6) * mm, "end": v(46.1, 57.6) * mm});
            skLineSegment(sketch, "E17.3.4.3", {"start": v(38.1, 49.6) * mm, "end": v(38.1, 57.6) * mm});
            skLineSegment(sketch, "E17.3.5.0", {"start": v(38.1, 60.5) * mm, "end": v(46.1, 60.5) * mm});
            skLineSegment(sketch, "E17.3.5.1", {"start": v(46.1, 60.5) * mm, "end": v(46.1, 68.5) * mm});
            skLineSegment(sketch, "E17.3.5.2", {"start": v(38.1, 68.5) * mm, "end": v(46.1, 68.5) * mm});
            skLineSegment(sketch, "E17.3.5.3", {"start": v(38.1, 60.5) * mm, "end": v(38.1, 68.5) * mm});
            skLineSegment(sketch, "E17.3.6.0", {"start": v(38.1, 71.4) * mm, "end": v(46.1, 71.4) * mm});
            skLineSegment(sketch, "E17.3.6.1", {"start": v(46.1, 71.4) * mm, "end": v(46.1, 79.4) * mm});
            skLineSegment(sketch, "E17.3.6.2", {"start": v(38.1, 79.4) * mm, "end": v(46.1, 79.4) * mm});
            skLineSegment(sketch, "E17.3.6.3", {"start": v(38.1, 71.4) * mm, "end": v(38.1, 79.4) * mm});
            skLineSegment(sketch, "E17.3.7.0", {"start": v(38.1, 82.3) * mm, "end": v(46.1, 82.3) * mm});
            skLineSegment(sketch, "E17.3.7.1", {"start": v(46.1, 82.3) * mm, "end": v(46.1, 90.3) * mm});
            skLineSegment(sketch, "E17.3.7.2", {"start": v(38.1, 90.3) * mm, "end": v(46.1, 90.3) * mm});
            skLineSegment(sketch, "E17.3.7.3", {"start": v(38.1, 82.3) * mm, "end": v(38.1, 90.3) * mm});
            skLineSegment(sketch, "E17.3.8.0", {"start": v(38.1, 93.2) * mm, "end": v(46.1, 93.2) * mm});
            skLineSegment(sketch, "E17.3.8.1", {"start": v(46.1, 93.2) * mm, "end": v(46.1, 101.2) * mm});
            skLineSegment(sketch, "E17.3.8.2", {"start": v(38.1, 101.2) * mm, "end": v(46.1, 101.2) * mm});
            skLineSegment(sketch, "E17.3.8.3", {"start": v(38.1, 93.2) * mm, "end": v(38.1, 101.2) * mm});
            skLineSegment(sketch, "E17.3.9.0", {"start": v(38.1, 104.1) * mm, "end": v(46.1, 104.1) * mm});
            skLineSegment(sketch, "E17.3.9.1", {"start": v(46.1, 104.1) * mm, "end": v(46.1, 112.1) * mm});
            skLineSegment(sketch, "E17.3.9.2", {"start": v(38.1, 112.1) * mm, "end": v(46.1, 112.1) * mm});
            skLineSegment(sketch, "E17.3.9.3", {"start": v(38.1, 104.1) * mm, "end": v(38.1, 112.1) * mm});
            skLineSegment(sketch, "E17.3.10.0", {"start": v(38.1, 115) * mm, "end": v(46.1, 115) * mm});
            skLineSegment(sketch, "E17.3.10.1", {"start": v(46.1, 115) * mm, "end": v(46.1, 123) * mm});
            skLineSegment(sketch, "E17.3.10.2", {"start": v(38.1, 123) * mm, "end": v(46.1, 123) * mm});
            skLineSegment(sketch, "E17.3.10.3", {"start": v(38.1, 115) * mm, "end": v(38.1, 123) * mm});
            skLineSegment(sketch, "E17.3.11.0", {"start": v(38.1, 125.9) * mm, "end": v(46.1, 125.9) * mm});
            skLineSegment(sketch, "E17.3.11.1", {"start": v(46.1, 125.9) * mm, "end": v(46.1, 133.9) * mm});
            skLineSegment(sketch, "E17.3.11.2", {"start": v(38.1, 133.9) * mm, "end": v(46.1, 133.9) * mm});
            skLineSegment(sketch, "E17.3.11.3", {"start": v(38.1, 125.9) * mm, "end": v(38.1, 133.9) * mm});
            skLineSegment(sketch, "E17.4.0.0", {"start": v(48.8, 6) * mm, "end": v(56.8, 6) * mm});
            skLineSegment(sketch, "E17.4.0.1", {"start": v(56.8, 6) * mm, "end": v(56.8, 14) * mm});
            skLineSegment(sketch, "E17.4.0.2", {"start": v(48.8, 14) * mm, "end": v(56.8, 14) * mm});
            skLineSegment(sketch, "E17.4.0.3", {"start": v(48.8, 6) * mm, "end": v(48.8, 14) * mm});
            skLineSegment(sketch, "E17.4.1.0", {"start": v(48.8, 16.9) * mm, "end": v(56.8, 16.9) * mm});
            skLineSegment(sketch, "E17.4.1.1", {"start": v(56.8, 16.9) * mm, "end": v(56.8, 24.9) * mm});
            skLineSegment(sketch, "E17.4.1.2", {"start": v(48.8, 24.9) * mm, "end": v(56.8, 24.9) * mm});
            skLineSegment(sketch, "E17.4.1.3", {"start": v(48.8, 16.9) * mm, "end": v(48.8, 24.9) * mm});
            skLineSegment(sketch, "E17.4.2.0", {"start": v(48.8, 27.8) * mm, "end": v(56.8, 27.8) * mm});
            skLineSegment(sketch, "E17.4.2.1", {"start": v(56.8, 27.8) * mm, "end": v(56.8, 35.8) * mm});
            skLineSegment(sketch, "E17.4.2.2", {"start": v(48.8, 35.8) * mm, "end": v(56.8, 35.8) * mm});
            skLineSegment(sketch, "E17.4.2.3", {"start": v(48.8, 27.8) * mm, "end": v(48.8, 35.8) * mm});
            skLineSegment(sketch, "E17.4.3.0", {"start": v(48.8, 38.7) * mm, "end": v(56.8, 38.7) * mm});
            skLineSegment(sketch, "E17.4.3.1", {"start": v(56.8, 38.7) * mm, "end": v(56.8, 46.7) * mm});
            skLineSegment(sketch, "E17.4.3.2", {"start": v(48.8, 46.7) * mm, "end": v(56.8, 46.7) * mm});
            skLineSegment(sketch, "E17.4.3.3", {"start": v(48.8, 38.7) * mm, "end": v(48.8, 46.7) * mm});
            skLineSegment(sketch, "E17.4.4.0", {"start": v(48.8, 49.6) * mm, "end": v(56.8, 49.6) * mm});
            skLineSegment(sketch, "E17.4.4.1", {"start": v(56.8, 49.6) * mm, "end": v(56.8, 57.6) * mm});
            skLineSegment(sketch, "E17.4.4.2", {"start": v(48.8, 57.6) * mm, "end": v(56.8, 57.6) * mm});
            skLineSegment(sketch, "E17.4.4.3", {"start": v(48.8, 49.6) * mm, "end": v(48.8, 57.6) * mm});
            skLineSegment(sketch, "E17.4.5.0", {"start": v(48.8, 60.5) * mm, "end": v(56.8, 60.5) * mm});
            skLineSegment(sketch, "E17.4.5.1", {"start": v(56.8, 60.5) * mm, "end": v(56.8, 68.5) * mm});
            skLineSegment(sketch, "E17.4.5.2", {"start": v(48.8, 68.5) * mm, "end": v(56.8, 68.5) * mm});
            skLineSegment(sketch, "E17.4.5.3", {"start": v(48.8, 60.5) * mm, "end": v(48.8, 68.5) * mm});
            skLineSegment(sketch, "E17.4.6.0", {"start": v(48.8, 71.4) * mm, "end": v(56.8, 71.4) * mm});
            skLineSegment(sketch, "E17.4.6.1", {"start": v(56.8, 71.4) * mm, "end": v(56.8, 79.4) * mm});
            skLineSegment(sketch, "E17.4.6.2", {"start": v(48.8, 79.4) * mm, "end": v(56.8, 79.4) * mm});
            skLineSegment(sketch, "E17.4.6.3", {"start": v(48.8, 71.4) * mm, "end": v(48.8, 79.4) * mm});
            skLineSegment(sketch, "E17.4.7.0", {"start": v(48.8, 82.3) * mm, "end": v(56.8, 82.3) * mm});
            skLineSegment(sketch, "E17.4.7.1", {"start": v(56.8, 82.3) * mm, "end": v(56.8, 90.3) * mm});
            skLineSegment(sketch, "E17.4.7.2", {"start": v(48.8, 90.3) * mm, "end": v(56.8, 90.3) * mm});
            skLineSegment(sketch, "E17.4.7.3", {"start": v(48.8, 82.3) * mm, "end": v(48.8, 90.3) * mm});
            skLineSegment(sketch, "E17.4.8.0", {"start": v(48.8, 93.2) * mm, "end": v(56.8, 93.2) * mm});
            skLineSegment(sketch, "E17.4.8.1", {"start": v(56.8, 93.2) * mm, "end": v(56.8, 101.2) * mm});
            skLineSegment(sketch, "E17.4.8.2", {"start": v(48.8, 101.2) * mm, "end": v(56.8, 101.2) * mm});
            skLineSegment(sketch, "E17.4.8.3", {"start": v(48.8, 93.2) * mm, "end": v(48.8, 101.2) * mm});
            skLineSegment(sketch, "E17.4.9.0", {"start": v(48.8, 104.1) * mm, "end": v(56.8, 104.1) * mm});
            skLineSegment(sketch, "E17.4.9.1", {"start": v(56.8, 104.1) * mm, "end": v(56.8, 112.1) * mm});
            skLineSegment(sketch, "E17.4.9.2", {"start": v(48.8, 112.1) * mm, "end": v(56.8, 112.1) * mm});
            skLineSegment(sketch, "E17.4.9.3", {"start": v(48.8, 104.1) * mm, "end": v(48.8, 112.1) * mm});
            skLineSegment(sketch, "E17.4.10.0", {"start": v(48.8, 115) * mm, "end": v(56.8, 115) * mm});
            skLineSegment(sketch, "E17.4.10.1", {"start": v(56.8, 115) * mm, "end": v(56.8, 123) * mm});
            skLineSegment(sketch, "E17.4.10.2", {"start": v(48.8, 123) * mm, "end": v(56.8, 123) * mm});
            skLineSegment(sketch, "E17.4.10.3", {"start": v(48.8, 115) * mm, "end": v(48.8, 123) * mm});
            skLineSegment(sketch, "E17.4.11.0", {"start": v(48.8, 125.9) * mm, "end": v(56.8, 125.9) * mm});
            skLineSegment(sketch, "E17.4.11.1", {"start": v(56.8, 125.9) * mm, "end": v(56.8, 133.9) * mm});
            skLineSegment(sketch, "E17.4.11.2", {"start": v(48.8, 133.9) * mm, "end": v(56.8, 133.9) * mm});
            skLineSegment(sketch, "E17.4.11.3", {"start": v(48.8, 125.9) * mm, "end": v(48.8, 133.9) * mm});
            skLineSegment(sketch, "E17.5.0.0", {"start": v(59.5, 6) * mm, "end": v(67.5, 6) * mm});
            skLineSegment(sketch, "E17.5.0.1", {"start": v(67.5, 6) * mm, "end": v(67.5, 14) * mm});
            skLineSegment(sketch, "E17.5.0.2", {"start": v(59.5, 14) * mm, "end": v(67.5, 14) * mm});
            skLineSegment(sketch, "E17.5.0.3", {"start": v(59.5, 6) * mm, "end": v(59.5, 14) * mm});
            skLineSegment(sketch, "E17.5.1.0", {"start": v(59.5, 16.9) * mm, "end": v(67.5, 16.9) * mm});
            skLineSegment(sketch, "E17.5.1.1", {"start": v(67.5, 16.9) * mm, "end": v(67.5, 24.9) * mm});
            skLineSegment(sketch, "E17.5.1.2", {"start": v(59.5, 24.9) * mm, "end": v(67.5, 24.9) * mm});
            skLineSegment(sketch, "E17.5.1.3", {"start": v(59.5, 16.9) * mm, "end": v(59.5, 24.9) * mm});
            skLineSegment(sketch, "E17.5.2.0", {"start": v(59.5, 27.8) * mm, "end": v(67.5, 27.8) * mm});
            skLineSegment(sketch, "E17.5.2.1", {"start": v(67.5, 27.8) * mm, "end": v(67.5, 35.8) * mm});
            skLineSegment(sketch, "E17.5.2.2", {"start": v(59.5, 35.8) * mm, "end": v(67.5, 35.8) * mm});
            skLineSegment(sketch, "E17.5.2.3", {"start": v(59.5, 27.8) * mm, "end": v(59.5, 35.8) * mm});
            skLineSegment(sketch, "E17.5.3.0", {"start": v(59.5, 38.7) * mm, "end": v(67.5, 38.7) * mm});
            skLineSegment(sketch, "E17.5.3.1", {"start": v(67.5, 38.7) * mm, "end": v(67.5, 46.7) * mm});
            skLineSegment(sketch, "E17.5.3.2", {"start": v(59.5, 46.7) * mm, "end": v(67.5, 46.7) * mm});
            skLineSegment(sketch, "E17.5.3.3", {"start": v(59.5, 38.7) * mm, "end": v(59.5, 46.7) * mm});
            skLineSegment(sketch, "E17.5.4.0", {"start": v(59.5, 49.6) * mm, "end": v(67.5, 49.6) * mm});
            skLineSegment(sketch, "E17.5.4.1", {"start": v(67.5, 49.6) * mm, "end": v(67.5, 57.6) * mm});
            skLineSegment(sketch, "E17.5.4.2", {"start": v(59.5, 57.6) * mm, "end": v(67.5, 57.6) * mm});
            skLineSegment(sketch, "E17.5.4.3", {"start": v(59.5, 49.6) * mm, "end": v(59.5, 57.6) * mm});
            skLineSegment(sketch, "E17.5.5.0", {"start": v(59.5, 60.5) * mm, "end": v(67.5, 60.5) * mm});
            skLineSegment(sketch, "E17.5.5.1", {"start": v(67.5, 60.5) * mm, "end": v(67.5, 68.5) * mm});
            skLineSegment(sketch, "E17.5.5.2", {"start": v(59.5, 68.5) * mm, "end": v(67.5, 68.5) * mm});
            skLineSegment(sketch, "E17.5.5.3", {"start": v(59.5, 60.5) * mm, "end": v(59.5, 68.5) * mm});
            skLineSegment(sketch, "E17.5.6.0", {"start": v(59.5, 71.4) * mm, "end": v(67.5, 71.4) * mm});
            skLineSegment(sketch, "E17.5.6.1", {"start": v(67.5, 71.4) * mm, "end": v(67.5, 79.4) * mm});
            skLineSegment(sketch, "E17.5.6.2", {"start": v(59.5, 79.4) * mm, "end": v(67.5, 79.4) * mm});
            skLineSegment(sketch, "E17.5.6.3", {"start": v(59.5, 71.4) * mm, "end": v(59.5, 79.4) * mm});
            skLineSegment(sketch, "E17.5.7.0", {"start": v(59.5, 82.3) * mm, "end": v(67.5, 82.3) * mm});
            skLineSegment(sketch, "E17.5.7.1", {"start": v(67.5, 82.3) * mm, "end": v(67.5, 90.3) * mm});
            skLineSegment(sketch, "E17.5.7.2", {"start": v(59.5, 90.3) * mm, "end": v(67.5, 90.3) * mm});
            skLineSegment(sketch, "E17.5.7.3", {"start": v(59.5, 82.3) * mm, "end": v(59.5, 90.3) * mm});
            skLineSegment(sketch, "E17.5.8.0", {"start": v(59.5, 93.2) * mm, "end": v(67.5, 93.2) * mm});
            skLineSegment(sketch, "E17.5.8.1", {"start": v(67.5, 93.2) * mm, "end": v(67.5, 101.2) * mm});
            skLineSegment(sketch, "E17.5.8.2", {"start": v(59.5, 101.2) * mm, "end": v(67.5, 101.2) * mm});
            skLineSegment(sketch, "E17.5.8.3", {"start": v(59.5, 93.2) * mm, "end": v(59.5, 101.2) * mm});
            skLineSegment(sketch, "E17.5.9.0", {"start": v(59.5, 104.1) * mm, "end": v(67.5, 104.1) * mm});
            skLineSegment(sketch, "E17.5.9.1", {"start": v(67.5, 104.1) * mm, "end": v(67.5, 112.1) * mm});
            skLineSegment(sketch, "E17.5.9.2", {"start": v(59.5, 112.1) * mm, "end": v(67.5, 112.1) * mm});
            skLineSegment(sketch, "E17.5.9.3", {"start": v(59.5, 104.1) * mm, "end": v(59.5, 112.1) * mm});
            skLineSegment(sketch, "E17.5.10.0", {"start": v(59.5, 115) * mm, "end": v(67.5, 115) * mm});
            skLineSegment(sketch, "E17.5.10.1", {"start": v(67.5, 115) * mm, "end": v(67.5, 123) * mm});
            skLineSegment(sketch, "E17.5.10.2", {"start": v(59.5, 123) * mm, "end": v(67.5, 123) * mm});
            skLineSegment(sketch, "E17.5.10.3", {"start": v(59.5, 115) * mm, "end": v(59.5, 123) * mm});
            skLineSegment(sketch, "E17.5.11.0", {"start": v(59.5, 125.9) * mm, "end": v(67.5, 125.9) * mm});
            skLineSegment(sketch, "E17.5.11.1", {"start": v(67.5, 125.9) * mm, "end": v(67.5, 133.9) * mm});
            skLineSegment(sketch, "E17.5.11.2", {"start": v(59.5, 133.9) * mm, "end": v(67.5, 133.9) * mm});
            skLineSegment(sketch, "E17.5.11.3", {"start": v(59.5, 125.9) * mm, "end": v(59.5, 133.9) * mm});
            skLineSegment(sketch, "E17.6.0.0", {"start": v(70.2, 6) * mm, "end": v(78.2, 6) * mm});
            skLineSegment(sketch, "E17.6.0.1", {"start": v(78.2, 6) * mm, "end": v(78.2, 14) * mm});
            skLineSegment(sketch, "E17.6.0.2", {"start": v(70.2, 14) * mm, "end": v(78.2, 14) * mm});
            skLineSegment(sketch, "E17.6.0.3", {"start": v(70.2, 6) * mm, "end": v(70.2, 14) * mm});
            skLineSegment(sketch, "E17.6.1.0", {"start": v(70.2, 16.9) * mm, "end": v(78.2, 16.9) * mm});
            skLineSegment(sketch, "E17.6.1.1", {"start": v(78.2, 16.9) * mm, "end": v(78.2, 24.9) * mm});
            skLineSegment(sketch, "E17.6.1.2", {"start": v(70.2, 24.9) * mm, "end": v(78.2, 24.9) * mm});
            skLineSegment(sketch, "E17.6.1.3", {"start": v(70.2, 16.9) * mm, "end": v(70.2, 24.9) * mm});
            skLineSegment(sketch, "E17.6.2.0", {"start": v(70.2, 27.8) * mm, "end": v(78.2, 27.8) * mm});
            skLineSegment(sketch, "E17.6.2.1", {"start": v(78.2, 27.8) * mm, "end": v(78.2, 35.8) * mm});
            skLineSegment(sketch, "E17.6.2.2", {"start": v(70.2, 35.8) * mm, "end": v(78.2, 35.8) * mm});
            skLineSegment(sketch, "E17.6.2.3", {"start": v(70.2, 27.8) * mm, "end": v(70.2, 35.8) * mm});
            skLineSegment(sketch, "E17.6.3.0", {"start": v(70.2, 38.7) * mm, "end": v(78.2, 38.7) * mm});
            skLineSegment(sketch, "E17.6.3.1", {"start": v(78.2, 38.7) * mm, "end": v(78.2, 46.7) * mm});
            skLineSegment(sketch, "E17.6.3.2", {"start": v(70.2, 46.7) * mm, "end": v(78.2, 46.7) * mm});
            skLineSegment(sketch, "E17.6.3.3", {"start": v(70.2, 38.7) * mm, "end": v(70.2, 46.7) * mm});
            skLineSegment(sketch, "E17.6.4.0", {"start": v(70.2, 49.6) * mm, "end": v(78.2, 49.6) * mm});
            skLineSegment(sketch, "E17.6.4.1", {"start": v(78.2, 49.6) * mm, "end": v(78.2, 57.6) * mm});
            skLineSegment(sketch, "E17.6.4.2", {"start": v(70.2, 57.6) * mm, "end": v(78.2, 57.6) * mm});
            skLineSegment(sketch, "E17.6.4.3", {"start": v(70.2, 49.6) * mm, "end": v(70.2, 57.6) * mm});
            skLineSegment(sketch, "E17.6.5.0", {"start": v(70.2, 60.5) * mm, "end": v(78.2, 60.5) * mm});
            skLineSegment(sketch, "E17.6.5.1", {"start": v(78.2, 60.5) * mm, "end": v(78.2, 68.5) * mm});
            skLineSegment(sketch, "E17.6.5.2", {"start": v(70.2, 68.5) * mm, "end": v(78.2, 68.5) * mm});
            skLineSegment(sketch, "E17.6.5.3", {"start": v(70.2, 60.5) * mm, "end": v(70.2, 68.5) * mm});
            skLineSegment(sketch, "E17.6.6.0", {"start": v(70.2, 71.4) * mm, "end": v(78.2, 71.4) * mm});
            skLineSegment(sketch, "E17.6.6.1", {"start": v(78.2, 71.4) * mm, "end": v(78.2, 79.4) * mm});
            skLineSegment(sketch, "E17.6.6.2", {"start": v(70.2, 79.4) * mm, "end": v(78.2, 79.4) * mm});
            skLineSegment(sketch, "E17.6.6.3", {"start": v(70.2, 71.4) * mm, "end": v(70.2, 79.4) * mm});
            skLineSegment(sketch, "E17.6.7.0", {"start": v(70.2, 82.3) * mm, "end": v(78.2, 82.3) * mm});
            skLineSegment(sketch, "E17.6.7.1", {"start": v(78.2, 82.3) * mm, "end": v(78.2, 90.3) * mm});
            skLineSegment(sketch, "E17.6.7.2", {"start": v(70.2, 90.3) * mm, "end": v(78.2, 90.3) * mm});
            skLineSegment(sketch, "E17.6.7.3", {"start": v(70.2, 82.3) * mm, "end": v(70.2, 90.3) * mm});
            skLineSegment(sketch, "E17.6.8.0", {"start": v(70.2, 93.2) * mm, "end": v(78.2, 93.2) * mm});
            skLineSegment(sketch, "E17.6.8.1", {"start": v(78.2, 93.2) * mm, "end": v(78.2, 101.2) * mm});
            skLineSegment(sketch, "E17.6.8.2", {"start": v(70.2, 101.2) * mm, "end": v(78.2, 101.2) * mm});
            skLineSegment(sketch, "E17.6.8.3", {"start": v(70.2, 93.2) * mm, "end": v(70.2, 101.2) * mm});
            skLineSegment(sketch, "E17.6.9.0", {"start": v(70.2, 104.1) * mm, "end": v(78.2, 104.1) * mm});
            skLineSegment(sketch, "E17.6.9.1", {"start": v(78.2, 104.1) * mm, "end": v(78.2, 112.1) * mm});
            skLineSegment(sketch, "E17.6.9.2", {"start": v(70.2, 112.1) * mm, "end": v(78.2, 112.1) * mm});
            skLineSegment(sketch, "E17.6.9.3", {"start": v(70.2, 104.1) * mm, "end": v(70.2, 112.1) * mm});
            skLineSegment(sketch, "E17.6.10.0", {"start": v(70.2, 115) * mm, "end": v(78.2, 115) * mm});
            skLineSegment(sketch, "E17.6.10.1", {"start": v(78.2, 115) * mm, "end": v(78.2, 123) * mm});
            skLineSegment(sketch, "E17.6.10.2", {"start": v(70.2, 123) * mm, "end": v(78.2, 123) * mm});
            skLineSegment(sketch, "E17.6.10.3", {"start": v(70.2, 115) * mm, "end": v(70.2, 123) * mm});
            skLineSegment(sketch, "E17.6.11.0", {"start": v(70.2, 125.9) * mm, "end": v(78.2, 125.9) * mm});
            skLineSegment(sketch, "E17.6.11.1", {"start": v(78.2, 125.9) * mm, "end": v(78.2, 133.9) * mm});
            skLineSegment(sketch, "E17.6.11.2", {"start": v(70.2, 133.9) * mm, "end": v(78.2, 133.9) * mm});
            skLineSegment(sketch, "E17.6.11.3", {"start": v(70.2, 125.9) * mm, "end": v(70.2, 133.9) * mm});
            skLineSegment(sketch, "E17.7.0.0", {"start": v(80.9, 6) * mm, "end": v(88.9, 6) * mm});
            skLineSegment(sketch, "E17.7.0.1", {"start": v(88.9, 6) * mm, "end": v(88.9, 14) * mm});
            skLineSegment(sketch, "E17.7.0.2", {"start": v(80.9, 14) * mm, "end": v(88.9, 14) * mm});
            skLineSegment(sketch, "E17.7.0.3", {"start": v(80.9, 6) * mm, "end": v(80.9, 14) * mm});
            skLineSegment(sketch, "E17.7.1.0", {"start": v(80.9, 16.9) * mm, "end": v(88.9, 16.9) * mm});
            skLineSegment(sketch, "E17.7.1.1", {"start": v(88.9, 16.9) * mm, "end": v(88.9, 24.9) * mm});
            skLineSegment(sketch, "E17.7.1.2", {"start": v(80.9, 24.9) * mm, "end": v(88.9, 24.9) * mm});
            skLineSegment(sketch, "E17.7.1.3", {"start": v(80.9, 16.9) * mm, "end": v(80.9, 24.9) * mm});
            skLineSegment(sketch, "E17.7.2.0", {"start": v(80.9, 27.8) * mm, "end": v(88.9, 27.8) * mm});
            skLineSegment(sketch, "E17.7.2.1", {"start": v(88.9, 27.8) * mm, "end": v(88.9, 35.8) * mm});
            skLineSegment(sketch, "E17.7.2.2", {"start": v(80.9, 35.8) * mm, "end": v(88.9, 35.8) * mm});
            skLineSegment(sketch, "E17.7.2.3", {"start": v(80.9, 27.8) * mm, "end": v(80.9, 35.8) * mm});
            skLineSegment(sketch, "E17.7.3.0", {"start": v(80.9, 38.7) * mm, "end": v(88.9, 38.7) * mm});
            skLineSegment(sketch, "E17.7.3.1", {"start": v(88.9, 38.7) * mm, "end": v(88.9, 46.7) * mm});
            skLineSegment(sketch, "E17.7.3.2", {"start": v(80.9, 46.7) * mm, "end": v(88.9, 46.7) * mm});
            skLineSegment(sketch, "E17.7.3.3", {"start": v(80.9, 38.7) * mm, "end": v(80.9, 46.7) * mm});
            skLineSegment(sketch, "E17.7.4.0", {"start": v(80.9, 49.6) * mm, "end": v(88.9, 49.6) * mm});
            skLineSegment(sketch, "E17.7.4.1", {"start": v(88.9, 49.6) * mm, "end": v(88.9, 57.6) * mm});
            skLineSegment(sketch, "E17.7.4.2", {"start": v(80.9, 57.6) * mm, "end": v(88.9, 57.6) * mm});
            skLineSegment(sketch, "E17.7.4.3", {"start": v(80.9, 49.6) * mm, "end": v(80.9, 57.6) * mm});
            skLineSegment(sketch, "E17.7.5.0", {"start": v(80.9, 60.5) * mm, "end": v(88.9, 60.5) * mm});
            skLineSegment(sketch, "E17.7.5.1", {"start": v(88.9, 60.5) * mm, "end": v(88.9, 68.5) * mm});
            skLineSegment(sketch, "E17.7.5.2", {"start": v(80.9, 68.5) * mm, "end": v(88.9, 68.5) * mm});
            skLineSegment(sketch, "E17.7.5.3", {"start": v(80.9, 60.5) * mm, "end": v(80.9, 68.5) * mm});
            skLineSegment(sketch, "E17.7.6.0", {"start": v(80.9, 71.4) * mm, "end": v(88.9, 71.4) * mm});
            skLineSegment(sketch, "E17.7.6.1", {"start": v(88.9, 71.4) * mm, "end": v(88.9, 79.4) * mm});
            skLineSegment(sketch, "E17.7.6.2", {"start": v(80.9, 79.4) * mm, "end": v(88.9, 79.4) * mm});
            skLineSegment(sketch, "E17.7.6.3", {"start": v(80.9, 71.4) * mm, "end": v(80.9, 79.4) * mm});
            skLineSegment(sketch, "E17.7.7.0", {"start": v(80.9, 82.3) * mm, "end": v(88.9, 82.3) * mm});
            skLineSegment(sketch, "E17.7.7.1", {"start": v(88.9, 82.3) * mm, "end": v(88.9, 90.3) * mm});
            skLineSegment(sketch, "E17.7.7.2", {"start": v(80.9, 90.3) * mm, "end": v(88.9, 90.3) * mm});
            skLineSegment(sketch, "E17.7.7.3", {"start": v(80.9, 82.3) * mm, "end": v(80.9, 90.3) * mm});
            skLineSegment(sketch, "E17.7.8.0", {"start": v(80.9, 93.2) * mm, "end": v(88.9, 93.2) * mm});
            skLineSegment(sketch, "E17.7.8.1", {"start": v(88.9, 93.2) * mm, "end": v(88.9, 101.2) * mm});
            skLineSegment(sketch, "E17.7.8.2", {"start": v(80.9, 101.2) * mm, "end": v(88.9, 101.2) * mm});
            skLineSegment(sketch, "E17.7.8.3", {"start": v(80.9, 93.2) * mm, "end": v(80.9, 101.2) * mm});
            skLineSegment(sketch, "E17.7.9.0", {"start": v(80.9, 104.1) * mm, "end": v(88.9, 104.1) * mm});
            skLineSegment(sketch, "E17.7.9.1", {"start": v(88.9, 104.1) * mm, "end": v(88.9, 112.1) * mm});
            skLineSegment(sketch, "E17.7.9.2", {"start": v(80.9, 112.1) * mm, "end": v(88.9, 112.1) * mm});
            skLineSegment(sketch, "E17.7.9.3", {"start": v(80.9, 104.1) * mm, "end": v(80.9, 112.1) * mm});
            skLineSegment(sketch, "E17.7.10.0", {"start": v(80.9, 115) * mm, "end": v(88.9, 115) * mm});
            skLineSegment(sketch, "E17.7.10.1", {"start": v(88.9, 115) * mm, "end": v(88.9, 123) * mm});
            skLineSegment(sketch, "E17.7.10.2", {"start": v(80.9, 123) * mm, "end": v(88.9, 123) * mm});
            skLineSegment(sketch, "E17.7.10.3", {"start": v(80.9, 115) * mm, "end": v(80.9, 123) * mm});
            skLineSegment(sketch, "E17.7.11.0", {"start": v(80.9, 125.9) * mm, "end": v(88.9, 125.9) * mm});
            skLineSegment(sketch, "E17.7.11.1", {"start": v(88.9, 125.9) * mm, "end": v(88.9, 133.9) * mm});
            skLineSegment(sketch, "E17.7.11.2", {"start": v(80.9, 133.9) * mm, "end": v(88.9, 133.9) * mm});
            skLineSegment(sketch, "E17.7.11.3", {"start": v(80.9, 125.9) * mm, "end": v(80.9, 133.9) * mm});
            skLineSegment(sketch, "E17.8.0.0", {"start": v(91.6, 6) * mm, "end": v(99.6, 6) * mm});
            skLineSegment(sketch, "E17.8.0.1", {"start": v(99.6, 6) * mm, "end": v(99.6, 14) * mm});
            skLineSegment(sketch, "E17.8.0.2", {"start": v(91.6, 14) * mm, "end": v(99.6, 14) * mm});
            skLineSegment(sketch, "E17.8.0.3", {"start": v(91.6, 6) * mm, "end": v(91.6, 14) * mm});
            skLineSegment(sketch, "E17.8.1.0", {"start": v(91.6, 16.9) * mm, "end": v(99.6, 16.9) * mm});
            skLineSegment(sketch, "E17.8.1.1", {"start": v(99.6, 16.9) * mm, "end": v(99.6, 24.9) * mm});
            skLineSegment(sketch, "E17.8.1.2", {"start": v(91.6, 24.9) * mm, "end": v(99.6, 24.9) * mm});
            skLineSegment(sketch, "E17.8.1.3", {"start": v(91.6, 16.9) * mm, "end": v(91.6, 24.9) * mm});
            skLineSegment(sketch, "E17.8.2.0", {"start": v(91.6, 27.8) * mm, "end": v(99.6, 27.8) * mm});
            skLineSegment(sketch, "E17.8.2.1", {"start": v(99.6, 27.8) * mm, "end": v(99.6, 35.8) * mm});
            skLineSegment(sketch, "E17.8.2.2", {"start": v(91.6, 35.8) * mm, "end": v(99.6, 35.8) * mm});
            skLineSegment(sketch, "E17.8.2.3", {"start": v(91.6, 27.8) * mm, "end": v(91.6, 35.8) * mm});
            skLineSegment(sketch, "E17.8.3.0", {"start": v(91.6, 38.7) * mm, "end": v(99.6, 38.7) * mm});
            skLineSegment(sketch, "E17.8.3.1", {"start": v(99.6, 38.7) * mm, "end": v(99.6, 46.7) * mm});
            skLineSegment(sketch, "E17.8.3.2", {"start": v(91.6, 46.7) * mm, "end": v(99.6, 46.7) * mm});
            skLineSegment(sketch, "E17.8.3.3", {"start": v(91.6, 38.7) * mm, "end": v(91.6, 46.7) * mm});
            skLineSegment(sketch, "E17.8.4.0", {"start": v(91.6, 49.6) * mm, "end": v(99.6, 49.6) * mm});
            skLineSegment(sketch, "E17.8.4.1", {"start": v(99.6, 49.6) * mm, "end": v(99.6, 57.6) * mm});
            skLineSegment(sketch, "E17.8.4.2", {"start": v(91.6, 57.6) * mm, "end": v(99.6, 57.6) * mm});
            skLineSegment(sketch, "E17.8.4.3", {"start": v(91.6, 49.6) * mm, "end": v(91.6, 57.6) * mm});
            skLineSegment(sketch, "E17.8.5.0", {"start": v(91.6, 60.5) * mm, "end": v(99.6, 60.5) * mm});
            skLineSegment(sketch, "E17.8.5.1", {"start": v(99.6, 60.5) * mm, "end": v(99.6, 68.5) * mm});
            skLineSegment(sketch, "E17.8.5.2", {"start": v(91.6, 68.5) * mm, "end": v(99.6, 68.5) * mm});
            skLineSegment(sketch, "E17.8.5.3", {"start": v(91.6, 60.5) * mm, "end": v(91.6, 68.5) * mm});
            skLineSegment(sketch, "E17.8.6.0", {"start": v(91.6, 71.4) * mm, "end": v(99.6, 71.4) * mm});
            skLineSegment(sketch, "E17.8.6.1", {"start": v(99.6, 71.4) * mm, "end": v(99.6, 79.4) * mm});
            skLineSegment(sketch, "E17.8.6.2", {"start": v(91.6, 79.4) * mm, "end": v(99.6, 79.4) * mm});
            skLineSegment(sketch, "E17.8.6.3", {"start": v(91.6, 71.4) * mm, "end": v(91.6, 79.4) * mm});
            skLineSegment(sketch, "E17.8.7.0", {"start": v(91.6, 82.3) * mm, "end": v(99.6, 82.3) * mm});
            skLineSegment(sketch, "E17.8.7.1", {"start": v(99.6, 82.3) * mm, "end": v(99.6, 90.3) * mm});
            skLineSegment(sketch, "E17.8.7.2", {"start": v(91.6, 90.3) * mm, "end": v(99.6, 90.3) * mm});
            skLineSegment(sketch, "E17.8.7.3", {"start": v(91.6, 82.3) * mm, "end": v(91.6, 90.3) * mm});
            skLineSegment(sketch, "E17.8.8.0", {"start": v(91.6, 93.2) * mm, "end": v(99.6, 93.2) * mm});
            skLineSegment(sketch, "E17.8.8.1", {"start": v(99.6, 93.2) * mm, "end": v(99.6, 101.2) * mm});
            skLineSegment(sketch, "E17.8.8.2", {"start": v(91.6, 101.2) * mm, "end": v(99.6, 101.2) * mm});
            skLineSegment(sketch, "E17.8.8.3", {"start": v(91.6, 93.2) * mm, "end": v(91.6, 101.2) * mm});
            skLineSegment(sketch, "E17.8.9.0", {"start": v(91.6, 104.1) * mm, "end": v(99.6, 104.1) * mm});
            skLineSegment(sketch, "E17.8.9.1", {"start": v(99.6, 104.1) * mm, "end": v(99.6, 112.1) * mm});
            skLineSegment(sketch, "E17.8.9.2", {"start": v(91.6, 112.1) * mm, "end": v(99.6, 112.1) * mm});
            skLineSegment(sketch, "E17.8.9.3", {"start": v(91.6, 104.1) * mm, "end": v(91.6, 112.1) * mm});
            skLineSegment(sketch, "E17.8.10.0", {"start": v(91.6, 115) * mm, "end": v(99.6, 115) * mm});
            skLineSegment(sketch, "E17.8.10.1", {"start": v(99.6, 115) * mm, "end": v(99.6, 123) * mm});
            skLineSegment(sketch, "E17.8.10.2", {"start": v(91.6, 123) * mm, "end": v(99.6, 123) * mm});
            skLineSegment(sketch, "E17.8.10.3", {"start": v(91.6, 115) * mm, "end": v(91.6, 123) * mm});
            skLineSegment(sketch, "E17.8.11.0", {"start": v(91.6, 125.9) * mm, "end": v(99.6, 125.9) * mm});
            skLineSegment(sketch, "E17.8.11.1", {"start": v(99.6, 125.9) * mm, "end": v(99.6, 133.9) * mm});
            skLineSegment(sketch, "E17.8.11.2", {"start": v(91.6, 133.9) * mm, "end": v(99.6, 133.9) * mm});
            skLineSegment(sketch, "E17.8.11.3", {"start": v(91.6, 125.9) * mm, "end": v(91.6, 133.9) * mm});
            skLineSegment(sketch, "E17.9.0.0", {"start": v(102.3, 6) * mm, "end": v(110.3, 6) * mm});
            skLineSegment(sketch, "E17.9.0.1", {"start": v(110.3, 6) * mm, "end": v(110.3, 14) * mm});
            skLineSegment(sketch, "E17.9.0.2", {"start": v(102.3, 14) * mm, "end": v(110.3, 14) * mm});
            skLineSegment(sketch, "E17.9.0.3", {"start": v(102.3, 6) * mm, "end": v(102.3, 14) * mm});
            skLineSegment(sketch, "E17.9.1.0", {"start": v(102.3, 16.9) * mm, "end": v(110.3, 16.9) * mm});
            skLineSegment(sketch, "E17.9.1.1", {"start": v(110.3, 16.9) * mm, "end": v(110.3, 24.9) * mm});
            skLineSegment(sketch, "E17.9.1.2", {"start": v(102.3, 24.9) * mm, "end": v(110.3, 24.9) * mm});
            skLineSegment(sketch, "E17.9.1.3", {"start": v(102.3, 16.9) * mm, "end": v(102.3, 24.9) * mm});
            skLineSegment(sketch, "E17.9.2.0", {"start": v(102.3, 27.8) * mm, "end": v(110.3, 27.8) * mm});
            skLineSegment(sketch, "E17.9.2.1", {"start": v(110.3, 27.8) * mm, "end": v(110.3, 35.8) * mm});
            skLineSegment(sketch, "E17.9.2.2", {"start": v(102.3, 35.8) * mm, "end": v(110.3, 35.8) * mm});
            skLineSegment(sketch, "E17.9.2.3", {"start": v(102.3, 27.8) * mm, "end": v(102.3, 35.8) * mm});
            skLineSegment(sketch, "E17.9.3.0", {"start": v(102.3, 38.7) * mm, "end": v(110.3, 38.7) * mm});
            skLineSegment(sketch, "E17.9.3.1", {"start": v(110.3, 38.7) * mm, "end": v(110.3, 46.7) * mm});
            skLineSegment(sketch, "E17.9.3.2", {"start": v(102.3, 46.7) * mm, "end": v(110.3, 46.7) * mm});
            skLineSegment(sketch, "E17.9.3.3", {"start": v(102.3, 38.7) * mm, "end": v(102.3, 46.7) * mm});
            skLineSegment(sketch, "E17.9.4.0", {"start": v(102.3, 49.6) * mm, "end": v(110.3, 49.6) * mm});
            skLineSegment(sketch, "E17.9.4.1", {"start": v(110.3, 49.6) * mm, "end": v(110.3, 57.6) * mm});
            skLineSegment(sketch, "E17.9.4.2", {"start": v(102.3, 57.6) * mm, "end": v(110.3, 57.6) * mm});
            skLineSegment(sketch, "E17.9.4.3", {"start": v(102.3, 49.6) * mm, "end": v(102.3, 57.6) * mm});
            skLineSegment(sketch, "E17.9.5.0", {"start": v(102.3, 60.5) * mm, "end": v(110.3, 60.5) * mm});
            skLineSegment(sketch, "E17.9.5.1", {"start": v(110.3, 60.5) * mm, "end": v(110.3, 68.5) * mm});
            skLineSegment(sketch, "E17.9.5.2", {"start": v(102.3, 68.5) * mm, "end": v(110.3, 68.5) * mm});
            skLineSegment(sketch, "E17.9.5.3", {"start": v(102.3, 60.5) * mm, "end": v(102.3, 68.5) * mm});
            skLineSegment(sketch, "E17.9.6.0", {"start": v(102.3, 71.4) * mm, "end": v(110.3, 71.4) * mm});
            skLineSegment(sketch, "E17.9.6.1", {"start": v(110.3, 71.4) * mm, "end": v(110.3, 79.4) * mm});
            skLineSegment(sketch, "E17.9.6.2", {"start": v(102.3, 79.4) * mm, "end": v(110.3, 79.4) * mm});
            skLineSegment(sketch, "E17.9.6.3", {"start": v(102.3, 71.4) * mm, "end": v(102.3, 79.4) * mm});
            skLineSegment(sketch, "E17.9.7.0", {"start": v(102.3, 82.3) * mm, "end": v(110.3, 82.3) * mm});
            skLineSegment(sketch, "E17.9.7.1", {"start": v(110.3, 82.3) * mm, "end": v(110.3, 90.3) * mm});
            skLineSegment(sketch, "E17.9.7.2", {"start": v(102.3, 90.3) * mm, "end": v(110.3, 90.3) * mm});
            skLineSegment(sketch, "E17.9.7.3", {"start": v(102.3, 82.3) * mm, "end": v(102.3, 90.3) * mm});
            skLineSegment(sketch, "E17.9.8.0", {"start": v(102.3, 93.2) * mm, "end": v(110.3, 93.2) * mm});
            skLineSegment(sketch, "E17.9.8.1", {"start": v(110.3, 93.2) * mm, "end": v(110.3, 101.2) * mm});
            skLineSegment(sketch, "E17.9.8.2", {"start": v(102.3, 101.2) * mm, "end": v(110.3, 101.2) * mm});
            skLineSegment(sketch, "E17.9.8.3", {"start": v(102.3, 93.2) * mm, "end": v(102.3, 101.2) * mm});
            skLineSegment(sketch, "E17.9.9.0", {"start": v(102.3, 104.1) * mm, "end": v(110.3, 104.1) * mm});
            skLineSegment(sketch, "E17.9.9.1", {"start": v(110.3, 104.1) * mm, "end": v(110.3, 112.1) * mm});
            skLineSegment(sketch, "E17.9.9.2", {"start": v(102.3, 112.1) * mm, "end": v(110.3, 112.1) * mm});
            skLineSegment(sketch, "E17.9.9.3", {"start": v(102.3, 104.1) * mm, "end": v(102.3, 112.1) * mm});
            skLineSegment(sketch, "E17.9.10.0", {"start": v(102.3, 115) * mm, "end": v(110.3, 115) * mm});
            skLineSegment(sketch, "E17.9.10.1", {"start": v(110.3, 115) * mm, "end": v(110.3, 123) * mm});
            skLineSegment(sketch, "E17.9.10.2", {"start": v(102.3, 123) * mm, "end": v(110.3, 123) * mm});
            skLineSegment(sketch, "E17.9.10.3", {"start": v(102.3, 115) * mm, "end": v(102.3, 123) * mm});
            skLineSegment(sketch, "E17.9.11.0", {"start": v(102.3, 125.9) * mm, "end": v(110.3, 125.9) * mm});
            skLineSegment(sketch, "E17.9.11.1", {"start": v(110.3, 125.9) * mm, "end": v(110.3, 133.9) * mm});
            skLineSegment(sketch, "E17.9.11.2", {"start": v(102.3, 133.9) * mm, "end": v(110.3, 133.9) * mm});
            skLineSegment(sketch, "E17.9.11.3", {"start": v(102.3, 125.9) * mm, "end": v(102.3, 133.9) * mm});
            skLineSegment(sketch, "E17.10.0.0", {"start": v(113, 6) * mm, "end": v(121, 6) * mm});
            skLineSegment(sketch, "E17.10.0.1", {"start": v(121, 6) * mm, "end": v(121, 14) * mm});
            skLineSegment(sketch, "E17.10.0.2", {"start": v(113, 14) * mm, "end": v(121, 14) * mm});
            skLineSegment(sketch, "E17.10.0.3", {"start": v(113, 6) * mm, "end": v(113, 14) * mm});
            skLineSegment(sketch, "E17.10.1.0", {"start": v(113, 16.9) * mm, "end": v(121, 16.9) * mm});
            skLineSegment(sketch, "E17.10.1.1", {"start": v(121, 16.9) * mm, "end": v(121, 24.9) * mm});
            skLineSegment(sketch, "E17.10.1.2", {"start": v(113, 24.9) * mm, "end": v(121, 24.9) * mm});
            skLineSegment(sketch, "E17.10.1.3", {"start": v(113, 16.9) * mm, "end": v(113, 24.9) * mm});
            skLineSegment(sketch, "E17.10.2.0", {"start": v(113, 27.8) * mm, "end": v(121, 27.8) * mm});
            skLineSegment(sketch, "E17.10.2.1", {"start": v(121, 27.8) * mm, "end": v(121, 35.8) * mm});
            skLineSegment(sketch, "E17.10.2.2", {"start": v(113, 35.8) * mm, "end": v(121, 35.8) * mm});
            skLineSegment(sketch, "E17.10.2.3", {"start": v(113, 27.8) * mm, "end": v(113, 35.8) * mm});
            skLineSegment(sketch, "E17.10.3.0", {"start": v(113, 38.7) * mm, "end": v(121, 38.7) * mm});
            skLineSegment(sketch, "E17.10.3.1", {"start": v(121, 38.7) * mm, "end": v(121, 46.7) * mm});
            skLineSegment(sketch, "E17.10.3.2", {"start": v(113, 46.7) * mm, "end": v(121, 46.7) * mm});
            skLineSegment(sketch, "E17.10.3.3", {"start": v(113, 38.7) * mm, "end": v(113, 46.7) * mm});
            skLineSegment(sketch, "E17.10.4.0", {"start": v(113, 49.6) * mm, "end": v(121, 49.6) * mm});
            skLineSegment(sketch, "E17.10.4.1", {"start": v(121, 49.6) * mm, "end": v(121, 57.6) * mm});
            skLineSegment(sketch, "E17.10.4.2", {"start": v(113, 57.6) * mm, "end": v(121, 57.6) * mm});
            skLineSegment(sketch, "E17.10.4.3", {"start": v(113, 49.6) * mm, "end": v(113, 57.6) * mm});
            skLineSegment(sketch, "E17.10.5.0", {"start": v(113, 60.5) * mm, "end": v(121, 60.5) * mm});
            skLineSegment(sketch, "E17.10.5.1", {"start": v(121, 60.5) * mm, "end": v(121, 68.5) * mm});
            skLineSegment(sketch, "E17.10.5.2", {"start": v(113, 68.5) * mm, "end": v(121, 68.5) * mm});
            skLineSegment(sketch, "E17.10.5.3", {"start": v(113, 60.5) * mm, "end": v(113, 68.5) * mm});
            skLineSegment(sketch, "E17.10.6.0", {"start": v(113, 71.4) * mm, "end": v(121, 71.4) * mm});
            skLineSegment(sketch, "E17.10.6.1", {"start": v(121, 71.4) * mm, "end": v(121, 79.4) * mm});
            skLineSegment(sketch, "E17.10.6.2", {"start": v(113, 79.4) * mm, "end": v(121, 79.4) * mm});
            skLineSegment(sketch, "E17.10.6.3", {"start": v(113, 71.4) * mm, "end": v(113, 79.4) * mm});
            skLineSegment(sketch, "E17.10.7.0", {"start": v(113, 82.3) * mm, "end": v(121, 82.3) * mm});
            skLineSegment(sketch, "E17.10.7.1", {"start": v(121, 82.3) * mm, "end": v(121, 90.3) * mm});
            skLineSegment(sketch, "E17.10.7.2", {"start": v(113, 90.3) * mm, "end": v(121, 90.3) * mm});
            skLineSegment(sketch, "E17.10.7.3", {"start": v(113, 82.3) * mm, "end": v(113, 90.3) * mm});
            skLineSegment(sketch, "E17.10.8.0", {"start": v(113, 93.2) * mm, "end": v(121, 93.2) * mm});
            skLineSegment(sketch, "E17.10.8.1", {"start": v(121, 93.2) * mm, "end": v(121, 101.2) * mm});
            skLineSegment(sketch, "E17.10.8.2", {"start": v(113, 101.2) * mm, "end": v(121, 101.2) * mm});
            skLineSegment(sketch, "E17.10.8.3", {"start": v(113, 93.2) * mm, "end": v(113, 101.2) * mm});
            skLineSegment(sketch, "E17.10.9.0", {"start": v(113, 104.1) * mm, "end": v(121, 104.1) * mm});
            skLineSegment(sketch, "E17.10.9.1", {"start": v(121, 104.1) * mm, "end": v(121, 112.1) * mm});
            skLineSegment(sketch, "E17.10.9.2", {"start": v(113, 112.1) * mm, "end": v(121, 112.1) * mm});
            skLineSegment(sketch, "E17.10.9.3", {"start": v(113, 104.1) * mm, "end": v(113, 112.1) * mm});
            skLineSegment(sketch, "E17.10.10.0", {"start": v(113, 115) * mm, "end": v(121, 115) * mm});
            skLineSegment(sketch, "E17.10.10.1", {"start": v(121, 115) * mm, "end": v(121, 123) * mm});
            skLineSegment(sketch, "E17.10.10.2", {"start": v(113, 123) * mm, "end": v(121, 123) * mm});
            skLineSegment(sketch, "E17.10.10.3", {"start": v(113, 115) * mm, "end": v(113, 123) * mm});
            skLineSegment(sketch, "E17.10.11.0", {"start": v(113, 125.9) * mm, "end": v(121, 125.9) * mm});
            skLineSegment(sketch, "E17.10.11.1", {"start": v(121, 125.9) * mm, "end": v(121, 133.9) * mm});
            skLineSegment(sketch, "E17.10.11.2", {"start": v(113, 133.9) * mm, "end": v(121, 133.9) * mm});
            skLineSegment(sketch, "E17.10.11.3", {"start": v(113, 125.9) * mm, "end": v(113, 133.9) * mm});
            skLineSegment(sketch, "E17.11.0.0", {"start": v(123.7, 6) * mm, "end": v(131.7, 6) * mm});
            skLineSegment(sketch, "E17.11.0.1", {"start": v(131.7, 6) * mm, "end": v(131.7, 14) * mm});
            skLineSegment(sketch, "E17.11.0.2", {"start": v(123.7, 14) * mm, "end": v(131.7, 14) * mm});
            skLineSegment(sketch, "E17.11.0.3", {"start": v(123.7, 6) * mm, "end": v(123.7, 14) * mm});
            skLineSegment(sketch, "E17.11.1.0", {"start": v(123.7, 16.9) * mm, "end": v(131.7, 16.9) * mm});
            skLineSegment(sketch, "E17.11.1.1", {"start": v(131.7, 16.9) * mm, "end": v(131.7, 24.9) * mm});
            skLineSegment(sketch, "E17.11.1.2", {"start": v(123.7, 24.9) * mm, "end": v(131.7, 24.9) * mm});
            skLineSegment(sketch, "E17.11.1.3", {"start": v(123.7, 16.9) * mm, "end": v(123.7, 24.9) * mm});
            skLineSegment(sketch, "E17.11.2.0", {"start": v(123.7, 27.8) * mm, "end": v(131.7, 27.8) * mm});
            skLineSegment(sketch, "E17.11.2.1", {"start": v(131.7, 27.8) * mm, "end": v(131.7, 35.8) * mm});
            skLineSegment(sketch, "E17.11.2.2", {"start": v(123.7, 35.8) * mm, "end": v(131.7, 35.8) * mm});
            skLineSegment(sketch, "E17.11.2.3", {"start": v(123.7, 27.8) * mm, "end": v(123.7, 35.8) * mm});
            skLineSegment(sketch, "E17.11.3.0", {"start": v(123.7, 38.7) * mm, "end": v(131.7, 38.7) * mm});
            skLineSegment(sketch, "E17.11.3.1", {"start": v(131.7, 38.7) * mm, "end": v(131.7, 46.7) * mm});
            skLineSegment(sketch, "E17.11.3.2", {"start": v(123.7, 46.7) * mm, "end": v(131.7, 46.7) * mm});
            skLineSegment(sketch, "E17.11.3.3", {"start": v(123.7, 38.7) * mm, "end": v(123.7, 46.7) * mm});
            skLineSegment(sketch, "E17.11.4.0", {"start": v(123.7, 49.6) * mm, "end": v(131.7, 49.6) * mm});
            skLineSegment(sketch, "E17.11.4.1", {"start": v(131.7, 49.6) * mm, "end": v(131.7, 57.6) * mm});
            skLineSegment(sketch, "E17.11.4.2", {"start": v(123.7, 57.6) * mm, "end": v(131.7, 57.6) * mm});
            skLineSegment(sketch, "E17.11.4.3", {"start": v(123.7, 49.6) * mm, "end": v(123.7, 57.6) * mm});
            skLineSegment(sketch, "E17.11.5.0", {"start": v(123.7, 60.5) * mm, "end": v(131.7, 60.5) * mm});
            skLineSegment(sketch, "E17.11.5.1", {"start": v(131.7, 60.5) * mm, "end": v(131.7, 68.5) * mm});
            skLineSegment(sketch, "E17.11.5.2", {"start": v(123.7, 68.5) * mm, "end": v(131.7, 68.5) * mm});
            skLineSegment(sketch, "E17.11.5.3", {"start": v(123.7, 60.5) * mm, "end": v(123.7, 68.5) * mm});
            skLineSegment(sketch, "E17.11.6.0", {"start": v(123.7, 71.4) * mm, "end": v(131.7, 71.4) * mm});
            skLineSegment(sketch, "E17.11.6.1", {"start": v(131.7, 71.4) * mm, "end": v(131.7, 79.4) * mm});
            skLineSegment(sketch, "E17.11.6.2", {"start": v(123.7, 79.4) * mm, "end": v(131.7, 79.4) * mm});
            skLineSegment(sketch, "E17.11.6.3", {"start": v(123.7, 71.4) * mm, "end": v(123.7, 79.4) * mm});
            skLineSegment(sketch, "E17.11.7.0", {"start": v(123.7, 82.3) * mm, "end": v(131.7, 82.3) * mm});
            skLineSegment(sketch, "E17.11.7.1", {"start": v(131.7, 82.3) * mm, "end": v(131.7, 90.3) * mm});
            skLineSegment(sketch, "E17.11.7.2", {"start": v(123.7, 90.3) * mm, "end": v(131.7, 90.3) * mm});
            skLineSegment(sketch, "E17.11.7.3", {"start": v(123.7, 82.3) * mm, "end": v(123.7, 90.3) * mm});
            skLineSegment(sketch, "E17.11.8.0", {"start": v(123.7, 93.2) * mm, "end": v(131.7, 93.2) * mm});
            skLineSegment(sketch, "E17.11.8.1", {"start": v(131.7, 93.2) * mm, "end": v(131.7, 101.2) * mm});
            skLineSegment(sketch, "E17.11.8.2", {"start": v(123.7, 101.2) * mm, "end": v(131.7, 101.2) * mm});
            skLineSegment(sketch, "E17.11.8.3", {"start": v(123.7, 93.2) * mm, "end": v(123.7, 101.2) * mm});
            skLineSegment(sketch, "E17.11.9.0", {"start": v(123.7, 104.1) * mm, "end": v(131.7, 104.1) * mm});
            skLineSegment(sketch, "E17.11.9.1", {"start": v(131.7, 104.1) * mm, "end": v(131.7, 112.1) * mm});
            skLineSegment(sketch, "E17.11.9.2", {"start": v(123.7, 112.1) * mm, "end": v(131.7, 112.1) * mm});
            skLineSegment(sketch, "E17.11.9.3", {"start": v(123.7, 104.1) * mm, "end": v(123.7, 112.1) * mm});
            skLineSegment(sketch, "E17.11.10.0", {"start": v(123.7, 115) * mm, "end": v(131.7, 115) * mm});
            skLineSegment(sketch, "E17.11.10.1", {"start": v(131.7, 115) * mm, "end": v(131.7, 123) * mm});
            skLineSegment(sketch, "E17.11.10.2", {"start": v(123.7, 123) * mm, "end": v(131.7, 123) * mm});
            skLineSegment(sketch, "E17.11.10.3", {"start": v(123.7, 115) * mm, "end": v(123.7, 123) * mm});
            skLineSegment(sketch, "E17.11.11.0", {"start": v(123.7, 125.9) * mm, "end": v(131.7, 125.9) * mm});
            skLineSegment(sketch, "E17.11.11.1", {"start": v(131.7, 125.9) * mm, "end": v(131.7, 133.9) * mm});
            skLineSegment(sketch, "E17.11.11.2", {"start": v(123.7, 133.9) * mm, "end": v(131.7, 133.9) * mm});
            skLineSegment(sketch, "E17.11.11.3", {"start": v(123.7, 125.9) * mm, "end": v(123.7, 133.9) * mm});
            skLineSegment(sketch, "E17.12.0.0", {"start": v(134.4, 6) * mm, "end": v(142.4, 6) * mm});
            skLineSegment(sketch, "E17.12.0.1", {"start": v(142.4, 6) * mm, "end": v(142.4, 14) * mm});
            skLineSegment(sketch, "E17.12.0.2", {"start": v(134.4, 14) * mm, "end": v(142.4, 14) * mm});
            skLineSegment(sketch, "E17.12.0.3", {"start": v(134.4, 6) * mm, "end": v(134.4, 14) * mm});
            skLineSegment(sketch, "E17.12.1.0", {"start": v(134.4, 16.9) * mm, "end": v(142.4, 16.9) * mm});
            skLineSegment(sketch, "E17.12.1.1", {"start": v(142.4, 16.9) * mm, "end": v(142.4, 24.9) * mm});
            skLineSegment(sketch, "E17.12.1.2", {"start": v(134.4, 24.9) * mm, "end": v(142.4, 24.9) * mm});
            skLineSegment(sketch, "E17.12.1.3", {"start": v(134.4, 16.9) * mm, "end": v(134.4, 24.9) * mm});
            skLineSegment(sketch, "E17.12.2.0", {"start": v(134.4, 27.8) * mm, "end": v(142.4, 27.8) * mm});
            skLineSegment(sketch, "E17.12.2.1", {"start": v(142.4, 27.8) * mm, "end": v(142.4, 35.8) * mm});
            skLineSegment(sketch, "E17.12.2.2", {"start": v(134.4, 35.8) * mm, "end": v(142.4, 35.8) * mm});
            skLineSegment(sketch, "E17.12.2.3", {"start": v(134.4, 27.8) * mm, "end": v(134.4, 35.8) * mm});
            skLineSegment(sketch, "E17.12.3.0", {"start": v(134.4, 38.7) * mm, "end": v(142.4, 38.7) * mm});
            skLineSegment(sketch, "E17.12.3.1", {"start": v(142.4, 38.7) * mm, "end": v(142.4, 46.7) * mm});
            skLineSegment(sketch, "E17.12.3.2", {"start": v(134.4, 46.7) * mm, "end": v(142.4, 46.7) * mm});
            skLineSegment(sketch, "E17.12.3.3", {"start": v(134.4, 38.7) * mm, "end": v(134.4, 46.7) * mm});
            skLineSegment(sketch, "E17.12.4.0", {"start": v(134.4, 49.6) * mm, "end": v(142.4, 49.6) * mm});
            skLineSegment(sketch, "E17.12.4.1", {"start": v(142.4, 49.6) * mm, "end": v(142.4, 57.6) * mm});
            skLineSegment(sketch, "E17.12.4.2", {"start": v(134.4, 57.6) * mm, "end": v(142.4, 57.6) * mm});
            skLineSegment(sketch, "E17.12.4.3", {"start": v(134.4, 49.6) * mm, "end": v(134.4, 57.6) * mm});
            skLineSegment(sketch, "E17.12.5.0", {"start": v(134.4, 60.5) * mm, "end": v(142.4, 60.5) * mm});
            skLineSegment(sketch, "E17.12.5.1", {"start": v(142.4, 60.5) * mm, "end": v(142.4, 68.5) * mm});
            skLineSegment(sketch, "E17.12.5.2", {"start": v(134.4, 68.5) * mm, "end": v(142.4, 68.5) * mm});
            skLineSegment(sketch, "E17.12.5.3", {"start": v(134.4, 60.5) * mm, "end": v(134.4, 68.5) * mm});
            skLineSegment(sketch, "E17.12.6.0", {"start": v(134.4, 71.4) * mm, "end": v(142.4, 71.4) * mm});
            skLineSegment(sketch, "E17.12.6.1", {"start": v(142.4, 71.4) * mm, "end": v(142.4, 79.4) * mm});
            skLineSegment(sketch, "E17.12.6.2", {"start": v(134.4, 79.4) * mm, "end": v(142.4, 79.4) * mm});
            skLineSegment(sketch, "E17.12.6.3", {"start": v(134.4, 71.4) * mm, "end": v(134.4, 79.4) * mm});
            skLineSegment(sketch, "E17.12.7.0", {"start": v(134.4, 82.3) * mm, "end": v(142.4, 82.3) * mm});
            skLineSegment(sketch, "E17.12.7.1", {"start": v(142.4, 82.3) * mm, "end": v(142.4, 90.3) * mm});
            skLineSegment(sketch, "E17.12.7.2", {"start": v(134.4, 90.3) * mm, "end": v(142.4, 90.3) * mm});
            skLineSegment(sketch, "E17.12.7.3", {"start": v(134.4, 82.3) * mm, "end": v(134.4, 90.3) * mm});
            skLineSegment(sketch, "E17.12.8.0", {"start": v(134.4, 93.2) * mm, "end": v(142.4, 93.2) * mm});
            skLineSegment(sketch, "E17.12.8.1", {"start": v(142.4, 93.2) * mm, "end": v(142.4, 101.2) * mm});
            skLineSegment(sketch, "E17.12.8.2", {"start": v(134.4, 101.2) * mm, "end": v(142.4, 101.2) * mm});
            skLineSegment(sketch, "E17.12.8.3", {"start": v(134.4, 93.2) * mm, "end": v(134.4, 101.2) * mm});
            skLineSegment(sketch, "E17.12.9.0", {"start": v(134.4, 104.1) * mm, "end": v(142.4, 104.1) * mm});
            skLineSegment(sketch, "E17.12.9.1", {"start": v(142.4, 104.1) * mm, "end": v(142.4, 112.1) * mm});
            skLineSegment(sketch, "E17.12.9.2", {"start": v(134.4, 112.1) * mm, "end": v(142.4, 112.1) * mm});
            skLineSegment(sketch, "E17.12.9.3", {"start": v(134.4, 104.1) * mm, "end": v(134.4, 112.1) * mm});
            skLineSegment(sketch, "E17.12.10.0", {"start": v(134.4, 115) * mm, "end": v(142.4, 115) * mm});
            skLineSegment(sketch, "E17.12.10.1", {"start": v(142.4, 115) * mm, "end": v(142.4, 123) * mm});
            skLineSegment(sketch, "E17.12.10.2", {"start": v(134.4, 123) * mm, "end": v(142.4, 123) * mm});
            skLineSegment(sketch, "E17.12.10.3", {"start": v(134.4, 115) * mm, "end": v(134.4, 123) * mm});
            skLineSegment(sketch, "E17.12.11.0", {"start": v(134.4, 125.9) * mm, "end": v(142.4, 125.9) * mm});
            skLineSegment(sketch, "E17.12.11.1", {"start": v(142.4, 125.9) * mm, "end": v(142.4, 133.9) * mm});
            skLineSegment(sketch, "E17.12.11.2", {"start": v(134.4, 133.9) * mm, "end": v(142.4, 133.9) * mm});
            skLineSegment(sketch, "E17.12.11.3", {"start": v(134.4, 125.9) * mm, "end": v(134.4, 133.9) * mm});
            skLineSegment(sketch, "E17.13.0.0", {"start": v(145.1, 6) * mm, "end": v(153.1, 6) * mm});
            skLineSegment(sketch, "E17.13.0.1", {"start": v(153.1, 6) * mm, "end": v(153.1, 14) * mm});
            skLineSegment(sketch, "E17.13.0.2", {"start": v(145.1, 14) * mm, "end": v(153.1, 14) * mm});
            skLineSegment(sketch, "E17.13.0.3", {"start": v(145.1, 6) * mm, "end": v(145.1, 14) * mm});
            skLineSegment(sketch, "E17.13.1.0", {"start": v(145.1, 16.9) * mm, "end": v(153.1, 16.9) * mm});
            skLineSegment(sketch, "E17.13.1.1", {"start": v(153.1, 16.9) * mm, "end": v(153.1, 24.9) * mm});
            skLineSegment(sketch, "E17.13.1.2", {"start": v(145.1, 24.9) * mm, "end": v(153.1, 24.9) * mm});
            skLineSegment(sketch, "E17.13.1.3", {"start": v(145.1, 16.9) * mm, "end": v(145.1, 24.9) * mm});
            skLineSegment(sketch, "E17.13.2.0", {"start": v(145.1, 27.8) * mm, "end": v(153.1, 27.8) * mm});
            skLineSegment(sketch, "E17.13.2.1", {"start": v(153.1, 27.8) * mm, "end": v(153.1, 35.8) * mm});
            skLineSegment(sketch, "E17.13.2.2", {"start": v(145.1, 35.8) * mm, "end": v(153.1, 35.8) * mm});
            skLineSegment(sketch, "E17.13.2.3", {"start": v(145.1, 27.8) * mm, "end": v(145.1, 35.8) * mm});
            skLineSegment(sketch, "E17.13.3.0", {"start": v(145.1, 38.7) * mm, "end": v(153.1, 38.7) * mm});
            skLineSegment(sketch, "E17.13.3.1", {"start": v(153.1, 38.7) * mm, "end": v(153.1, 46.7) * mm});
            skLineSegment(sketch, "E17.13.3.2", {"start": v(145.1, 46.7) * mm, "end": v(153.1, 46.7) * mm});
            skLineSegment(sketch, "E17.13.3.3", {"start": v(145.1, 38.7) * mm, "end": v(145.1, 46.7) * mm});
            skLineSegment(sketch, "E17.13.4.0", {"start": v(145.1, 49.6) * mm, "end": v(153.1, 49.6) * mm});
            skLineSegment(sketch, "E17.13.4.1", {"start": v(153.1, 49.6) * mm, "end": v(153.1, 57.6) * mm});
            skLineSegment(sketch, "E17.13.4.2", {"start": v(145.1, 57.6) * mm, "end": v(153.1, 57.6) * mm});
            skLineSegment(sketch, "E17.13.4.3", {"start": v(145.1, 49.6) * mm, "end": v(145.1, 57.6) * mm});
            skLineSegment(sketch, "E17.13.5.0", {"start": v(145.1, 60.5) * mm, "end": v(153.1, 60.5) * mm});
            skLineSegment(sketch, "E17.13.5.1", {"start": v(153.1, 60.5) * mm, "end": v(153.1, 68.5) * mm});
            skLineSegment(sketch, "E17.13.5.2", {"start": v(145.1, 68.5) * mm, "end": v(153.1, 68.5) * mm});
            skLineSegment(sketch, "E17.13.5.3", {"start": v(145.1, 60.5) * mm, "end": v(145.1, 68.5) * mm});
            skLineSegment(sketch, "E17.13.6.0", {"start": v(145.1, 71.4) * mm, "end": v(153.1, 71.4) * mm});
            skLineSegment(sketch, "E17.13.6.1", {"start": v(153.1, 71.4) * mm, "end": v(153.1, 79.4) * mm});
            skLineSegment(sketch, "E17.13.6.2", {"start": v(145.1, 79.4) * mm, "end": v(153.1, 79.4) * mm});
            skLineSegment(sketch, "E17.13.6.3", {"start": v(145.1, 71.4) * mm, "end": v(145.1, 79.4) * mm});
            skLineSegment(sketch, "E17.13.7.0", {"start": v(145.1, 82.3) * mm, "end": v(153.1, 82.3) * mm});
            skLineSegment(sketch, "E17.13.7.1", {"start": v(153.1, 82.3) * mm, "end": v(153.1, 90.3) * mm});
            skLineSegment(sketch, "E17.13.7.2", {"start": v(145.1, 90.3) * mm, "end": v(153.1, 90.3) * mm});
            skLineSegment(sketch, "E17.13.7.3", {"start": v(145.1, 82.3) * mm, "end": v(145.1, 90.3) * mm});
            skLineSegment(sketch, "E17.13.8.0", {"start": v(145.1, 93.2) * mm, "end": v(153.1, 93.2) * mm});
            skLineSegment(sketch, "E17.13.8.1", {"start": v(153.1, 93.2) * mm, "end": v(153.1, 101.2) * mm});
            skLineSegment(sketch, "E17.13.8.2", {"start": v(145.1, 101.2) * mm, "end": v(153.1, 101.2) * mm});
            skLineSegment(sketch, "E17.13.8.3", {"start": v(145.1, 93.2) * mm, "end": v(145.1, 101.2) * mm});
            skLineSegment(sketch, "E17.13.9.0", {"start": v(145.1, 104.1) * mm, "end": v(153.1, 104.1) * mm});
            skLineSegment(sketch, "E17.13.9.1", {"start": v(153.1, 104.1) * mm, "end": v(153.1, 112.1) * mm});
            skLineSegment(sketch, "E17.13.9.2", {"start": v(145.1, 112.1) * mm, "end": v(153.1, 112.1) * mm});
            skLineSegment(sketch, "E17.13.9.3", {"start": v(145.1, 104.1) * mm, "end": v(145.1, 112.1) * mm});
            skLineSegment(sketch, "E17.13.10.0", {"start": v(145.1, 115) * mm, "end": v(153.1, 115) * mm});
            skLineSegment(sketch, "E17.13.10.1", {"start": v(153.1, 115) * mm, "end": v(153.1, 123) * mm});
            skLineSegment(sketch, "E17.13.10.2", {"start": v(145.1, 123) * mm, "end": v(153.1, 123) * mm});
            skLineSegment(sketch, "E17.13.10.3", {"start": v(145.1, 115) * mm, "end": v(145.1, 123) * mm});
            skLineSegment(sketch, "E17.13.11.0", {"start": v(145.1, 125.9) * mm, "end": v(153.1, 125.9) * mm});
            skLineSegment(sketch, "E17.13.11.1", {"start": v(153.1, 125.9) * mm, "end": v(153.1, 133.9) * mm});
            skLineSegment(sketch, "E17.13.11.2", {"start": v(145.1, 133.9) * mm, "end": v(153.1, 133.9) * mm});
            skLineSegment(sketch, "E17.13.11.3", {"start": v(145.1, 125.9) * mm, "end": v(145.1, 133.9) * mm});
            skLineSegment(sketch, "E17.14.0.0", {"start": v(155.8, 6) * mm, "end": v(163.8, 6) * mm});
            skLineSegment(sketch, "E17.14.0.1", {"start": v(163.8, 6) * mm, "end": v(163.8, 14) * mm});
            skLineSegment(sketch, "E17.14.0.2", {"start": v(155.8, 14) * mm, "end": v(163.8, 14) * mm});
            skLineSegment(sketch, "E17.14.0.3", {"start": v(155.8, 6) * mm, "end": v(155.8, 14) * mm});
            skLineSegment(sketch, "E17.14.1.0", {"start": v(155.8, 16.9) * mm, "end": v(163.8, 16.9) * mm});
            skLineSegment(sketch, "E17.14.1.1", {"start": v(163.8, 16.9) * mm, "end": v(163.8, 24.9) * mm});
            skLineSegment(sketch, "E17.14.1.2", {"start": v(155.8, 24.9) * mm, "end": v(163.8, 24.9) * mm});
            skLineSegment(sketch, "E17.14.1.3", {"start": v(155.8, 16.9) * mm, "end": v(155.8, 24.9) * mm});
            skLineSegment(sketch, "E17.14.2.0", {"start": v(155.8, 27.8) * mm, "end": v(163.8, 27.8) * mm});
            skLineSegment(sketch, "E17.14.2.1", {"start": v(163.8, 27.8) * mm, "end": v(163.8, 35.8) * mm});
            skLineSegment(sketch, "E17.14.2.2", {"start": v(155.8, 35.8) * mm, "end": v(163.8, 35.8) * mm});
            skLineSegment(sketch, "E17.14.2.3", {"start": v(155.8, 27.8) * mm, "end": v(155.8, 35.8) * mm});
            skLineSegment(sketch, "E17.14.3.0", {"start": v(155.8, 38.7) * mm, "end": v(163.8, 38.7) * mm});
            skLineSegment(sketch, "E17.14.3.1", {"start": v(163.8, 38.7) * mm, "end": v(163.8, 46.7) * mm});
            skLineSegment(sketch, "E17.14.3.2", {"start": v(155.8, 46.7) * mm, "end": v(163.8, 46.7) * mm});
            skLineSegment(sketch, "E17.14.3.3", {"start": v(155.8, 38.7) * mm, "end": v(155.8, 46.7) * mm});
            skLineSegment(sketch, "E17.14.4.0", {"start": v(155.8, 49.6) * mm, "end": v(163.8, 49.6) * mm});
            skLineSegment(sketch, "E17.14.4.1", {"start": v(163.8, 49.6) * mm, "end": v(163.8, 57.6) * mm});
            skLineSegment(sketch, "E17.14.4.2", {"start": v(155.8, 57.6) * mm, "end": v(163.8, 57.6) * mm});
            skLineSegment(sketch, "E17.14.4.3", {"start": v(155.8, 49.6) * mm, "end": v(155.8, 57.6) * mm});
            skLineSegment(sketch, "E17.14.5.0", {"start": v(155.8, 60.5) * mm, "end": v(163.8, 60.5) * mm});
            skLineSegment(sketch, "E17.14.5.1", {"start": v(163.8, 60.5) * mm, "end": v(163.8, 68.5) * mm});
            skLineSegment(sketch, "E17.14.5.2", {"start": v(155.8, 68.5) * mm, "end": v(163.8, 68.5) * mm});
            skLineSegment(sketch, "E17.14.5.3", {"start": v(155.8, 60.5) * mm, "end": v(155.8, 68.5) * mm});
            skLineSegment(sketch, "E17.14.6.0", {"start": v(155.8, 71.4) * mm, "end": v(163.8, 71.4) * mm});
            skLineSegment(sketch, "E17.14.6.1", {"start": v(163.8, 71.4) * mm, "end": v(163.8, 79.4) * mm});
            skLineSegment(sketch, "E17.14.6.2", {"start": v(155.8, 79.4) * mm, "end": v(163.8, 79.4) * mm});
            skLineSegment(sketch, "E17.14.6.3", {"start": v(155.8, 71.4) * mm, "end": v(155.8, 79.4) * mm});
            skLineSegment(sketch, "E17.14.7.0", {"start": v(155.8, 82.3) * mm, "end": v(163.8, 82.3) * mm});
            skLineSegment(sketch, "E17.14.7.1", {"start": v(163.8, 82.3) * mm, "end": v(163.8, 90.3) * mm});
            skLineSegment(sketch, "E17.14.7.2", {"start": v(155.8, 90.3) * mm, "end": v(163.8, 90.3) * mm});
            skLineSegment(sketch, "E17.14.7.3", {"start": v(155.8, 82.3) * mm, "end": v(155.8, 90.3) * mm});
            skLineSegment(sketch, "E17.14.8.0", {"start": v(155.8, 93.2) * mm, "end": v(163.8, 93.2) * mm});
            skLineSegment(sketch, "E17.14.8.1", {"start": v(163.8, 93.2) * mm, "end": v(163.8, 101.2) * mm});
            skLineSegment(sketch, "E17.14.8.2", {"start": v(155.8, 101.2) * mm, "end": v(163.8, 101.2) * mm});
            skLineSegment(sketch, "E17.14.8.3", {"start": v(155.8, 93.2) * mm, "end": v(155.8, 101.2) * mm});
            skLineSegment(sketch, "E17.14.9.0", {"start": v(155.8, 104.1) * mm, "end": v(163.8, 104.1) * mm});
            skLineSegment(sketch, "E17.14.9.1", {"start": v(163.8, 104.1) * mm, "end": v(163.8, 112.1) * mm});
            skLineSegment(sketch, "E17.14.9.2", {"start": v(155.8, 112.1) * mm, "end": v(163.8, 112.1) * mm});
            skLineSegment(sketch, "E17.14.9.3", {"start": v(155.8, 104.1) * mm, "end": v(155.8, 112.1) * mm});
            skLineSegment(sketch, "E17.14.10.0", {"start": v(155.8, 115) * mm, "end": v(163.8, 115) * mm});
            skLineSegment(sketch, "E17.14.10.1", {"start": v(163.8, 115) * mm, "end": v(163.8, 123) * mm});
            skLineSegment(sketch, "E17.14.10.2", {"start": v(155.8, 123) * mm, "end": v(163.8, 123) * mm});
            skLineSegment(sketch, "E17.14.10.3", {"start": v(155.8, 115) * mm, "end": v(155.8, 123) * mm});
            skLineSegment(sketch, "E17.14.11.0", {"start": v(155.8, 125.9) * mm, "end": v(163.8, 125.9) * mm});
            skLineSegment(sketch, "E17.14.11.1", {"start": v(163.8, 125.9) * mm, "end": v(163.8, 133.9) * mm});
            skLineSegment(sketch, "E17.14.11.2", {"start": v(155.8, 133.9) * mm, "end": v(163.8, 133.9) * mm});
            skLineSegment(sketch, "E17.14.11.3", {"start": v(155.8, 125.9) * mm, "end": v(155.8, 133.9) * mm});
            skLineSegment(sketch, "E17.direction1", {"start": v(6, 6) * mm, "end": v(16.7, 6) * mm, "construction": true});
            skLineSegment(sketch, "E17.direction2", {"start": v(6, 6) * mm, "end": v(6, 16.9) * mm, "construction": true});
            skSolve(sketch);
        }
        {
            var Q0;
            Q0 = qSketchRegion(id + "F9", true);
            extrude(context, id + "F10", {"entities" : qUnion([Q0]), "operationType" : NewBodyOperationType.REMOVE, "depth" : 25 * mm, "offsetDistance" : 25 * mm});
        }
        {
            var Q0;
            Q0=makeQuery(id+"F1.opExtrude","SWEPT_FACE",FACE,{"disambiguationData":[OSD([sQuery(id+"F0.wireOp",EDGE,"E0.right")])]});
            var sketch = newSketch(context, id + "F11", { "sketchPlane" : qUnion([Q0])});
            skLineSegment(sketch, "E18.bottom", {"start": v(49, 130) * mm, "end": v(91, 130) * mm});
            skLineSegment(sketch, "E18.top", {"start": v(49, 83) * mm, "end": v(91, 83) * mm});
            skLineSegment(sketch, "E18.left", {"start": v(49, 130) * mm, "end": v(49, 83) * mm});
            skLineSegment(sketch, "E18.right", {"start": v(91, 130) * mm, "end": v(91, 83) * mm});
            skSolve(sketch);
        }
        {
            var Q0;
            Q0 = qSketchRegion(id + "F11", true);
            extrude(context, id + "F12", {"entities" : qUnion([Q0]), "operationType" : NewBodyOperationType.ADD, "oppositeDirection" : true, "depth" : 3 * mm, "offsetDistance" : 25 * mm});
        }
        {
            var Q0;
            Q0=makeQuery(id+"F1.opExtrude","SWEPT_FACE",FACE,{"disambiguationData":[OSD([sQuery(id+"F0.wireOp",EDGE,"E0.left")])]});
            var sketch = newSketch(context, id + "F13", { "sketchPlane" : qUnion([Q0])});
            skLineSegment(sketch, "E19.bottom", {"start": v(-91, 130) * mm, "end": v(-49, 130) * mm});
            skLineSegment(sketch, "E19.top", {"start": v(-91, 83) * mm, "end": v(-49, 83) * mm});
            skLineSegment(sketch, "E19.left", {"start": v(-91, 130) * mm, "end": v(-91, 83) * mm});
            skLineSegment(sketch, "E19.right", {"start": v(-49, 130) * mm, "end": v(-49, 83) * mm});
            skSolve(sketch);
        }
        {
            var Q0;
            Q0 = qSketchRegion(id + "F13", true);
            extrude(context, id + "F14", {"entities" : qUnion([Q0]), "operationType" : NewBodyOperationType.ADD, "oppositeDirection" : true, "depth" : 3 * mm, "offsetDistance" : 25 * mm});
        }
        {
            var Q0;
            Q0=makeQuery(id+"F12.boolean.opBoolean","MERGE",FACE,{"derivedFrom":[makeQuery(id+"F1.opExtrude","SWEPT_FACE",FACE,{"disambiguationData":[OSD([sQuery(id+"F0.wireOp",EDGE,"E0.right")])]}),makeQuery(id+"F12.opExtrude","CAP_FACE",FACE,{"disambiguationData":[OSD([sQuery(id+"F11.wireOp",EDGE,"E18.bottom"),sQuery(id+"F11.wireOp",EDGE,"E18.top"),sQuery(id+"F11.wireOp",EDGE,"E18.left"),sQuery(id+"F11.wireOp",EDGE,"E18.right")])],"isStart":true})]});
            var sketch = newSketch(context, id + "F15", { "sketchPlane" : qUnion([Q0])});
            skLineSegment(sketch, "E20", {"start": v(70, 130) * mm, "end": v(71.4, -15.45) * mm, "construction": true});
            skCircle(sketch, "E21", {"center": v(80.14, 115) * mm, "radius": 4 * mm});
            skCircle(sketch, "E22", {"center": v(60.34, 95) * mm, "radius": 4 * mm});
            skSolve(sketch);
        }
        {
            var Q0;
            Q0 = qSketchRegion(id + "F15", true);
            extrude(context, id + "F16", {"entities" : qUnion([Q0]), "operationType" : NewBodyOperationType.REMOVE, "oppositeDirection" : true, "depth" : 5 * mm, "offsetDistance" : 25 * mm});
        }
        {
            var Q0;
            Q0=makeQuery(id+"F14.boolean.opBoolean","MERGE",FACE,{"derivedFrom":[makeQuery(id+"F1.opExtrude","SWEPT_FACE",FACE,{"disambiguationData":[OSD([sQuery(id+"F0.wireOp",EDGE,"E0.left")])]}),makeQuery(id+"F14.opExtrude","CAP_FACE",FACE,{"disambiguationData":[OSD([sQuery(id+"F13.wireOp",EDGE,"E19.bottom"),sQuery(id+"F13.wireOp",EDGE,"E19.top"),sQuery(id+"F13.wireOp",EDGE,"E19.left"),sQuery(id+"F13.wireOp",EDGE,"E19.right")])],"isStart":true})]});
            var sketch = newSketch(context, id + "F17", { "sketchPlane" : qUnion([Q0])});
            skLineSegment(sketch, "E23", {"start": v(-70, 130) * mm, "end": v(-70, -4.6) * mm, "construction": true});
            skPoint(sketch, "E23.endSnap0", {"position": v(-70, 36) * mm});
            skCircle(sketch, "E24", {"center": v(-60, 115) * mm, "radius": 4 * mm});
            skCircle(sketch, "E25", {"center": v(-80, 95) * mm, "radius": 4 * mm});
            skSolve(sketch);
        }
        {
            var Q0;
            Q0 = qSketchRegion(id + "F17", true);
            extrude(context, id + "F18", {"entities" : qUnion([Q0]), "operationType" : NewBodyOperationType.REMOVE, "oppositeDirection" : true, "depth" : 5 * mm, "offsetDistance" : 25 * mm});
        }
    });
